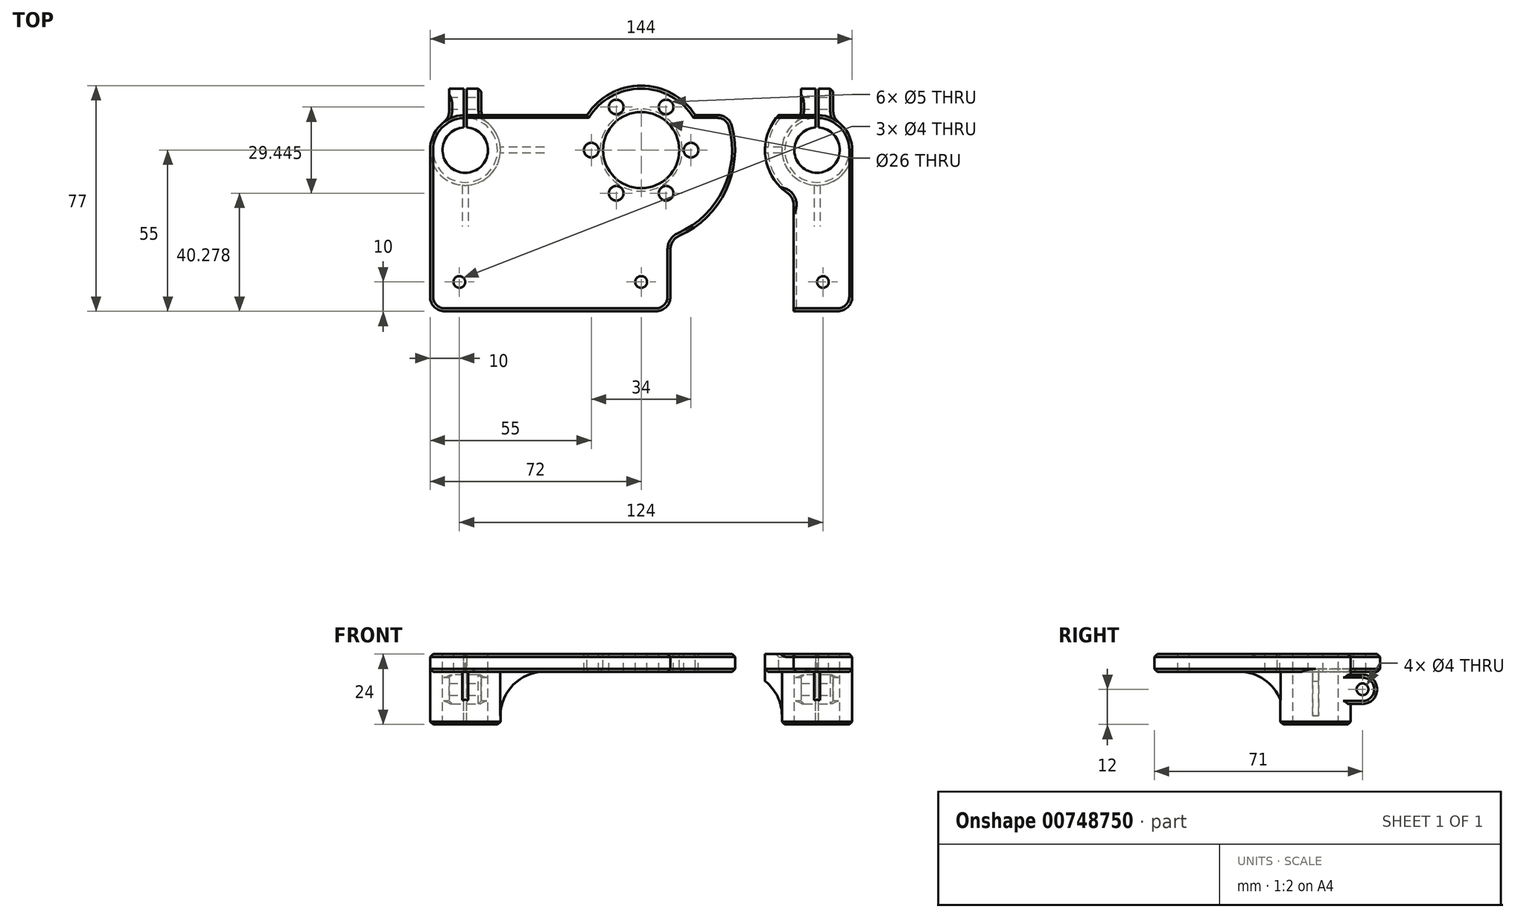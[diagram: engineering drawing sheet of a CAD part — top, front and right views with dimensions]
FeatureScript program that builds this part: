
annotation { "Feature Type Name" : "Feature", "Feature Type Description" : "" }
export const myFeature = defineFeature(function(context is Context, id is Id, definition is map)
    precondition{}
    {
        {
            var Q0;
            Q0=qCreatedBy(makeId("Front.planeOp"),FACE);
            var sketch = newSketch(context, id + "F0", { "sketchPlane" : qUnion([Q0])});
            skLineSegment(sketch, "E0.bottom", {"start": v(48, 0) * mm, "end": v(-48, 0) * mm});
            skLineSegment(sketch, "E0.top", {"start": v(33, -6) * mm, "end": v(-33, -6) * mm});
            skLineSegment(sketch, "E0.left", {"start": v(48, 0) * mm, "end": v(48, -6) * mm, "construction": true});
            skLineSegment(sketch, "E0.right", {"start": v(-48, 0) * mm, "end": v(-48, -6) * mm, "construction": true});
            skPoint(sketch, "E0.middle", {"position": v(0, 0) * mm});
            skLineSegment(sketch, "E1.bottom", {"start": v(-48, 0) * mm, "end": v(-72, 0) * mm});
            skLineSegment(sketch, "E1.top", {"start": v(-48, -24) * mm, "end": v(-72, -24) * mm});
            skLineSegment(sketch, "E1.left", {"start": v(-48, -21) * mm, "end": v(-48, -24) * mm});
            skLineSegment(sketch, "E1.right", {"start": v(-72, 0) * mm, "end": v(-72, -24) * mm});
            skLineSegment(sketch, "E2.bottom", {"start": v(48, 0) * mm, "end": v(72, 0) * mm});
            skLineSegment(sketch, "E2.top", {"start": v(48, -24) * mm, "end": v(72, -24) * mm});
            skLineSegment(sketch, "E2.left", {"start": v(48, -21) * mm, "end": v(48, -24) * mm});
            skLineSegment(sketch, "E2.right", {"start": v(72, 0) * mm, "end": v(72, -24) * mm});
            skArc(sketch, "E3.filletArc", {"start": v(-33, -6) * mm, "mid": v(-43.6, -10.4) * mm, "end": v(-48, -21) * mm});
            skArc(sketch, "E4.filletArc", {"start": v(48, -21) * mm, "mid": v(43.6, -10.4) * mm, "end": v(33, -6) * mm});
            skLineSegment(sketch, "E5", {"start": v(48, -21) * mm, "end": v(48, -6) * mm});
            skLineSegment(sketch, "E6", {"start": v(-48, -21) * mm, "end": v(-48, -6) * mm});
            skLineSegment(sketch, "E7", {"start": v(-48, -6) * mm, "end": v(-33, -6) * mm});
            skLineSegment(sketch, "E8", {"start": v(33, -6) * mm, "end": v(48, -6) * mm});
            skLineSegment(sketch, "E9", {"start": v(-48, -6) * mm, "end": v(-60, -6) * mm});
            skLineSegment(sketch, "E10", {"start": v(48, -6) * mm, "end": v(60, -6) * mm});
            skLineSegment(sketch, "E11", {"start": v(-60, -6) * mm, "end": v(-72, -6) * mm});
            skLineSegment(sketch, "E12", {"start": v(60, -6) * mm, "end": v(72, -6) * mm});
            skLineSegment(sketch, "E13", {"start": v(-60, 0) * mm, "end": v(-60, -6) * mm});
            skLineSegment(sketch, "E14", {"start": v(-60, -6) * mm, "end": v(-60, -24) * mm});
            skLineSegment(sketch, "E15", {"start": v(60, 0) * mm, "end": v(60, -6) * mm});
            skLineSegment(sketch, "E16", {"start": v(60, -6) * mm, "end": v(60, -24) * mm});
            skLineSegment(sketch, "E17", {"start": v(52.25, 0) * mm, "end": v(52.25, -24) * mm});
            skLineSegment(sketch, "E18", {"start": v(67.75, 0) * mm, "end": v(67.75, -24) * mm, "construction": true});
            skLineSegment(sketch, "E19", {"start": v(-52.25, 0) * mm, "end": v(-52.25, -24) * mm});
            skLineSegment(sketch, "E20", {"start": v(-67.75, 0) * mm, "end": v(-67.75, -24) * mm, "construction": true});
            skLineSegment(sketch, "E21", {"start": v(-48, -21) * mm, "end": v(-52.25, -21) * mm});
            skLineSegment(sketch, "E22", {"start": v(48, -21) * mm, "end": v(52.25, -21) * mm});
            skLineSegment(sketch, "E23", {"start": v(65.5, -7) * mm, "end": v(54.5, -7) * mm});
            skLineSegment(sketch, "E24", {"start": v(54.5, -7) * mm, "end": v(54.5, -17) * mm});
            skLineSegment(sketch, "E25", {"start": v(54.5, -17) * mm, "end": v(65.5, -17) * mm});
            skLineSegment(sketch, "E26", {"start": v(65.5, -7) * mm, "end": v(65.5, -17) * mm});
            skLineSegment(sketch, "E27", {"start": v(-54.5, -7) * mm, "end": v(-65.5, -7) * mm});
            skLineSegment(sketch, "E28", {"start": v(-65.5, -7) * mm, "end": v(-65.5, -17) * mm});
            skLineSegment(sketch, "E29", {"start": v(-65.5, -17) * mm, "end": v(-54.5, -17) * mm});
            skLineSegment(sketch, "E30", {"start": v(-54.5, -17) * mm, "end": v(-54.5, -7) * mm});
            skSolve(sketch);
        }
        {
            var Q0;
            Q0=makeQuery(id+"F0.imprint","IMPRINT",FACE,{"disambiguationData":[TD([[makeQuery(id+"F0.imprint","IMPRINT",EDGE,{"derivedFrom":sQuery(id+"F0.wireOp",EDGE,"E0.bottom")}),1.0]])]});
            var Q1;
            Q1=makeQuery(id+"F0.imprint","IMPRINT",FACE,{"disambiguationData":[TD([[makeQuery(id+"F0.imprint","IMPRINT",EDGE,{"derivedFrom":sQuery(id+"F0.wireOp",EDGE,"E3.filletArc")}),-1.0]])]});
            var Q2;
            Q2=makeQuery(id+"F0.imprint","IMPRINT",FACE,{"disambiguationData":[TD([[makeQuery(id+"F0.imprint","IMPRINT",EDGE,{"derivedFrom":sQuery(id+"F0.wireOp",EDGE,"E4.filletArc")}),-1.0]])]});
            var Q3;
            {var subQ2=sQuery(id+"F0.wireOp",EDGE,"E0.left");Q3=makeQuery(id+"F0.imprint","IMPRINT",FACE,{"disambiguationData":[TD([[makeQuery(id+"F0.imprint","IMPRINT",EDGE,{"derivedFrom":subQ2}),1.0]])]});}
            var Q4;
            {var subQ4=sQuery(id+"F0.wireOp",EDGE,"E0.right");Q4=makeQuery(id+"F0.imprint","IMPRINT",FACE,{"disambiguationData":[TD([[makeQuery(id+"F0.imprint","IMPRINT",EDGE,{"derivedFrom":subQ4}),-1.0]])]});}
            var Q5;
            Q5=makeQuery(id+"F0.imprint","IMPRINT",FACE,{"disambiguationData":[TD([[makeQuery(id+"F0.imprint","IMPRINT",EDGE,{"derivedFrom":sQuery(id+"F0.wireOp",EDGE,"E6")}),1.0]])]});
            var Q6;
            Q6=makeQuery(id+"F0.imprint","IMPRINT",FACE,{"disambiguationData":[TD([[makeQuery(id+"F0.imprint","IMPRINT",EDGE,{"derivedFrom":sQuery(id+"F0.wireOp",EDGE,"E5")}),-1.0]])]});
            extrude(context, id + "F1", {"entities" : qUnion([Q0, Q1, Q2, Q3, Q4, Q5, Q6]), "endBound" : BoundingType.SYMMETRIC, "depth" : 2 * mm, "offsetDistance" : 25 * mm});
        }
        {
            var Q0;
            Q0=makeQuery(id+"F0.imprint","IMPRINT",FACE,{"disambiguationData":[TD([[makeQuery(id+"F0.imprint","IMPRINT",EDGE,{"derivedFrom":sQuery(id+"F0.wireOp",EDGE,"E0.bottom")}),1.0]])]});
            var Q1;
            {var subQ4=sQuery(id+"F0.wireOp",EDGE,"E0.right");Q1=makeQuery(id+"F0.imprint","IMPRINT",FACE,{"disambiguationData":[TD([[makeQuery(id+"F0.imprint","IMPRINT",EDGE,{"derivedFrom":subQ4}),-1.0]])]});}
            var Q2;
            {var subQ2=sQuery(id+"F0.wireOp",EDGE,"E0.left");Q2=makeQuery(id+"F0.imprint","IMPRINT",FACE,{"disambiguationData":[TD([[makeQuery(id+"F0.imprint","IMPRINT",EDGE,{"derivedFrom":subQ2}),1.0]])]});}
            var Q3;
            {var subQ0=sQuery(id+"F0.wireOp",EDGE,"E15");Q3=makeQuery(id+"F0.imprint","IMPRINT",FACE,{"disambiguationData":[TD([[makeQuery(id+"F0.imprint","IMPRINT",EDGE,{"derivedFrom":subQ0}),-1.0]])]});}
            var Q4;
            {var subQ0=sQuery(id+"F0.wireOp",EDGE,"E13");Q4=makeQuery(id+"F0.imprint","IMPRINT",FACE,{"disambiguationData":[TD([[makeQuery(id+"F0.imprint","IMPRINT",EDGE,{"derivedFrom":subQ0}),1.0]])]});}
            extrude(context, id + "F2", {"entities" : qUnion([Q0, Q1, Q2, Q3, Q4]), "operationType" : NewBodyOperationType.ADD, "oppositeDirection" : true, "depth" : 12 * mm, "offsetDistance" : 25 * mm});
        }
        {
            var Q0;
            {var subQ0=sQuery(id+"F0.wireOp",EDGE,"E2.right");var subQ1=sQuery(id+"F0.wireOp",EDGE,"E2.bottom");var subQ2=makeQuery(id+"F0.imprint","INTERSECT",VERTEX,{"derivedFrom":[subQ1,subQ0]});Q0=makeQuery(id+"F0.imprint","IMPRINT",FACE,{"disambiguationData":[TD([[makeQuery(id+"F0.imprint","IMPRINT",EDGE,{"disambiguationData":[TD([[subQ2,1.0]])],"derivedFrom":subQ1}),-1.0]])]});}
            var Q1;
            {var subQ0=sQuery(id+"F0.wireOp",EDGE,"E15");Q1=makeQuery(id+"F0.imprint","IMPRINT",FACE,{"disambiguationData":[TD([[makeQuery(id+"F0.imprint","IMPRINT",EDGE,{"derivedFrom":subQ0}),1.0]])]});}
            var Q2;
            {var subQ0=sQuery(id+"F0.wireOp",EDGE,"E15");Q2=makeQuery(id+"F0.imprint","IMPRINT",FACE,{"disambiguationData":[TD([[makeQuery(id+"F0.imprint","IMPRINT",EDGE,{"derivedFrom":subQ0}),-1.0]])]});}
            var Q3;
            {var subQ0=sQuery(id+"F0.wireOp",EDGE,"E0.left");Q3=makeQuery(id+"F0.imprint","IMPRINT",FACE,{"disambiguationData":[TD([[makeQuery(id+"F0.imprint","IMPRINT",EDGE,{"derivedFrom":subQ0}),1.0]])]});}
            var Q4;
            Q4=makeQuery(id+"F0.imprint","IMPRINT",FACE,{"disambiguationData":[TD([[makeQuery(id+"F0.imprint","IMPRINT",EDGE,{"derivedFrom":sQuery(id+"F0.wireOp",EDGE,"E0.bottom")}),1.0]])]});
            var Q5;
            {var subQ0=sQuery(id+"F0.wireOp",EDGE,"E0.right");Q5=makeQuery(id+"F0.imprint","IMPRINT",FACE,{"disambiguationData":[TD([[makeQuery(id+"F0.imprint","IMPRINT",EDGE,{"derivedFrom":subQ0}),-1.0]])]});}
            var Q6;
            {var subQ4=sQuery(id+"F0.wireOp",EDGE,"E11");Q6=makeQuery(id+"F0.imprint","IMPRINT",FACE,{"disambiguationData":[TD([[makeQuery(id+"F0.imprint","IMPRINT",EDGE,{"derivedFrom":subQ4}),-1.0]])]});}
            var Q7;
            {var subQ0=sQuery(id+"F0.wireOp",EDGE,"E13");Q7=makeQuery(id+"F0.imprint","IMPRINT",FACE,{"disambiguationData":[TD([[makeQuery(id+"F0.imprint","IMPRINT",EDGE,{"derivedFrom":subQ0}),1.0]])]});}
            extrude(context, id + "F3", {"entities" : qUnion([Q0, Q1, Q2, Q3, Q4, Q5, Q6, Q7]), "operationType" : NewBodyOperationType.ADD, "depth" : 55 * mm, "offsetDistance" : 25 * mm});
        }
        {
            var Q0;
            {var subQ0=sQuery(id+"F0.wireOp",EDGE,"E2.bottom");var subQ1=sQuery(id+"F0.wireOp",EDGE,"E1.bottom");var subQ2=sQuery(id+"F0.wireOp",EDGE,"E0.bottom");Q0=makeQuery(id+"F20427sbasGo161_1.boolean.opBoolean","MERGE",FACE,{"derivedFrom":[makeQuery(id+"F7.boolean.opBoolean","MERGE",FACE,{"derivedFrom":[makeQuery(id+"F3.boolean.opBoolean","MERGE",FACE,{"derivedFrom":[makeQuery(id+"F2.boolean.opBoolean","MERGE",FACE,{"derivedFrom":[makeQuery(id+"F1.opExtrude","SWEPT_FACE",FACE,{"disambiguationData":[OSD([subQ2,subQ1,subQ0])]}),makeQuery(id+"F2.opExtrude","SWEPT_FACE",FACE,{"disambiguationData":[OSD([subQ2,subQ1,subQ0])]})]}),makeQuery(id+"F3.opExtrude","SWEPT_FACE",FACE,{"disambiguationData":[OSD([subQ2,subQ1,subQ0])]})]}),makeQuery(id+"F7.opRevolve","SWEPT_FACE",FACE,{"disambiguationData":[OSD([subQ1])]})]}),makeQuery(id+"F20427sbasGo161_1.opRevolve","SWEPT_FACE",FACE,{"disambiguationData":[OSD([subQ0])]})]});}
            var sketch = newSketch(context, id + "F4", { "sketchPlane" : qUnion([Q0])});
            skCircle(sketch, "E31", {"center": v(-62, -45) * mm, "radius": 2 * mm});
            skCircle(sketch, "E32", {"center": v(62, -45) * mm, "radius": 2 * mm});
            skCircle(sketch, "E33", {"center": v(0, 0) * mm, "radius": 13 * mm});
            skCircle(sketch, "E34", {"center": v(0, 0) * mm, "radius": 17 * mm, "construction": true});
            skCircle(sketch, "E35", {"center": v(-17, 0) * mm, "radius": 2.5 * mm});
            skCircle(sketch, "E36", {"center": v(17, 0) * mm, "radius": 2.5 * mm});
            skCircle(sketch, "E37", {"center": v(-8.5, 14.72) * mm, "radius": 2.5 * mm});
            skCircle(sketch, "E38", {"center": v(8.5, -14.72) * mm, "radius": 2.5 * mm});
            skCircle(sketch, "E39", {"center": v(-8.5, -14.72) * mm, "radius": 2.5 * mm});
            skCircle(sketch, "E40", {"center": v(8.5, 14.72) * mm, "radius": 2.5 * mm});
            skCircle(sketch, "E41", {"center": v(0, 0) * mm, "radius": 22 * mm});
            skCircle(sketch, "E42", {"center": v(-60, 0) * mm, "radius": 7.75 * mm});
            skCircle(sketch, "E43", {"center": v(60, 0) * mm, "radius": 7.75 * mm});
            skLineSegment(sketch, "E44", {"start": v(-60, 0) * mm, "end": v(-60, 30) * mm, "construction": true});
            skLineSegment(sketch, "E45", {"start": v(-60, 30) * mm, "end": v(-59.5, 30) * mm});
            skLineSegment(sketch, "E46", {"start": v(-59.5, 0) * mm, "end": v(-60, 0) * mm});
            skLineSegment(sketch, "E47", {"start": v(-59.5, 30) * mm, "end": v(-59.5, 0) * mm});
            skLineSegment(sketch, "E48", {"start": v(-60, 0) * mm, "end": v(-60.5, 0) * mm});
            skLineSegment(sketch, "E49", {"start": v(-60.5, 0) * mm, "end": v(-60.5, 30) * mm});
            skLineSegment(sketch, "E50", {"start": v(-60.5, 30) * mm, "end": v(-60, 30) * mm});
            skLineSegment(sketch, "E51", {"start": v(60, 0) * mm, "end": v(60, 30) * mm, "construction": true});
            skLineSegment(sketch, "E52", {"start": v(60, 30) * mm, "end": v(59.5, 30) * mm});
            skLineSegment(sketch, "E53", {"start": v(59.5, 30) * mm, "end": v(59.5, 0) * mm});
            skLineSegment(sketch, "E54", {"start": v(59.5, 0) * mm, "end": v(60, 0) * mm});
            skLineSegment(sketch, "E55", {"start": v(60, 0) * mm, "end": v(60.5, 0) * mm});
            skLineSegment(sketch, "E56", {"start": v(60.5, 0) * mm, "end": v(60.5, 30) * mm});
            skLineSegment(sketch, "E57", {"start": v(60.5, 30) * mm, "end": v(60, 30) * mm});
            skCircle(sketch, "E58", {"center": v(0, -45) * mm, "radius": 2 * mm});
            skCircle(sketch, "E59", {"center": v(0, 0) * mm, "radius": 32 * mm});
            skCircle(sketch, "E60", {"center": v(-60, 0) * mm, "radius": 17.75 * mm});
            skCircle(sketch, "E61", {"center": v(60, 0) * mm, "radius": 17.75 * mm});
            skLineSegment(sketch, "E62", {"start": v(-52, -55) * mm, "end": v(-52, 0) * mm});
            skLineSegment(sketch, "E63", {"start": v(52, -55) * mm, "end": v(52, 0) * mm});
            skLineSegment(sketch, "E64", {"start": v(-10, -55) * mm, "end": v(-10, 0) * mm});
            skLineSegment(sketch, "E65", {"start": v(10, -55) * mm, "end": v(10, 0) * mm});
            skLineSegment(sketch, "E66", {"start": v(-52, -12) * mm, "end": v(52, -12) * mm});
            skSolve(sketch);
        }
        {
            var Q0;
            Q0=makeQuery(id+"F4.imprint","IMPRINT",FACE,{"disambiguationData":[TD([[makeQuery(id+"F4.imprint","IMPRINT",EDGE,{"derivedFrom":sQuery(id+"F4.wireOp",EDGE,"E37")}),-1.0]])]});
            var Q1;
            {var subQ0=sQuery(id+"F4.wireOp",EDGE,"E33");var subQ1=makeQuery(id+"F2.opExtrude","CAP_EDGE",EDGE,{"disambiguationData":[OSD([sQuery(id+"F0.wireOp",EDGE,"E0.bottom"),sQuery(id+"F0.wireOp",EDGE,"E1.bottom"),sQuery(id+"F0.wireOp",EDGE,"E2.bottom")])],"isStart":false});var subQ2=makeQuery(id+"F4.imprint","INTERSECT",VERTEX,{"disambiguationData":[OD(0.0)],"derivedFrom":[subQ1,subQ0]});Q1=makeQuery(id+"F4.imprint","IMPRINT",FACE,{"disambiguationData":[TD([[makeQuery(id+"F4.imprint","IMPRINT",EDGE,{"disambiguationData":[TD([[subQ2,1.0]])],"derivedFrom":subQ0}),1.0]])]});}
            extrude(context, id + "F5", {"entities" : qUnion([Q0, Q1]), "operationType" : NewBodyOperationType.ADD, "oppositeDirection" : true, "depth" : 6 * mm, "offsetDistance" : 25 * mm});
        }
        {
            var Q0;
            {var subQ1=sQuery(id+"F0.wireOp",EDGE,"E11");Q0=makeQuery(id+"F0.imprint","IMPRINT",FACE,{"disambiguationData":[TD([[makeQuery(id+"F0.imprint","IMPRINT",EDGE,{"derivedFrom":subQ1}),1.0]])]});}
            var Q1;
            {var subQ4=sQuery(id+"F0.wireOp",EDGE,"E11");Q1=makeQuery(id+"F0.imprint","IMPRINT",FACE,{"disambiguationData":[TD([[makeQuery(id+"F0.imprint","IMPRINT",EDGE,{"derivedFrom":subQ4}),-1.0]])]});}
            var Q2;
            Q2=sQuery(id+"F0.wireOp",EDGE,"E13");
            revolve(context, id + "F6", {"operationType" : NewBodyOperationType.ADD, "surfaceOperationType" : NewSurfaceOperationType.NEW, "entities" : qUnion([Q0, Q1]), "axis" : qUnion([Q2]), "revolveType" : RevolveType.FULL});
        }
        {
            var Q0;
            {var subQ4=sQuery(id+"F0.wireOp",EDGE,"E12");Q0=makeQuery(id+"F0.imprint","IMPRINT",FACE,{"disambiguationData":[TD([[makeQuery(id+"F0.imprint","IMPRINT",EDGE,{"derivedFrom":subQ4}),1.0]])]});}
            var Q1;
            {var subQ4=sQuery(id+"F0.wireOp",EDGE,"E12");Q1=makeQuery(id+"F0.imprint","IMPRINT",FACE,{"disambiguationData":[TD([[makeQuery(id+"F0.imprint","IMPRINT",EDGE,{"derivedFrom":subQ4}),-1.0]])]});}
            var Q2;
            Q2=sQuery(id+"F0.wireOp",EDGE,"E16");
            revolve(context, id + "F7", {"operationType" : NewBodyOperationType.ADD, "surfaceOperationType" : NewSurfaceOperationType.NEW, "entities" : qUnion([Q0, Q1]), "axis" : qUnion([Q2]), "revolveType" : RevolveType.FULL});
        }
        {
            var Q0;
            {var subQ5=sQuery(id+"F0.wireOp",EDGE,"E26");Q0=makeQuery(id+"F0.imprint","IMPRINT",FACE,{"disambiguationData":[TD([[makeQuery(id+"F0.imprint","IMPRINT",EDGE,{"derivedFrom":subQ5}),-1.0]])]});}
            var Q1;
            {var subQ5=sQuery(id+"F0.wireOp",EDGE,"E24");Q1=makeQuery(id+"F0.imprint","IMPRINT",FACE,{"disambiguationData":[TD([[makeQuery(id+"F0.imprint","IMPRINT",EDGE,{"derivedFrom":subQ5}),1.0]])]});}
            var Q2;
            {var subQ5=sQuery(id+"F0.wireOp",EDGE,"E30");Q2=makeQuery(id+"F0.imprint","IMPRINT",FACE,{"disambiguationData":[TD([[makeQuery(id+"F0.imprint","IMPRINT",EDGE,{"derivedFrom":subQ5}),1.0]])]});}
            var Q3;
            {var subQ5=sQuery(id+"F0.wireOp",EDGE,"E28");Q3=makeQuery(id+"F0.imprint","IMPRINT",FACE,{"disambiguationData":[TD([[makeQuery(id+"F0.imprint","IMPRINT",EDGE,{"derivedFrom":subQ5}),1.0]])]});}
            extrude(context, id + "F8", {"entities" : qUnion([Q0, Q1, Q2, Q3]), "operationType" : NewBodyOperationType.ADD, "oppositeDirection" : true, "depth" : 21 * mm, "offsetDistance" : 25 * mm});
        }
        {
            var Q0;
            Q0=makeQuery(id+"F4.imprint","IMPRINT",FACE,{"disambiguationData":[TD([[makeQuery(id+"F4.imprint","IMPRINT",EDGE,{"derivedFrom":sQuery(id+"F4.wireOp",EDGE,"E36")}),1.0]])]});
            var Q1;
            Q1=makeQuery(id+"F4.imprint","IMPRINT",FACE,{"disambiguationData":[TD([[makeQuery(id+"F4.imprint","IMPRINT",EDGE,{"derivedFrom":sQuery(id+"F4.wireOp",EDGE,"E40")}),1.0]])]});
            var Q2;
            Q2=makeQuery(id+"F4.imprint","IMPRINT",FACE,{"disambiguationData":[TD([[makeQuery(id+"F4.imprint","IMPRINT",EDGE,{"derivedFrom":sQuery(id+"F4.wireOp",EDGE,"E37")}),1.0]])]});
            var Q3;
            Q3=makeQuery(id+"F4.imprint","IMPRINT",FACE,{"disambiguationData":[TD([[makeQuery(id+"F4.imprint","IMPRINT",EDGE,{"derivedFrom":sQuery(id+"F4.wireOp",EDGE,"E35")}),1.0]])]});
            var Q4;
            Q4=makeQuery(id+"F4.imprint","IMPRINT",FACE,{"disambiguationData":[TD([[makeQuery(id+"F4.imprint","IMPRINT",EDGE,{"derivedFrom":sQuery(id+"F4.wireOp",EDGE,"E39")}),1.0]])]});
            var Q5;
            Q5=makeQuery(id+"F4.imprint","IMPRINT",FACE,{"disambiguationData":[TD([[makeQuery(id+"F4.imprint","IMPRINT",EDGE,{"derivedFrom":sQuery(id+"F4.wireOp",EDGE,"E38")}),1.0]])]});
            var Q6;
            Q6=makeQuery(id+"F4.imprint","IMPRINT",FACE,{"disambiguationData":[TD([[makeQuery(id+"F4.imprint","IMPRINT",EDGE,{"derivedFrom":sQuery(id+"F4.wireOp",EDGE,"Tndr1YZz-FnOl-Mpse-pdtd-fPx6EetpAfF0")}),1.0]])]});
            var Q7;
            Q7=makeQuery(id+"F4.imprint","IMPRINT",FACE,{"disambiguationData":[TD([[makeQuery(id+"F4.imprint","IMPRINT",EDGE,{"derivedFrom":sQuery(id+"F4.wireOp",EDGE,"twqygBex-jMNA-Eus5-QEq3-cVCOdjelJbA5")}),1.0]])]});
            var Q8;
            Q8=makeQuery(id+"F4.imprint","IMPRINT",FACE,{"disambiguationData":[TD([[makeQuery(id+"F4.imprint","IMPRINT",EDGE,{"derivedFrom":sQuery(id+"F4.wireOp",EDGE,"E31")}),1.0]])]});
            var Q9;
            Q9=makeQuery(id+"F4.imprint","IMPRINT",FACE,{"disambiguationData":[TD([[makeQuery(id+"F4.imprint","IMPRINT",EDGE,{"derivedFrom":sQuery(id+"F4.wireOp",EDGE,"E32")}),1.0]])]});
            var Q10;
            {var subQ0=sQuery(id+"F4.wireOp",EDGE,"E33");var subQ1=makeQuery(id+"F2.opExtrude","CAP_EDGE",EDGE,{"disambiguationData":[OSD([sQuery(id+"F0.wireOp",EDGE,"E0.bottom"),sQuery(id+"F0.wireOp",EDGE,"E1.bottom"),sQuery(id+"F0.wireOp",EDGE,"E2.bottom")])],"isStart":false});var subQ2=makeQuery(id+"F4.imprint","INTERSECT",VERTEX,{"disambiguationData":[OD(0.0)],"derivedFrom":[subQ1,subQ0]});Q10=makeQuery(id+"F4.imprint","IMPRINT",FACE,{"disambiguationData":[TD([[makeQuery(id+"F4.imprint","IMPRINT",EDGE,{"disambiguationData":[TD([[subQ2,-1.0]])],"derivedFrom":subQ0}),1.0]])]});}
            var Q11;
            {var subQ0=sQuery(id+"F4.wireOp",EDGE,"E33");var subQ1=makeQuery(id+"F2.opExtrude","CAP_EDGE",EDGE,{"disambiguationData":[OSD([sQuery(id+"F0.wireOp",EDGE,"E0.bottom"),sQuery(id+"F0.wireOp",EDGE,"E1.bottom"),sQuery(id+"F0.wireOp",EDGE,"E2.bottom")])],"isStart":false});var subQ2=makeQuery(id+"F4.imprint","INTERSECT",VERTEX,{"disambiguationData":[OD(0.0)],"derivedFrom":[subQ1,subQ0]});Q11=makeQuery(id+"F4.imprint","IMPRINT",FACE,{"disambiguationData":[TD([[makeQuery(id+"F4.imprint","IMPRINT",EDGE,{"disambiguationData":[TD([[subQ2,1.0]])],"derivedFrom":subQ0}),1.0]])]});}
            var Q12;
            {var subQ0=sQuery(id+"F4.wireOp",EDGE,"E42");var subQ1=sQuery(id+"F0.wireOp",EDGE,"E13");var subQ2=sQuery(id+"F0.wireOp",EDGE,"E1.bottom");var subQ3=makeQuery(id+"F2.opExtrude","SWEPT_EDGE",EDGE,{"disambiguationData":[OSD([subQ2,subQ1])]});var subQ4=makeQuery(id+"F4.imprint","INTERSECT",VERTEX,{"derivedFrom":[subQ3,subQ0]});Q12=makeQuery(id+"F4.imprint","IMPRINT",FACE,{"disambiguationData":[TD([[makeQuery(id+"F4.imprint","IMPRINT",EDGE,{"disambiguationData":[TD([[subQ4,1.0]])],"derivedFrom":subQ0}),1.0]])]});}
            var Q13;
            {var subQ0=sQuery(id+"F4.wireOp",EDGE,"E42");var subQ1=sQuery(id+"F0.wireOp",EDGE,"E13");var subQ2=sQuery(id+"F0.wireOp",EDGE,"E1.bottom");var subQ3=makeQuery(id+"F2.opExtrude","SWEPT_EDGE",EDGE,{"disambiguationData":[OSD([subQ2,subQ1])]});var subQ4=makeQuery(id+"F4.imprint","INTERSECT",VERTEX,{"derivedFrom":[subQ3,subQ0]});Q13=makeQuery(id+"F4.imprint","IMPRINT",FACE,{"disambiguationData":[TD([[makeQuery(id+"F4.imprint","IMPRINT",EDGE,{"disambiguationData":[TD([[subQ4,-1.0]])],"derivedFrom":subQ0}),1.0]])]});}
            var Q14;
            {var subQ0=sQuery(id+"F4.wireOp",EDGE,"E43");var subQ1=sQuery(id+"F0.wireOp",EDGE,"E15");var subQ2=sQuery(id+"F0.wireOp",EDGE,"E2.bottom");var subQ3=makeQuery(id+"F2.opExtrude","SWEPT_EDGE",EDGE,{"disambiguationData":[OSD([subQ2,subQ1])]});var subQ4=makeQuery(id+"F4.imprint","INTERSECT",VERTEX,{"derivedFrom":[subQ3,subQ0]});Q14=makeQuery(id+"F4.imprint","IMPRINT",FACE,{"disambiguationData":[TD([[makeQuery(id+"F4.imprint","IMPRINT",EDGE,{"disambiguationData":[TD([[subQ4,-1.0]])],"derivedFrom":subQ0}),1.0]])]});}
            var Q15;
            {var subQ0=sQuery(id+"F4.wireOp",EDGE,"E43");var subQ1=sQuery(id+"F0.wireOp",EDGE,"E15");var subQ2=sQuery(id+"F0.wireOp",EDGE,"E2.bottom");var subQ3=makeQuery(id+"F2.opExtrude","SWEPT_EDGE",EDGE,{"disambiguationData":[OSD([subQ2,subQ1])]});var subQ4=makeQuery(id+"F4.imprint","INTERSECT",VERTEX,{"derivedFrom":[subQ3,subQ0]});Q15=makeQuery(id+"F4.imprint","IMPRINT",FACE,{"disambiguationData":[TD([[makeQuery(id+"F4.imprint","IMPRINT",EDGE,{"disambiguationData":[TD([[subQ4,1.0]])],"derivedFrom":subQ0}),1.0]])]});}
            var Q16;
            {var subQ0=sQuery(id+"F4.wireOp",EDGE,"E49");var subQ1=sQuery(id+"F4.wireOp",EDGE,"E42");var subQ2=makeQuery(id+"F4.imprint","INTERSECT",VERTEX,{"derivedFrom":[subQ1,subQ0]});Q16=makeQuery(id+"F4.imprint","IMPRINT",FACE,{"disambiguationData":[TD([[makeQuery(id+"F4.imprint","IMPRINT",EDGE,{"disambiguationData":[TD([[subQ2,-1.0]])],"derivedFrom":subQ1}),1.0]])]});}
            var Q17;
            {var subQ1=sQuery(id+"F4.wireOp",EDGE,"E46");Q17=makeQuery(id+"F4.imprint","IMPRINT",FACE,{"disambiguationData":[TD([[makeQuery(id+"F4.imprint","IMPRINT",EDGE,{"derivedFrom":subQ1}),1.0]])]});}
            var Q18;
            {var subQ0=sQuery(id+"F4.wireOp",EDGE,"E56");var subQ1=sQuery(id+"F4.wireOp",EDGE,"E43");var subQ2=makeQuery(id+"F4.imprint","INTERSECT",VERTEX,{"derivedFrom":[subQ1,subQ0]});Q18=makeQuery(id+"F4.imprint","IMPRINT",FACE,{"disambiguationData":[TD([[makeQuery(id+"F4.imprint","IMPRINT",EDGE,{"disambiguationData":[TD([[subQ2,1.0]])],"derivedFrom":subQ1}),1.0]])]});}
            var Q19;
            {var subQ0=sQuery(id+"F4.wireOp",EDGE,"E54");Q19=makeQuery(id+"F4.imprint","IMPRINT",FACE,{"disambiguationData":[TD([[makeQuery(id+"F4.imprint","IMPRINT",EDGE,{"derivedFrom":subQ0}),-1.0]])]});}
            var Q20;
            {var subQ5=sQuery(id+"F4.wireOp",EDGE,"E52");Q20=makeQuery(id+"F4.imprint","IMPRINT",FACE,{"disambiguationData":[TD([[makeQuery(id+"F4.imprint","IMPRINT",EDGE,{"derivedFrom":subQ5}),1.0]])]});}
            var Q21;
            Q21=makeQuery(id+"F4.imprint","IMPRINT",FACE,{"disambiguationData":[TD([[makeQuery(id+"F4.imprint","IMPRINT",EDGE,{"derivedFrom":sQuery(id+"F4.wireOp",EDGE,"E58")}),1.0]])]});
            var Q22;
            {var subQ0=sQuery(id+"F4.wireOp",EDGE,"E47");var subQ1=sQuery(id+"F4.wireOp",EDGE,"E42");var subQ2=makeQuery(id+"F4.imprint","INTERSECT",VERTEX,{"derivedFrom":[subQ1,subQ0]});Q22=makeQuery(id+"F4.imprint","IMPRINT",FACE,{"disambiguationData":[TD([[makeQuery(id+"F4.imprint","IMPRINT",EDGE,{"disambiguationData":[TD([[subQ2,-1.0]])],"derivedFrom":subQ1}),-1.0]])]});}
            var Q23;
            {var subQ5=sQuery(id+"F4.wireOp",EDGE,"E45");Q23=makeQuery(id+"F4.imprint","IMPRINT",FACE,{"disambiguationData":[TD([[makeQuery(id+"F4.imprint","IMPRINT",EDGE,{"derivedFrom":subQ5}),-1.0]])]});}
            var Q24;
            {var subQ0=sQuery(id+"F4.wireOp",EDGE,"E53");var subQ1=sQuery(id+"F4.wireOp",EDGE,"E43");var subQ2=makeQuery(id+"F4.imprint","INTERSECT",VERTEX,{"derivedFrom":[subQ1,subQ0]});Q24=makeQuery(id+"F4.imprint","IMPRINT",FACE,{"disambiguationData":[TD([[makeQuery(id+"F4.imprint","IMPRINT",EDGE,{"disambiguationData":[TD([[subQ2,1.0]])],"derivedFrom":subQ1}),-1.0]])]});}
            var Q25;
            {var subQ0=sQuery(id+"F4.wireOp",EDGE,"E66");var subQ1=sQuery(id+"F4.wireOp",EDGE,"E33");var subQ2=makeQuery(id+"F4.imprint","INTERSECT",VERTEX,{"disambiguationData":[OD(0.0)],"derivedFrom":[subQ1,subQ0]});Q25=makeQuery(id+"F4.imprint","IMPRINT",FACE,{"disambiguationData":[TD([[makeQuery(id+"F4.imprint","IMPRINT",EDGE,{"disambiguationData":[TD([[subQ2,-1.0]])],"derivedFrom":subQ1}),1.0]])]});}
            var Q26;
            {var subQ0=sQuery(id+"F4.wireOp",EDGE,"E60");var subQ3=sQuery(id+"F4.wireOp",EDGE,"E49");var subQ4=makeQuery(id+"F4.imprint","INTERSECT",VERTEX,{"derivedFrom":[subQ3,subQ0]});Q26=makeQuery(id+"F4.imprint","IMPRINT",FACE,{"disambiguationData":[TD([[makeQuery(id+"F4.imprint","IMPRINT",EDGE,{"disambiguationData":[TD([[subQ4,1.0]])],"derivedFrom":subQ3}),-1.0]])]});}
            var Q27;
            {var subQ0=sQuery(id+"F4.wireOp",EDGE,"E61");var subQ3=sQuery(id+"F4.wireOp",EDGE,"E56");var subQ4=makeQuery(id+"F4.imprint","INTERSECT",VERTEX,{"derivedFrom":[subQ3,subQ0]});Q27=makeQuery(id+"F4.imprint","IMPRINT",FACE,{"disambiguationData":[TD([[makeQuery(id+"F4.imprint","IMPRINT",EDGE,{"disambiguationData":[TD([[subQ4,1.0]])],"derivedFrom":subQ3}),1.0]])]});}
            extrude(context, id + "F9", {"entities" : qUnion([Q0, Q1, Q2, Q3, Q4, Q5, Q6, Q7, Q8, Q9, Q10, Q11, Q12, Q13, Q14, Q15, Q16, Q17, Q18, Q19, Q20, Q21, Q22, Q23, Q24, Q25, Q26, Q27]), "operationType" : NewBodyOperationType.REMOVE, "oppositeDirection" : true, "depth" : 24 * mm, "offsetDistance" : 25 * mm});
        }
        {
            var Q0;
            Q0=makeQuery(id+"F8.opExtrude","SWEPT_FACE",FACE,{"disambiguationData":[OSD([sQuery(id+"F0.wireOp",EDGE,"E26")])]});
            var sketch = newSketch(context, id + "F10", { "sketchPlane" : qUnion([Q0])});
            skCircle(sketch, "E67", {"center": v(16, -12) * mm, "radius": 2 * mm});
            skSolve(sketch);
        }
        {
            var Q0;
            Q0=makeQuery(id+"F10.imprint","IMPRINT",FACE,{"disambiguationData":[TD([[makeQuery(id+"F10.imprint","IMPRINT",EDGE,{"derivedFrom":sQuery(id+"F10.wireOp",EDGE,"E67")}),1.0]])]});
            extrude(context, id + "F11", {"entities" : qUnion([Q0]), "operationType" : NewBodyOperationType.REMOVE, "oppositeDirection" : true, "depth" : 150 * mm, "offsetDistance" : 25 * mm});
        }
        {
            var Q0;
            {var subQ0=sQuery(id+"F4.wireOp",EDGE,"E65");var subQ3=sQuery(id+"F4.wireOp",EDGE,"E59");var subQ4=makeQuery(id+"F4.imprint","INTERSECT",VERTEX,{"derivedFrom":[subQ3,subQ0]});Q0=makeQuery(id+"F4.imprint","IMPRINT",FACE,{"disambiguationData":[TD([[makeQuery(id+"F4.imprint","IMPRINT",EDGE,{"disambiguationData":[TD([[subQ4,-1.0]])],"derivedFrom":subQ3}),-1.0]])]});}
            var Q1;
            {var subQ5=sQuery(id+"F4.wireOp",EDGE,"E66");var subQ9=sQuery(id+"F4.wireOp",EDGE,"E59");var subQ11=makeQuery(id+"F4.imprint","INTERSECT",VERTEX,{"disambiguationData":[OD(0.0)],"derivedFrom":[subQ9,subQ5]});Q1=makeQuery(id+"F4.imprint","IMPRINT",FACE,{"disambiguationData":[TD([[makeQuery(id+"F4.imprint","IMPRINT",EDGE,{"disambiguationData":[TD([[subQ11,-1.0]])],"derivedFrom":subQ9}),-1.0]])]});}
            extrude(context, id + "F12", {"entities" : qUnion([Q0, Q1]), "operationType" : NewBodyOperationType.REMOVE, "oppositeDirection" : true, "depth" : 25 * mm, "offsetDistance" : 25 * mm});
        }
        {
            var Q0;
            {var subQ0=sQuery(id+"F0.wireOp",EDGE,"vOBMJWDl-Fj1z-wCYs-OJKp-ljOS09Nf5rD4.bottom");var subQ1=sQuery(id+"F0.wireOp",EDGE,"vOBMJWDl-Fj1z-wCYs-OJKp-ljOS09Nf5rD4.left");Q0=makeQuery(id+"F9.boolean.opBoolean","SPLIT",EDGE,{"disambiguationData":[TD([makeQuery(id+"FyEnq1fhFwSBqjL_0.opExtrude","SWEPT_FACE",FACE,{"disambiguationData":[OSD([subQ1])]})])],"derivedFrom":makeQuery(id+"FyEnq1fhFwSBqjL_0.opExtrude","CAP_EDGE",EDGE,{"disambiguationData":[OSD([subQ0])],"isStart":false})});}
            var Q1;
            {var subQ0=sQuery(id+"F0.wireOp",EDGE,"vOBMJWDl-Fj1z-wCYs-OJKp-ljOS09Nf5rD4.bottom");var subQ1=sQuery(id+"F0.wireOp",EDGE,"vOBMJWDl-Fj1z-wCYs-OJKp-ljOS09Nf5rD4.right");Q1=makeQuery(id+"F9.boolean.opBoolean","SPLIT",EDGE,{"disambiguationData":[TD([makeQuery(id+"FyEnq1fhFwSBqjL_0.opExtrude","SWEPT_FACE",FACE,{"disambiguationData":[OSD([subQ1])]})])],"derivedFrom":makeQuery(id+"FyEnq1fhFwSBqjL_0.opExtrude","CAP_EDGE",EDGE,{"disambiguationData":[OSD([subQ0])],"isStart":false})});}
            var Q2;
            {var subQ0=sQuery(id+"F0.wireOp",EDGE,"vOBMJWDl-Fj1z-wCYs-OJKp-ljOS09Nf5rD4.right");var subQ1=sQuery(id+"F0.wireOp",EDGE,"vOBMJWDl-Fj1z-wCYs-OJKp-ljOS09Nf5rD4.top");Q2=makeQuery(id+"F9.boolean.opBoolean","SPLIT",EDGE,{"disambiguationData":[TD([makeQuery(id+"FyEnq1fhFwSBqjL_0.opExtrude","SWEPT_FACE",FACE,{"disambiguationData":[OSD([subQ0])]})])],"derivedFrom":makeQuery(id+"FyEnq1fhFwSBqjL_0.opExtrude","CAP_EDGE",EDGE,{"disambiguationData":[OSD([subQ1])],"isStart":false})});}
            var Q3;
            {var subQ0=sQuery(id+"F0.wireOp",EDGE,"vOBMJWDl-Fj1z-wCYs-OJKp-ljOS09Nf5rD4.left");var subQ1=sQuery(id+"F0.wireOp",EDGE,"vOBMJWDl-Fj1z-wCYs-OJKp-ljOS09Nf5rD4.top");Q3=makeQuery(id+"F9.boolean.opBoolean","SPLIT",EDGE,{"disambiguationData":[TD([makeQuery(id+"FyEnq1fhFwSBqjL_0.opExtrude","SWEPT_FACE",FACE,{"disambiguationData":[OSD([subQ0])]})])],"derivedFrom":makeQuery(id+"FyEnq1fhFwSBqjL_0.opExtrude","CAP_EDGE",EDGE,{"disambiguationData":[OSD([subQ1])],"isStart":false})});}
            var Q4;
            {var subQ0=sQuery(id+"F0.wireOp",EDGE,"ieqPwXpz-Zkmp-sPIe-4gTk-vNAapPMGIJea.bottom");var subQ1=sQuery(id+"F0.wireOp",EDGE,"ieqPwXpz-Zkmp-sPIe-4gTk-vNAapPMGIJea.right");Q4=makeQuery(id+"F9.boolean.opBoolean","SPLIT",EDGE,{"disambiguationData":[TD([makeQuery(id+"FyEnq1fhFwSBqjL_0.opExtrude","SWEPT_FACE",FACE,{"disambiguationData":[OSD([subQ1])]})])],"derivedFrom":makeQuery(id+"FyEnq1fhFwSBqjL_0.opExtrude","CAP_EDGE",EDGE,{"disambiguationData":[OSD([subQ0])],"isStart":false})});}
            var Q5;
            {var subQ0=sQuery(id+"F0.wireOp",EDGE,"ieqPwXpz-Zkmp-sPIe-4gTk-vNAapPMGIJea.right");var subQ1=sQuery(id+"F0.wireOp",EDGE,"ieqPwXpz-Zkmp-sPIe-4gTk-vNAapPMGIJea.top");Q5=makeQuery(id+"F9.boolean.opBoolean","SPLIT",EDGE,{"disambiguationData":[TD([makeQuery(id+"FyEnq1fhFwSBqjL_0.opExtrude","SWEPT_FACE",FACE,{"disambiguationData":[OSD([subQ0])]})])],"derivedFrom":makeQuery(id+"FyEnq1fhFwSBqjL_0.opExtrude","CAP_EDGE",EDGE,{"disambiguationData":[OSD([subQ1])],"isStart":false})});}
            var Q6;
            {var subQ0=sQuery(id+"F0.wireOp",EDGE,"ieqPwXpz-Zkmp-sPIe-4gTk-vNAapPMGIJea.left");var subQ1=sQuery(id+"F0.wireOp",EDGE,"ieqPwXpz-Zkmp-sPIe-4gTk-vNAapPMGIJea.top");Q6=makeQuery(id+"F9.boolean.opBoolean","SPLIT",EDGE,{"disambiguationData":[TD([makeQuery(id+"FyEnq1fhFwSBqjL_0.opExtrude","SWEPT_FACE",FACE,{"disambiguationData":[OSD([subQ0])]})])],"derivedFrom":makeQuery(id+"FyEnq1fhFwSBqjL_0.opExtrude","CAP_EDGE",EDGE,{"disambiguationData":[OSD([subQ1])],"isStart":false})});}
            var Q7;
            {var subQ0=sQuery(id+"F0.wireOp",EDGE,"ieqPwXpz-Zkmp-sPIe-4gTk-vNAapPMGIJea.bottom");var subQ1=sQuery(id+"F0.wireOp",EDGE,"ieqPwXpz-Zkmp-sPIe-4gTk-vNAapPMGIJea.left");Q7=makeQuery(id+"F9.boolean.opBoolean","SPLIT",EDGE,{"disambiguationData":[TD([makeQuery(id+"FyEnq1fhFwSBqjL_0.opExtrude","SWEPT_FACE",FACE,{"disambiguationData":[OSD([subQ1])]})])],"derivedFrom":makeQuery(id+"FyEnq1fhFwSBqjL_0.opExtrude","CAP_EDGE",EDGE,{"disambiguationData":[OSD([subQ0])],"isStart":false})});}
            var Q8;
            Q8=makeQuery(id+"F3.opExtrude","CAP_EDGE",EDGE,{"disambiguationData":[OSD([sQuery(id+"F0.wireOp",EDGE,"E1.right")])],"isStart":false});
            var Q9;
            Q9=makeQuery(id+"F3.opExtrude","CAP_EDGE",EDGE,{"disambiguationData":[OSD([sQuery(id+"F0.wireOp",EDGE,"E2.right")])],"isStart":false});
            var Q10;
            {var subQ0=sQuery(id+"F0.wireOp",EDGE,"E23");var subQ1=sQuery(id+"F0.wireOp",EDGE,"E26");Q10=makeQuery(id+"F9.boolean.opBoolean","SPLIT",EDGE,{"disambiguationData":[TD([makeQuery(id+"F8.opExtrude","SWEPT_FACE",FACE,{"disambiguationData":[OSD([subQ1])]})])],"derivedFrom":makeQuery(id+"F8.opExtrude","CAP_EDGE",EDGE,{"disambiguationData":[OSD([subQ0])],"isStart":false})});}
            var Q11;
            {var subQ0=sQuery(id+"F0.wireOp",EDGE,"E26");var subQ1=sQuery(id+"F0.wireOp",EDGE,"E25");Q11=makeQuery(id+"F9.boolean.opBoolean","SPLIT",EDGE,{"disambiguationData":[TD([makeQuery(id+"F8.opExtrude","SWEPT_FACE",FACE,{"disambiguationData":[OSD([subQ0])]})])],"derivedFrom":makeQuery(id+"F8.opExtrude","CAP_EDGE",EDGE,{"disambiguationData":[OSD([subQ1])],"isStart":false})});}
            var Q12;
            {var subQ0=sQuery(id+"F0.wireOp",EDGE,"E25");var subQ1=sQuery(id+"F0.wireOp",EDGE,"E24");Q12=makeQuery(id+"F9.boolean.opBoolean","SPLIT",EDGE,{"disambiguationData":[TD([makeQuery(id+"F8.opExtrude","SWEPT_FACE",FACE,{"disambiguationData":[OSD([subQ1])]})])],"derivedFrom":makeQuery(id+"F8.opExtrude","CAP_EDGE",EDGE,{"disambiguationData":[OSD([subQ0])],"isStart":false})});}
            var Q13;
            {var subQ0=sQuery(id+"F0.wireOp",EDGE,"E23");var subQ1=sQuery(id+"F0.wireOp",EDGE,"E24");Q13=makeQuery(id+"F9.boolean.opBoolean","SPLIT",EDGE,{"disambiguationData":[TD([makeQuery(id+"F8.opExtrude","SWEPT_FACE",FACE,{"disambiguationData":[OSD([subQ1])]})])],"derivedFrom":makeQuery(id+"F8.opExtrude","CAP_EDGE",EDGE,{"disambiguationData":[OSD([subQ0])],"isStart":false})});}
            var Q14;
            {var subQ0=sQuery(id+"F0.wireOp",EDGE,"E29");var subQ1=sQuery(id+"F0.wireOp",EDGE,"E28");Q14=makeQuery(id+"F9.boolean.opBoolean","SPLIT",EDGE,{"disambiguationData":[TD([makeQuery(id+"F8.opExtrude","SWEPT_FACE",FACE,{"disambiguationData":[OSD([subQ1])]})])],"derivedFrom":makeQuery(id+"F8.opExtrude","CAP_EDGE",EDGE,{"disambiguationData":[OSD([subQ0])],"isStart":false})});}
            var Q15;
            {var subQ0=sQuery(id+"F0.wireOp",EDGE,"E27");var subQ1=sQuery(id+"F0.wireOp",EDGE,"E28");Q15=makeQuery(id+"F9.boolean.opBoolean","SPLIT",EDGE,{"disambiguationData":[TD([makeQuery(id+"F8.opExtrude","SWEPT_FACE",FACE,{"disambiguationData":[OSD([subQ1])]})])],"derivedFrom":makeQuery(id+"F8.opExtrude","CAP_EDGE",EDGE,{"disambiguationData":[OSD([subQ0])],"isStart":false})});}
            var Q16;
            {var subQ0=sQuery(id+"F0.wireOp",EDGE,"E30");var subQ1=sQuery(id+"F0.wireOp",EDGE,"E29");Q16=makeQuery(id+"F9.boolean.opBoolean","SPLIT",EDGE,{"disambiguationData":[TD([makeQuery(id+"F8.opExtrude","SWEPT_FACE",FACE,{"disambiguationData":[OSD([subQ0])]})])],"derivedFrom":makeQuery(id+"F8.opExtrude","CAP_EDGE",EDGE,{"disambiguationData":[OSD([subQ1])],"isStart":false})});}
            var Q17;
            {var subQ0=sQuery(id+"F0.wireOp",EDGE,"E27");var subQ1=sQuery(id+"F0.wireOp",EDGE,"E30");Q17=makeQuery(id+"F9.boolean.opBoolean","SPLIT",EDGE,{"disambiguationData":[TD([makeQuery(id+"F8.opExtrude","SWEPT_FACE",FACE,{"disambiguationData":[OSD([subQ1])]})])],"derivedFrom":makeQuery(id+"F8.opExtrude","CAP_EDGE",EDGE,{"disambiguationData":[OSD([subQ0])],"isStart":false})});}
            var Q18;
            Q18=makeQuery(id+"F12.boolean.opBoolean","COPY",EDGE,{"derivedFrom":makeQuery(id+"F12.opExtrude","SWEPT_EDGE",EDGE,{"disambiguationData":[OSD([sQuery(id+"F0.wireOp",EDGE,"E0.bottom"),sQuery(id+"F0.wireOp",EDGE,"E1.bottom"),sQuery(id+"F0.wireOp",EDGE,"E2.bottom"),sQuery(id+"F4.wireOp",EDGE,"E62")])]})});
            var Q19;
            Q19=makeQuery(id+"F12.boolean.opBoolean","COPY",EDGE,{"derivedFrom":makeQuery(id+"F12.opExtrude","SWEPT_EDGE",EDGE,{"disambiguationData":[OSD([sQuery(id+"F0.wireOp",EDGE,"E0.bottom"),sQuery(id+"F0.wireOp",EDGE,"E1.bottom"),sQuery(id+"F0.wireOp",EDGE,"E2.bottom"),sQuery(id+"F4.wireOp",EDGE,"E65")])]})});
            var Q20;
            Q20=makeQuery(id+"F12.boolean.opBoolean","COPY",EDGE,{"derivedFrom":makeQuery(id+"F12.opExtrude","SWEPT_EDGE",EDGE,{"disambiguationData":[OSD([sQuery(id+"F0.wireOp",EDGE,"E0.bottom"),sQuery(id+"F0.wireOp",EDGE,"E1.bottom"),sQuery(id+"F0.wireOp",EDGE,"E2.bottom"),sQuery(id+"F4.wireOp",EDGE,"E63")])]})});
            var Q21;
            Q21=makeQuery(id+"F12.boolean.opBoolean","COPY",EDGE,{"derivedFrom":makeQuery(id+"F12.opExtrude","SWEPT_EDGE",EDGE,{"disambiguationData":[OSD([sQuery(id+"F4.wireOp",EDGE,"E60"),sQuery(id+"F4.wireOp",EDGE,"E62")])]})});
            var Q22;
            Q22=makeQuery(id+"F12.boolean.opBoolean","COPY",EDGE,{"derivedFrom":makeQuery(id+"F12.opExtrude","SWEPT_EDGE",EDGE,{"disambiguationData":[OSD([sQuery(id+"F4.wireOp",EDGE,"E60"),sQuery(id+"F4.wireOp",EDGE,"E66")])]})});
            var Q23;
            {var subQ0=sQuery(id+"F4.wireOp",EDGE,"E66");var subQ1=sQuery(id+"F4.wireOp",EDGE,"E59");Q23=makeQuery(id+"F12.boolean.opBoolean","COPY",EDGE,{"derivedFrom":makeQuery(id+"F12.opExtrude","SWEPT_EDGE",EDGE,{"disambiguationData":[OSD([subQ1,subQ0]),TDD([makeQuery(id+"F4.imprint","INTERSECT",VERTEX,{"disambiguationData":[OD(0.0)],"derivedFrom":[subQ1,subQ0]})])]})});}
            var Q24;
            Q24=makeQuery(id+"F12.boolean.opBoolean","COPY",EDGE,{"derivedFrom":makeQuery(id+"F12.opExtrude","SWEPT_EDGE",EDGE,{"disambiguationData":[OSD([sQuery(id+"F4.wireOp",EDGE,"E59"),sQuery(id+"F4.wireOp",EDGE,"E64")])]})});
            var Q25;
            Q25=makeQuery(id+"F12.boolean.opBoolean","COPY",EDGE,{"derivedFrom":makeQuery(id+"F12.opExtrude","SWEPT_EDGE",EDGE,{"disambiguationData":[OSD([sQuery(id+"F4.wireOp",EDGE,"E59"),sQuery(id+"F4.wireOp",EDGE,"E65")])]})});
            var Q26;
            {var subQ0=sQuery(id+"F4.wireOp",EDGE,"E66");var subQ1=sQuery(id+"F4.wireOp",EDGE,"E59");Q26=makeQuery(id+"F12.boolean.opBoolean","COPY",EDGE,{"derivedFrom":makeQuery(id+"F12.opExtrude","SWEPT_EDGE",EDGE,{"disambiguationData":[OSD([subQ1,subQ0]),TDD([makeQuery(id+"F4.imprint","INTERSECT",VERTEX,{"disambiguationData":[OD(1.0)],"derivedFrom":[subQ1,subQ0]})])]})});}
            var Q27;
            Q27=makeQuery(id+"F12.boolean.opBoolean","COPY",EDGE,{"derivedFrom":makeQuery(id+"F12.opExtrude","SWEPT_EDGE",EDGE,{"disambiguationData":[OSD([sQuery(id+"F4.wireOp",EDGE,"E61"),sQuery(id+"F4.wireOp",EDGE,"E66")])]})});
            var Q28;
            Q28=makeQuery(id+"F12.boolean.opBoolean","COPY",EDGE,{"derivedFrom":makeQuery(id+"F12.opExtrude","SWEPT_EDGE",EDGE,{"disambiguationData":[OSD([sQuery(id+"F4.wireOp",EDGE,"E61"),sQuery(id+"F4.wireOp",EDGE,"E63")])]})});
            var Q29;
            Q29=makeQuery(id+"F12.boolean.opBoolean","COPY",EDGE,{"derivedFrom":makeQuery(id+"F12.opExtrude","SWEPT_EDGE",EDGE,{"disambiguationData":[OSD([sQuery(id+"F0.wireOp",EDGE,"E0.bottom"),sQuery(id+"F0.wireOp",EDGE,"E1.bottom"),sQuery(id+"F0.wireOp",EDGE,"E2.bottom"),sQuery(id+"F4.wireOp",EDGE,"E64")])]})});
            fillet(context, id + "F13", {"entities" : qUnion([Q0, Q1, Q2, Q3, Q4, Q5, Q6, Q7, Q8, Q9, Q10, Q11, Q12, Q13, Q14, Q15, Q16, Q17, Q18, Q19, Q20, Q21, Q22, Q23, Q24, Q25, Q26, Q27, Q28, Q29]), "radius" : 5 * mm, "tangentPropagation" : true, "allowEdgeOverflow" : false});
        }
        {
            var Q0;
            Q0=makeQuery(id+"F8.boolean.opBoolean","INTERSECT",EDGE,{"derivedFrom":[makeQuery(id+"F7.opRevolve","SWEPT_FACE",FACE,{"disambiguationData":[OSD([sQuery(id+"F0.wireOp",EDGE,"E2.right")])]}),makeQuery(id+"F8.opExtrude","SWEPT_FACE",FACE,{"disambiguationData":[OSD([sQuery(id+"F0.wireOp",EDGE,"E26")])]})]});
            var Q1;
            Q1=makeQuery(id+"F8.boolean.opBoolean","INTERSECT",EDGE,{"derivedFrom":[makeQuery(id+"F7.opRevolve","SWEPT_FACE",FACE,{"disambiguationData":[OSD([sQuery(id+"F0.wireOp",EDGE,"E2.right")])]}),makeQuery(id+"F8.opExtrude","SWEPT_FACE",FACE,{"disambiguationData":[OSD([sQuery(id+"F0.wireOp",EDGE,"E24")])]})]});
            var Q2;
            Q2=makeQuery(id+"F8.boolean.opBoolean","INTERSECT",EDGE,{"derivedFrom":[makeQuery(id+"F6.opRevolve","SWEPT_FACE",FACE,{"disambiguationData":[OSD([sQuery(id+"F0.wireOp",EDGE,"E1.right")])]}),makeQuery(id+"F8.opExtrude","SWEPT_FACE",FACE,{"disambiguationData":[OSD([sQuery(id+"F0.wireOp",EDGE,"E28")])]})]});
            var Q3;
            Q3=makeQuery(id+"F8.boolean.opBoolean","INTERSECT",EDGE,{"derivedFrom":[makeQuery(id+"F6.opRevolve","SWEPT_FACE",FACE,{"disambiguationData":[OSD([sQuery(id+"F0.wireOp",EDGE,"E1.right")])]}),makeQuery(id+"F8.opExtrude","SWEPT_FACE",FACE,{"disambiguationData":[OSD([sQuery(id+"F0.wireOp",EDGE,"E30")])]})]});
            fillet(context, id + "F14", {"entities" : qUnion([Q0, Q1, Q2, Q3]), "radius" : 5 * mm, "tangentPropagation" : true, "allowEdgeOverflow" : false});
        }
        {
            var Q0;
            Q0=makeQuery(id+"F3.opExtrude","CAP_EDGE",EDGE,{"disambiguationData":[OSD([sQuery(id+"F0.wireOp",EDGE,"E0.bottom"),sQuery(id+"F0.wireOp",EDGE,"E1.bottom"),sQuery(id+"F0.wireOp",EDGE,"E2.bottom")])],"isStart":false});
            var Q1;
            Q1=makeQuery(id+"F3.opExtrude","SWEPT_EDGE",EDGE,{"disambiguationData":[OSD([sQuery(id+"F0.wireOp",EDGE,"E1.bottom"),sQuery(id+"F0.wireOp",EDGE,"E1.right")])]});
            var Q2;
            Q2=makeQuery(id+"F6.opRevolve","SWEPT_EDGE",EDGE,{"disambiguationData":[OSD([sQuery(id+"F0.wireOp",EDGE,"E1.bottom"),sQuery(id+"F0.wireOp",EDGE,"E1.right")])]});
            var Q3;
            {var subQ0=sQuery(id+"F0.wireOp",EDGE,"E13");var subQ1=sQuery(id+"F0.wireOp",EDGE,"E2.bottom");var subQ2=sQuery(id+"F0.wireOp",EDGE,"E1.bottom");var subQ3=sQuery(id+"F0.wireOp",EDGE,"E0.bottom");Q3=makeQuery(id+"F5.boolean.opBoolean","SPLIT",EDGE,{"disambiguationData":[TD([makeQuery(id+"F2.opExtrude","SWEPT_FACE",FACE,{"disambiguationData":[OSD([subQ0])]})])],"derivedFrom":makeQuery(id+"F2.opExtrude","CAP_EDGE",EDGE,{"disambiguationData":[OSD([subQ3,subQ2,subQ1])],"isStart":false})});}
            var Q4;
            Q4=makeQuery(id+"F5.opExtrude","CAP_EDGE",EDGE,{"disambiguationData":[OSD([sQuery(id+"F4.wireOp",EDGE,"E41")])],"isStart":true});
            var Q5;
            {var subQ0=sQuery(id+"F0.wireOp",EDGE,"E15");var subQ1=sQuery(id+"F0.wireOp",EDGE,"E2.bottom");var subQ2=sQuery(id+"F0.wireOp",EDGE,"E1.bottom");var subQ3=sQuery(id+"F0.wireOp",EDGE,"E0.bottom");Q5=makeQuery(id+"F5.boolean.opBoolean","SPLIT",EDGE,{"disambiguationData":[TD([makeQuery(id+"F2.opExtrude","SWEPT_FACE",FACE,{"disambiguationData":[OSD([subQ0])]})])],"derivedFrom":makeQuery(id+"F2.opExtrude","CAP_EDGE",EDGE,{"disambiguationData":[OSD([subQ3,subQ2,subQ1])],"isStart":false})});}
            var Q6;
            Q6=makeQuery(id+"F7.opRevolve","SWEPT_EDGE",EDGE,{"disambiguationData":[OSD([sQuery(id+"F0.wireOp",EDGE,"E2.bottom"),sQuery(id+"F0.wireOp",EDGE,"E2.right")])]});
            var Q7;
            Q7=makeQuery(id+"F3.opExtrude","SWEPT_EDGE",EDGE,{"disambiguationData":[OSD([sQuery(id+"F0.wireOp",EDGE,"E2.bottom"),sQuery(id+"F0.wireOp",EDGE,"E2.right")])]});
            var Q8;
            Q8=makeQuery(id+"F3.opExtrude","SWEPT_EDGE",EDGE,{"disambiguationData":[OSD([sQuery(id+"F0.wireOp",EDGE,"E1.right"),sQuery(id+"F0.wireOp",EDGE,"E11")])]});
            var Q9;
            Q9=makeQuery(id+"F3.opExtrude","CAP_EDGE",EDGE,{"disambiguationData":[OSD([sQuery(id+"F0.wireOp",EDGE,"E0.top"),sQuery(id+"F0.wireOp",EDGE,"E7"),sQuery(id+"F0.wireOp",EDGE,"E8"),sQuery(id+"F0.wireOp",EDGE,"E9"),sQuery(id+"F0.wireOp",EDGE,"E10"),sQuery(id+"F0.wireOp",EDGE,"E11"),sQuery(id+"F0.wireOp",EDGE,"E12")])],"isStart":false});
            var Q10;
            Q10=makeQuery(id+"F3.opExtrude","SWEPT_EDGE",EDGE,{"disambiguationData":[OSD([sQuery(id+"F0.wireOp",EDGE,"E2.right"),sQuery(id+"F0.wireOp",EDGE,"E12")])]});
            var Q11;
            {var subQ0=sQuery(id+"F0.wireOp",EDGE,"E15");var subQ1=sQuery(id+"F0.wireOp",EDGE,"E10");var subQ2=sQuery(id+"F0.wireOp",EDGE,"E9");var subQ3=sQuery(id+"F0.wireOp",EDGE,"E8");var subQ4=sQuery(id+"F0.wireOp",EDGE,"E7");var subQ5=sQuery(id+"F0.wireOp",EDGE,"E0.top");Q11=makeQuery(id+"F5.boolean.opBoolean","SPLIT",EDGE,{"disambiguationData":[TD([makeQuery(id+"F2.opExtrude","SWEPT_FACE",FACE,{"disambiguationData":[OSD([subQ0])]})])],"derivedFrom":makeQuery(id+"F2.opExtrude","CAP_EDGE",EDGE,{"disambiguationData":[OSD([subQ5,subQ4,subQ3,subQ2,subQ1])],"isStart":false})});}
            var Q12;
            Q12=makeQuery(id+"F5.opExtrude","CAP_EDGE",EDGE,{"disambiguationData":[OSD([sQuery(id+"F4.wireOp",EDGE,"E41")])],"isStart":false});
            var Q13;
            {var subQ0=sQuery(id+"F0.wireOp",EDGE,"E13");var subQ5=sQuery(id+"F0.wireOp",EDGE,"E10");var subQ6=sQuery(id+"F0.wireOp",EDGE,"E9");var subQ7=sQuery(id+"F0.wireOp",EDGE,"E8");var subQ8=sQuery(id+"F0.wireOp",EDGE,"E7");var subQ9=sQuery(id+"F0.wireOp",EDGE,"E0.top");Q13=makeQuery(id+"F5.boolean.opBoolean","SPLIT",EDGE,{"disambiguationData":[TD([makeQuery(id+"F2.opExtrude","SWEPT_FACE",FACE,{"disambiguationData":[OSD([subQ0])]})])],"derivedFrom":makeQuery(id+"F2.opExtrude","CAP_EDGE",EDGE,{"disambiguationData":[OSD([subQ9,subQ8,subQ7,subQ6,subQ5])],"isStart":false})});}
            var Q14;
            Q14=makeQuery(id+"F7.opRevolve","SWEPT_EDGE",EDGE,{"disambiguationData":[OSD([sQuery(id+"F0.wireOp",EDGE,"E2.top"),sQuery(id+"F0.wireOp",EDGE,"E2.right")])]});
            var Q15;
            Q15=makeQuery(id+"F6.opRevolve","SWEPT_EDGE",EDGE,{"disambiguationData":[OSD([sQuery(id+"F0.wireOp",EDGE,"E1.top"),sQuery(id+"F0.wireOp",EDGE,"E1.right")])]});
            var Q16;
            Q16=makeQuery(id+"F8.opExtrude","SWEPT_EDGE",EDGE,{"disambiguationData":[OSD([sQuery(id+"F0.wireOp",EDGE,"E25"),sQuery(id+"F0.wireOp",EDGE,"E26")])]});
            var Q17;
            {var subQ0=sQuery(id+"F0.wireOp",EDGE,"E26");var subQ1=makeQuery(id+"F8.opExtrude","SWEPT_FACE",FACE,{"disambiguationData":[OSD([subQ0])]});var subQ2=sQuery(id+"F0.wireOp",EDGE,"E23");Q17=makeQuery(id+"F13.opFillet","BLEND_EDGE",EDGE,{"blendedFrom":[makeQuery(id+"F9.boolean.opBoolean","SPLIT",EDGE,{"disambiguationData":[TD([subQ1])],"derivedFrom":makeQuery(id+"F8.opExtrude","CAP_EDGE",EDGE,{"disambiguationData":[OSD([subQ2])],"isStart":false})}),subQ1],"blendedInto":[subQ1]});}
            var Q18;
            Q18=makeQuery(id+"F8.opExtrude","SWEPT_EDGE",EDGE,{"disambiguationData":[OSD([sQuery(id+"F0.wireOp",EDGE,"E23"),sQuery(id+"F0.wireOp",EDGE,"E26")])]});
            var Q19;
            Q19=makeQuery(id+"F8.opExtrude","SWEPT_EDGE",EDGE,{"disambiguationData":[OSD([sQuery(id+"F0.wireOp",EDGE,"E29"),sQuery(id+"F0.wireOp",EDGE,"E30")])]});
            var Q20;
            {var subQ0=sQuery(id+"F0.wireOp",EDGE,"E30");var subQ1=makeQuery(id+"F8.opExtrude","SWEPT_FACE",FACE,{"disambiguationData":[OSD([subQ0])]});var subQ2=sQuery(id+"F0.wireOp",EDGE,"E27");Q20=makeQuery(id+"F13.opFillet","BLEND_EDGE",EDGE,{"blendedFrom":[makeQuery(id+"F9.boolean.opBoolean","SPLIT",EDGE,{"disambiguationData":[TD([subQ1])],"derivedFrom":makeQuery(id+"F8.opExtrude","CAP_EDGE",EDGE,{"disambiguationData":[OSD([subQ2])],"isStart":false})}),subQ1],"blendedInto":[subQ1]});}
            var Q21;
            Q21=makeQuery(id+"F8.opExtrude","SWEPT_EDGE",EDGE,{"disambiguationData":[OSD([sQuery(id+"F0.wireOp",EDGE,"E27"),sQuery(id+"F0.wireOp",EDGE,"E30")])]});
            var Q22;
            Q22=makeQuery(id+"F8.opExtrude","SWEPT_EDGE",EDGE,{"disambiguationData":[OSD([sQuery(id+"F0.wireOp",EDGE,"E23"),sQuery(id+"F0.wireOp",EDGE,"E24")])]});
            var Q23;
            {var subQ0=sQuery(id+"F0.wireOp",EDGE,"E24");var subQ1=makeQuery(id+"F8.opExtrude","SWEPT_FACE",FACE,{"disambiguationData":[OSD([subQ0])]});var subQ2=sQuery(id+"F0.wireOp",EDGE,"E25");Q23=makeQuery(id+"F13.opFillet","BLEND_EDGE",EDGE,{"blendedFrom":[makeQuery(id+"F9.boolean.opBoolean","SPLIT",EDGE,{"disambiguationData":[TD([subQ1])],"derivedFrom":makeQuery(id+"F8.opExtrude","CAP_EDGE",EDGE,{"disambiguationData":[OSD([subQ2])],"isStart":false})}),subQ1],"blendedInto":[subQ1]});}
            var Q24;
            Q24=makeQuery(id+"F8.opExtrude","SWEPT_EDGE",EDGE,{"disambiguationData":[OSD([sQuery(id+"F0.wireOp",EDGE,"E24"),sQuery(id+"F0.wireOp",EDGE,"E25")])]});
            var Q25;
            Q25=makeQuery(id+"F8.opExtrude","SWEPT_EDGE",EDGE,{"disambiguationData":[OSD([sQuery(id+"F0.wireOp",EDGE,"E28"),sQuery(id+"F0.wireOp",EDGE,"E29")])]});
            var Q26;
            Q26=makeQuery(id+"F8.opExtrude","SWEPT_EDGE",EDGE,{"disambiguationData":[OSD([sQuery(id+"F0.wireOp",EDGE,"E27"),sQuery(id+"F0.wireOp",EDGE,"E28")])]});
            var Q27;
            {var subQ0=sQuery(id+"F0.wireOp",EDGE,"E28");var subQ1=makeQuery(id+"F8.opExtrude","SWEPT_FACE",FACE,{"disambiguationData":[OSD([subQ0])]});var subQ2=sQuery(id+"F0.wireOp",EDGE,"E29");Q27=makeQuery(id+"F13.opFillet","BLEND_EDGE",EDGE,{"blendedFrom":[makeQuery(id+"F9.boolean.opBoolean","SPLIT",EDGE,{"disambiguationData":[TD([subQ1])],"derivedFrom":makeQuery(id+"F8.opExtrude","CAP_EDGE",EDGE,{"disambiguationData":[OSD([subQ2])],"isStart":false})}),subQ1],"blendedInto":[subQ1]});}
            var Q28;
            {var subQ0=sQuery(id+"F0.wireOp",EDGE,"E10");var subQ1=sQuery(id+"F0.wireOp",EDGE,"E9");var subQ2=sQuery(id+"F0.wireOp",EDGE,"E8");var subQ3=sQuery(id+"F0.wireOp",EDGE,"E7");var subQ4=sQuery(id+"F0.wireOp",EDGE,"E0.top");Q28=makeQuery(id+"F13.opFillet","BLEND_EDGE",EDGE,{"blendedFrom":[makeQuery(id+"F3.opExtrude","CAP_EDGE",EDGE,{"disambiguationData":[OSD([sQuery(id+"F0.wireOp",EDGE,"E2.right")])],"isStart":false}),makeQuery(id+"F5.boolean.opBoolean","MERGE",FACE,{"derivedFrom":[makeQuery(id+"F3.boolean.opBoolean","MERGE",FACE,{"derivedFrom":[makeQuery(id+"F2.boolean.opBoolean","MERGE",FACE,{"derivedFrom":[makeQuery(id+"F1.opExtrude","SWEPT_FACE",FACE,{"disambiguationData":[OSD([subQ4])]}),makeQuery(id+"F2.opExtrude","SWEPT_FACE",FACE,{"disambiguationData":[OSD([subQ4,subQ3,subQ2,subQ1,subQ0])]})]}),makeQuery(id+"F3.opExtrude","SWEPT_FACE",FACE,{"disambiguationData":[OSD([subQ4,subQ3,subQ2,subQ1,subQ0,sQuery(id+"F0.wireOp",EDGE,"E11"),sQuery(id+"F0.wireOp",EDGE,"E12")])]})]}),makeQuery(id+"F5.opExtrude","CAP_FACE",FACE,{"disambiguationData":[OSD([sQuery(id+"F0.wireOp",EDGE,"E0.bottom"),sQuery(id+"F0.wireOp",EDGE,"E1.bottom"),sQuery(id+"F0.wireOp",EDGE,"E2.bottom"),sQuery(id+"F4.wireOp",EDGE,"E37"),sQuery(id+"F4.wireOp",EDGE,"E40"),sQuery(id+"F4.wireOp",EDGE,"E41")])],"isStart":false})]})],"blendedInto":[makeQuery(id+"F5.boolean.opBoolean","MERGE",FACE,{"derivedFrom":[makeQuery(id+"F3.boolean.opBoolean","MERGE",FACE,{"derivedFrom":[makeQuery(id+"F2.boolean.opBoolean","MERGE",FACE,{"derivedFrom":[makeQuery(id+"F1.opExtrude","SWEPT_FACE",FACE,{"disambiguationData":[OSD([subQ4])]}),makeQuery(id+"F2.opExtrude","SWEPT_FACE",FACE,{"disambiguationData":[OSD([subQ4,subQ3,subQ2,subQ1,subQ0])]})]}),makeQuery(id+"F3.opExtrude","SWEPT_FACE",FACE,{"disambiguationData":[OSD([subQ4,subQ3,subQ2,subQ1,subQ0,sQuery(id+"F0.wireOp",EDGE,"E11"),sQuery(id+"F0.wireOp",EDGE,"E12")])]})]}),makeQuery(id+"F5.opExtrude","CAP_FACE",FACE,{"disambiguationData":[OSD([sQuery(id+"F0.wireOp",EDGE,"E0.bottom"),sQuery(id+"F0.wireOp",EDGE,"E1.bottom"),sQuery(id+"F0.wireOp",EDGE,"E2.bottom"),sQuery(id+"F4.wireOp",EDGE,"E37"),sQuery(id+"F4.wireOp",EDGE,"E40"),sQuery(id+"F4.wireOp",EDGE,"E41")])],"isStart":false})]})]});}
            var Q29;
            {var subQ0=sQuery(id+"F0.wireOp",EDGE,"E2.bottom");var subQ1=sQuery(id+"F0.wireOp",EDGE,"E1.bottom");var subQ2=sQuery(id+"F0.wireOp",EDGE,"E0.bottom");Q29=makeQuery(id+"F13.opFillet","BLEND_EDGE",EDGE,{"blendedFrom":[makeQuery(id+"F3.opExtrude","CAP_EDGE",EDGE,{"disambiguationData":[OSD([sQuery(id+"F0.wireOp",EDGE,"E2.right")])],"isStart":false}),makeQuery(id+"F7.boolean.opBoolean","MERGE",FACE,{"derivedFrom":[makeQuery(id+"F6.boolean.opBoolean","MERGE",FACE,{"derivedFrom":[makeQuery(id+"F5.boolean.opBoolean","MERGE",FACE,{"derivedFrom":[makeQuery(id+"F3.boolean.opBoolean","MERGE",FACE,{"derivedFrom":[makeQuery(id+"F2.boolean.opBoolean","MERGE",FACE,{"derivedFrom":[makeQuery(id+"F1.opExtrude","SWEPT_FACE",FACE,{"disambiguationData":[OSD([subQ2,subQ1,subQ0])]}),makeQuery(id+"F2.opExtrude","SWEPT_FACE",FACE,{"disambiguationData":[OSD([subQ2,subQ1,subQ0])]})]}),makeQuery(id+"F3.opExtrude","SWEPT_FACE",FACE,{"disambiguationData":[OSD([subQ2,subQ1,subQ0])]})]}),makeQuery(id+"F5.opExtrude","CAP_FACE",FACE,{"disambiguationData":[OSD([subQ2,subQ1,subQ0,sQuery(id+"F4.wireOp",EDGE,"E37"),sQuery(id+"F4.wireOp",EDGE,"E40"),sQuery(id+"F4.wireOp",EDGE,"E41")])],"isStart":true})]}),makeQuery(id+"F6.opRevolve","SWEPT_FACE",FACE,{"disambiguationData":[OSD([subQ1])]})]}),makeQuery(id+"F7.opRevolve","SWEPT_FACE",FACE,{"disambiguationData":[OSD([subQ0])]})]})],"blendedInto":[makeQuery(id+"F7.boolean.opBoolean","MERGE",FACE,{"derivedFrom":[makeQuery(id+"F6.boolean.opBoolean","MERGE",FACE,{"derivedFrom":[makeQuery(id+"F5.boolean.opBoolean","MERGE",FACE,{"derivedFrom":[makeQuery(id+"F3.boolean.opBoolean","MERGE",FACE,{"derivedFrom":[makeQuery(id+"F2.boolean.opBoolean","MERGE",FACE,{"derivedFrom":[makeQuery(id+"F1.opExtrude","SWEPT_FACE",FACE,{"disambiguationData":[OSD([subQ2,subQ1,subQ0])]}),makeQuery(id+"F2.opExtrude","SWEPT_FACE",FACE,{"disambiguationData":[OSD([subQ2,subQ1,subQ0])]})]}),makeQuery(id+"F3.opExtrude","SWEPT_FACE",FACE,{"disambiguationData":[OSD([subQ2,subQ1,subQ0])]})]}),makeQuery(id+"F5.opExtrude","CAP_FACE",FACE,{"disambiguationData":[OSD([subQ2,subQ1,subQ0,sQuery(id+"F4.wireOp",EDGE,"E37"),sQuery(id+"F4.wireOp",EDGE,"E40"),sQuery(id+"F4.wireOp",EDGE,"E41")])],"isStart":true})]}),makeQuery(id+"F6.opRevolve","SWEPT_FACE",FACE,{"disambiguationData":[OSD([subQ1])]})]}),makeQuery(id+"F7.opRevolve","SWEPT_FACE",FACE,{"disambiguationData":[OSD([subQ0])]})]})]});}
            var Q30;
            {var subQ0=sQuery(id+"F0.wireOp",EDGE,"E10");var subQ1=sQuery(id+"F0.wireOp",EDGE,"E9");var subQ2=sQuery(id+"F0.wireOp",EDGE,"E8");var subQ3=sQuery(id+"F0.wireOp",EDGE,"E7");var subQ4=sQuery(id+"F0.wireOp",EDGE,"E0.top");Q30=makeQuery(id+"F13.opFillet","BLEND_EDGE",EDGE,{"blendedFrom":[makeQuery(id+"F3.opExtrude","CAP_EDGE",EDGE,{"disambiguationData":[OSD([sQuery(id+"F0.wireOp",EDGE,"E1.right")])],"isStart":false}),makeQuery(id+"F5.boolean.opBoolean","MERGE",FACE,{"derivedFrom":[makeQuery(id+"F3.boolean.opBoolean","MERGE",FACE,{"derivedFrom":[makeQuery(id+"F2.boolean.opBoolean","MERGE",FACE,{"derivedFrom":[makeQuery(id+"F1.opExtrude","SWEPT_FACE",FACE,{"disambiguationData":[OSD([subQ4])]}),makeQuery(id+"F2.opExtrude","SWEPT_FACE",FACE,{"disambiguationData":[OSD([subQ4,subQ3,subQ2,subQ1,subQ0])]})]}),makeQuery(id+"F3.opExtrude","SWEPT_FACE",FACE,{"disambiguationData":[OSD([subQ4,subQ3,subQ2,subQ1,subQ0,sQuery(id+"F0.wireOp",EDGE,"E11"),sQuery(id+"F0.wireOp",EDGE,"E12")])]})]}),makeQuery(id+"F5.opExtrude","CAP_FACE",FACE,{"disambiguationData":[OSD([sQuery(id+"F0.wireOp",EDGE,"E0.bottom"),sQuery(id+"F0.wireOp",EDGE,"E1.bottom"),sQuery(id+"F0.wireOp",EDGE,"E2.bottom"),sQuery(id+"F4.wireOp",EDGE,"E37"),sQuery(id+"F4.wireOp",EDGE,"E40"),sQuery(id+"F4.wireOp",EDGE,"E41")])],"isStart":false})]})],"blendedInto":[makeQuery(id+"F5.boolean.opBoolean","MERGE",FACE,{"derivedFrom":[makeQuery(id+"F3.boolean.opBoolean","MERGE",FACE,{"derivedFrom":[makeQuery(id+"F2.boolean.opBoolean","MERGE",FACE,{"derivedFrom":[makeQuery(id+"F1.opExtrude","SWEPT_FACE",FACE,{"disambiguationData":[OSD([subQ4])]}),makeQuery(id+"F2.opExtrude","SWEPT_FACE",FACE,{"disambiguationData":[OSD([subQ4,subQ3,subQ2,subQ1,subQ0])]})]}),makeQuery(id+"F3.opExtrude","SWEPT_FACE",FACE,{"disambiguationData":[OSD([subQ4,subQ3,subQ2,subQ1,subQ0,sQuery(id+"F0.wireOp",EDGE,"E11"),sQuery(id+"F0.wireOp",EDGE,"E12")])]})]}),makeQuery(id+"F5.opExtrude","CAP_FACE",FACE,{"disambiguationData":[OSD([sQuery(id+"F0.wireOp",EDGE,"E0.bottom"),sQuery(id+"F0.wireOp",EDGE,"E1.bottom"),sQuery(id+"F0.wireOp",EDGE,"E2.bottom"),sQuery(id+"F4.wireOp",EDGE,"E37"),sQuery(id+"F4.wireOp",EDGE,"E40"),sQuery(id+"F4.wireOp",EDGE,"E41")])],"isStart":false})]})]});}
            var Q31;
            {var subQ0=sQuery(id+"F0.wireOp",EDGE,"E2.bottom");var subQ1=sQuery(id+"F0.wireOp",EDGE,"E1.bottom");var subQ2=sQuery(id+"F0.wireOp",EDGE,"E0.bottom");Q31=makeQuery(id+"F13.opFillet","BLEND_EDGE",EDGE,{"blendedFrom":[makeQuery(id+"F3.opExtrude","CAP_EDGE",EDGE,{"disambiguationData":[OSD([sQuery(id+"F0.wireOp",EDGE,"E1.right")])],"isStart":false}),makeQuery(id+"F7.boolean.opBoolean","MERGE",FACE,{"derivedFrom":[makeQuery(id+"F6.boolean.opBoolean","MERGE",FACE,{"derivedFrom":[makeQuery(id+"F5.boolean.opBoolean","MERGE",FACE,{"derivedFrom":[makeQuery(id+"F3.boolean.opBoolean","MERGE",FACE,{"derivedFrom":[makeQuery(id+"F2.boolean.opBoolean","MERGE",FACE,{"derivedFrom":[makeQuery(id+"F1.opExtrude","SWEPT_FACE",FACE,{"disambiguationData":[OSD([subQ2,subQ1,subQ0])]}),makeQuery(id+"F2.opExtrude","SWEPT_FACE",FACE,{"disambiguationData":[OSD([subQ2,subQ1,subQ0])]})]}),makeQuery(id+"F3.opExtrude","SWEPT_FACE",FACE,{"disambiguationData":[OSD([subQ2,subQ1,subQ0])]})]}),makeQuery(id+"F5.opExtrude","CAP_FACE",FACE,{"disambiguationData":[OSD([subQ2,subQ1,subQ0,sQuery(id+"F4.wireOp",EDGE,"E37"),sQuery(id+"F4.wireOp",EDGE,"E40"),sQuery(id+"F4.wireOp",EDGE,"E41")])],"isStart":true})]}),makeQuery(id+"F6.opRevolve","SWEPT_FACE",FACE,{"disambiguationData":[OSD([subQ1])]})]}),makeQuery(id+"F7.opRevolve","SWEPT_FACE",FACE,{"disambiguationData":[OSD([subQ0])]})]})],"blendedInto":[makeQuery(id+"F7.boolean.opBoolean","MERGE",FACE,{"derivedFrom":[makeQuery(id+"F6.boolean.opBoolean","MERGE",FACE,{"derivedFrom":[makeQuery(id+"F5.boolean.opBoolean","MERGE",FACE,{"derivedFrom":[makeQuery(id+"F3.boolean.opBoolean","MERGE",FACE,{"derivedFrom":[makeQuery(id+"F2.boolean.opBoolean","MERGE",FACE,{"derivedFrom":[makeQuery(id+"F1.opExtrude","SWEPT_FACE",FACE,{"disambiguationData":[OSD([subQ2,subQ1,subQ0])]}),makeQuery(id+"F2.opExtrude","SWEPT_FACE",FACE,{"disambiguationData":[OSD([subQ2,subQ1,subQ0])]})]}),makeQuery(id+"F3.opExtrude","SWEPT_FACE",FACE,{"disambiguationData":[OSD([subQ2,subQ1,subQ0])]})]}),makeQuery(id+"F5.opExtrude","CAP_FACE",FACE,{"disambiguationData":[OSD([subQ2,subQ1,subQ0,sQuery(id+"F4.wireOp",EDGE,"E37"),sQuery(id+"F4.wireOp",EDGE,"E40"),sQuery(id+"F4.wireOp",EDGE,"E41")])],"isStart":true})]}),makeQuery(id+"F6.opRevolve","SWEPT_FACE",FACE,{"disambiguationData":[OSD([subQ1])]})]}),makeQuery(id+"F7.opRevolve","SWEPT_FACE",FACE,{"disambiguationData":[OSD([subQ0])]})]})]});}
            var Q32;
            Q32=makeQuery(id+"F9.boolean.opBoolean","COPY",EDGE,{"derivedFrom":makeQuery(id+"F9.opExtrude","CAP_EDGE",EDGE,{"disambiguationData":[OSD([sQuery(id+"F4.wireOp",EDGE,"E33")])],"isStart":true})});
            var Q33;
            {var subQ0=sQuery(id+"F0.wireOp",EDGE,"E10");var subQ1=sQuery(id+"F0.wireOp",EDGE,"E9");var subQ2=sQuery(id+"F0.wireOp",EDGE,"E8");var subQ3=sQuery(id+"F0.wireOp",EDGE,"E7");var subQ4=sQuery(id+"F0.wireOp",EDGE,"E0.top");Q33=makeQuery(id+"F9.boolean.opBoolean","INTERSECT",EDGE,{"derivedFrom":[makeQuery(id+"F5.boolean.opBoolean","MERGE",FACE,{"derivedFrom":[makeQuery(id+"F3.boolean.opBoolean","MERGE",FACE,{"derivedFrom":[makeQuery(id+"F2.boolean.opBoolean","MERGE",FACE,{"derivedFrom":[makeQuery(id+"F1.opExtrude","SWEPT_FACE",FACE,{"disambiguationData":[OSD([subQ4])]}),makeQuery(id+"F2.opExtrude","SWEPT_FACE",FACE,{"disambiguationData":[OSD([subQ4,subQ3,subQ2,subQ1,subQ0])]})]}),makeQuery(id+"F3.opExtrude","SWEPT_FACE",FACE,{"disambiguationData":[OSD([subQ4,subQ3,subQ2,subQ1,subQ0,sQuery(id+"F0.wireOp",EDGE,"E11"),sQuery(id+"F0.wireOp",EDGE,"E12")])]})]}),makeQuery(id+"F5.opExtrude","CAP_FACE",FACE,{"disambiguationData":[OSD([sQuery(id+"F0.wireOp",EDGE,"E0.bottom"),sQuery(id+"F0.wireOp",EDGE,"E1.bottom"),sQuery(id+"F0.wireOp",EDGE,"E2.bottom"),sQuery(id+"F4.wireOp",EDGE,"E37"),sQuery(id+"F4.wireOp",EDGE,"E40"),sQuery(id+"F4.wireOp",EDGE,"E41")])],"isStart":false})]}),makeQuery(id+"F9.opExtrude","SWEPT_FACE",FACE,{"disambiguationData":[OSD([sQuery(id+"F4.wireOp",EDGE,"E33")])]})]});}
            var Q34;
            {var subQ0=makeQuery(id+"F7.opRevolve","SWEPT_FACE",FACE,{"disambiguationData":[OSD([sQuery(id+"F0.wireOp",EDGE,"E2.right")])]});var subQ1=sQuery(id+"F0.wireOp",EDGE,"E26");var subQ2=makeQuery(id+"F8.opExtrude","SWEPT_FACE",FACE,{"disambiguationData":[OSD([subQ1])]});var subQ3=sQuery(id+"F0.wireOp",EDGE,"E23");Q34=makeQuery(id+"F14.opFillet","BLEND_EDGE",EDGE,{"blendedFrom":[makeQuery(id+"F8.boolean.opBoolean","INTERSECT",EDGE,{"derivedFrom":[subQ0,subQ2]}),makeQuery(id+"F9.boolean.opBoolean","SPLIT",FACE,{"disambiguationData":[TD([subQ2])],"derivedFrom":makeQuery(id+"F8.opExtrude","SWEPT_FACE",FACE,{"disambiguationData":[OSD([subQ3])]})})],"blendedInto":[makeQuery(id+"F9.boolean.opBoolean","SPLIT",FACE,{"disambiguationData":[TD([subQ2])],"derivedFrom":makeQuery(id+"F8.opExtrude","SWEPT_FACE",FACE,{"disambiguationData":[OSD([subQ3])]})})]});}
            var Q35;
            {var subQ0=makeQuery(id+"F7.opRevolve","SWEPT_FACE",FACE,{"disambiguationData":[OSD([sQuery(id+"F0.wireOp",EDGE,"E2.right")])]});var subQ1=sQuery(id+"F0.wireOp",EDGE,"E26");var subQ2=makeQuery(id+"F8.opExtrude","SWEPT_FACE",FACE,{"disambiguationData":[OSD([subQ1])]});var subQ3=sQuery(id+"F0.wireOp",EDGE,"E25");Q35=makeQuery(id+"F14.opFillet","BLEND_EDGE",EDGE,{"blendedFrom":[makeQuery(id+"F8.boolean.opBoolean","INTERSECT",EDGE,{"derivedFrom":[subQ0,subQ2]}),makeQuery(id+"F9.boolean.opBoolean","SPLIT",FACE,{"disambiguationData":[TD([subQ2])],"derivedFrom":makeQuery(id+"F8.opExtrude","SWEPT_FACE",FACE,{"disambiguationData":[OSD([subQ3])]})})],"blendedInto":[makeQuery(id+"F9.boolean.opBoolean","SPLIT",FACE,{"disambiguationData":[TD([subQ2])],"derivedFrom":makeQuery(id+"F8.opExtrude","SWEPT_FACE",FACE,{"disambiguationData":[OSD([subQ3])]})})]});}
            var Q36;
            {var subQ0=makeQuery(id+"F7.opRevolve","SWEPT_FACE",FACE,{"disambiguationData":[OSD([sQuery(id+"F0.wireOp",EDGE,"E2.right")])]});var subQ1=sQuery(id+"F0.wireOp",EDGE,"E24");var subQ2=sQuery(id+"F0.wireOp",EDGE,"E23");var subQ3=makeQuery(id+"F8.opExtrude","SWEPT_FACE",FACE,{"disambiguationData":[OSD([subQ1])]});Q36=makeQuery(id+"F14.opFillet","BLEND_EDGE",EDGE,{"blendedFrom":[makeQuery(id+"F8.boolean.opBoolean","INTERSECT",EDGE,{"derivedFrom":[subQ0,subQ3]}),makeQuery(id+"F9.boolean.opBoolean","SPLIT",FACE,{"disambiguationData":[TD([subQ3])],"derivedFrom":makeQuery(id+"F8.opExtrude","SWEPT_FACE",FACE,{"disambiguationData":[OSD([subQ2])]})})],"blendedInto":[makeQuery(id+"F9.boolean.opBoolean","SPLIT",FACE,{"disambiguationData":[TD([subQ3])],"derivedFrom":makeQuery(id+"F8.opExtrude","SWEPT_FACE",FACE,{"disambiguationData":[OSD([subQ2])]})})]});}
            var Q37;
            {var subQ0=makeQuery(id+"F7.opRevolve","SWEPT_FACE",FACE,{"disambiguationData":[OSD([sQuery(id+"F0.wireOp",EDGE,"E2.right")])]});var subQ1=sQuery(id+"F0.wireOp",EDGE,"E25");var subQ2=sQuery(id+"F0.wireOp",EDGE,"E24");var subQ3=makeQuery(id+"F8.opExtrude","SWEPT_FACE",FACE,{"disambiguationData":[OSD([subQ2])]});Q37=makeQuery(id+"F14.opFillet","BLEND_EDGE",EDGE,{"blendedFrom":[makeQuery(id+"F8.boolean.opBoolean","INTERSECT",EDGE,{"derivedFrom":[subQ0,subQ3]}),makeQuery(id+"F9.boolean.opBoolean","SPLIT",FACE,{"disambiguationData":[TD([subQ3])],"derivedFrom":makeQuery(id+"F8.opExtrude","SWEPT_FACE",FACE,{"disambiguationData":[OSD([subQ1])]})})],"blendedInto":[makeQuery(id+"F9.boolean.opBoolean","SPLIT",FACE,{"disambiguationData":[TD([subQ3])],"derivedFrom":makeQuery(id+"F8.opExtrude","SWEPT_FACE",FACE,{"disambiguationData":[OSD([subQ1])]})})]});}
            var Q38;
            {var subQ0=makeQuery(id+"F6.opRevolve","SWEPT_FACE",FACE,{"disambiguationData":[OSD([sQuery(id+"F0.wireOp",EDGE,"E1.right")])]});var subQ1=sQuery(id+"F0.wireOp",EDGE,"E28");var subQ2=sQuery(id+"F0.wireOp",EDGE,"E27");var subQ3=makeQuery(id+"F8.opExtrude","SWEPT_FACE",FACE,{"disambiguationData":[OSD([subQ1])]});Q38=makeQuery(id+"F14.opFillet","BLEND_EDGE",EDGE,{"blendedFrom":[makeQuery(id+"F8.boolean.opBoolean","INTERSECT",EDGE,{"derivedFrom":[subQ0,subQ3]}),makeQuery(id+"F9.boolean.opBoolean","SPLIT",FACE,{"disambiguationData":[TD([subQ3])],"derivedFrom":makeQuery(id+"F8.opExtrude","SWEPT_FACE",FACE,{"disambiguationData":[OSD([subQ2])]})})],"blendedInto":[makeQuery(id+"F9.boolean.opBoolean","SPLIT",FACE,{"disambiguationData":[TD([subQ3])],"derivedFrom":makeQuery(id+"F8.opExtrude","SWEPT_FACE",FACE,{"disambiguationData":[OSD([subQ2])]})})]});}
            var Q39;
            {var subQ0=makeQuery(id+"F6.opRevolve","SWEPT_FACE",FACE,{"disambiguationData":[OSD([sQuery(id+"F0.wireOp",EDGE,"E1.right")])]});var subQ1=sQuery(id+"F0.wireOp",EDGE,"E29");var subQ2=sQuery(id+"F0.wireOp",EDGE,"E28");var subQ3=makeQuery(id+"F8.opExtrude","SWEPT_FACE",FACE,{"disambiguationData":[OSD([subQ2])]});Q39=makeQuery(id+"F14.opFillet","BLEND_EDGE",EDGE,{"blendedFrom":[makeQuery(id+"F8.boolean.opBoolean","INTERSECT",EDGE,{"derivedFrom":[subQ0,subQ3]}),makeQuery(id+"F9.boolean.opBoolean","SPLIT",FACE,{"disambiguationData":[TD([subQ3])],"derivedFrom":makeQuery(id+"F8.opExtrude","SWEPT_FACE",FACE,{"disambiguationData":[OSD([subQ1])]})})],"blendedInto":[makeQuery(id+"F9.boolean.opBoolean","SPLIT",FACE,{"disambiguationData":[TD([subQ3])],"derivedFrom":makeQuery(id+"F8.opExtrude","SWEPT_FACE",FACE,{"disambiguationData":[OSD([subQ1])]})})]});}
            var Q40;
            {var subQ0=makeQuery(id+"F6.opRevolve","SWEPT_FACE",FACE,{"disambiguationData":[OSD([sQuery(id+"F0.wireOp",EDGE,"E1.right")])]});var subQ1=sQuery(id+"F0.wireOp",EDGE,"E30");var subQ2=sQuery(id+"F0.wireOp",EDGE,"E27");var subQ3=makeQuery(id+"F8.opExtrude","SWEPT_FACE",FACE,{"disambiguationData":[OSD([subQ1])]});Q40=makeQuery(id+"F14.opFillet","BLEND_EDGE",EDGE,{"blendedFrom":[makeQuery(id+"F8.boolean.opBoolean","INTERSECT",EDGE,{"derivedFrom":[subQ0,subQ3]}),makeQuery(id+"F9.boolean.opBoolean","SPLIT",FACE,{"disambiguationData":[TD([subQ3])],"derivedFrom":makeQuery(id+"F8.opExtrude","SWEPT_FACE",FACE,{"disambiguationData":[OSD([subQ2])]})})],"blendedInto":[makeQuery(id+"F9.boolean.opBoolean","SPLIT",FACE,{"disambiguationData":[TD([subQ3])],"derivedFrom":makeQuery(id+"F8.opExtrude","SWEPT_FACE",FACE,{"disambiguationData":[OSD([subQ2])]})})]});}
            var Q41;
            {var subQ0=makeQuery(id+"F6.opRevolve","SWEPT_FACE",FACE,{"disambiguationData":[OSD([sQuery(id+"F0.wireOp",EDGE,"E1.right")])]});var subQ1=sQuery(id+"F0.wireOp",EDGE,"E30");var subQ2=sQuery(id+"F0.wireOp",EDGE,"E29");var subQ3=makeQuery(id+"F8.opExtrude","SWEPT_FACE",FACE,{"disambiguationData":[OSD([subQ1])]});Q41=makeQuery(id+"F14.opFillet","BLEND_EDGE",EDGE,{"blendedFrom":[makeQuery(id+"F8.boolean.opBoolean","INTERSECT",EDGE,{"derivedFrom":[subQ0,subQ3]}),makeQuery(id+"F9.boolean.opBoolean","SPLIT",FACE,{"disambiguationData":[TD([subQ3])],"derivedFrom":makeQuery(id+"F8.opExtrude","SWEPT_FACE",FACE,{"disambiguationData":[OSD([subQ2])]})})],"blendedInto":[makeQuery(id+"F9.boolean.opBoolean","SPLIT",FACE,{"disambiguationData":[TD([subQ3])],"derivedFrom":makeQuery(id+"F8.opExtrude","SWEPT_FACE",FACE,{"disambiguationData":[OSD([subQ2])]})})]});}
            var Q42;
            {var subQ0=sQuery(id+"F0.wireOp",EDGE,"E2.bottom");var subQ1=sQuery(id+"F0.wireOp",EDGE,"E1.bottom");var subQ2=sQuery(id+"F0.wireOp",EDGE,"E0.bottom");Q42=makeQuery(id+"F13.opFillet","BLEND_EDGE",EDGE,{"blendedFrom":[makeQuery(id+"F12.boolean.opBoolean","COPY",EDGE,{"derivedFrom":makeQuery(id+"F12.opExtrude","SWEPT_EDGE",EDGE,{"disambiguationData":[OSD([subQ2,subQ1,subQ0,sQuery(id+"F4.wireOp",EDGE,"E62")])]})}),makeQuery(id+"F7.boolean.opBoolean","MERGE",FACE,{"derivedFrom":[makeQuery(id+"F6.boolean.opBoolean","MERGE",FACE,{"derivedFrom":[makeQuery(id+"F5.boolean.opBoolean","MERGE",FACE,{"derivedFrom":[makeQuery(id+"F3.boolean.opBoolean","MERGE",FACE,{"derivedFrom":[makeQuery(id+"F2.boolean.opBoolean","MERGE",FACE,{"derivedFrom":[makeQuery(id+"F1.opExtrude","SWEPT_FACE",FACE,{"disambiguationData":[OSD([subQ2,subQ1,subQ0])]}),makeQuery(id+"F2.opExtrude","SWEPT_FACE",FACE,{"disambiguationData":[OSD([subQ2,subQ1,subQ0])]})]}),makeQuery(id+"F3.opExtrude","SWEPT_FACE",FACE,{"disambiguationData":[OSD([subQ2,subQ1,subQ0])]})]}),makeQuery(id+"F5.opExtrude","CAP_FACE",FACE,{"disambiguationData":[OSD([subQ2,subQ1,subQ0,sQuery(id+"F4.wireOp",EDGE,"E37"),sQuery(id+"F4.wireOp",EDGE,"E40"),sQuery(id+"F4.wireOp",EDGE,"E41")])],"isStart":true})]}),makeQuery(id+"F6.opRevolve","SWEPT_FACE",FACE,{"disambiguationData":[OSD([subQ1])]})]}),makeQuery(id+"F7.opRevolve","SWEPT_FACE",FACE,{"disambiguationData":[OSD([subQ0])]})]})],"blendedInto":[makeQuery(id+"F7.boolean.opBoolean","MERGE",FACE,{"derivedFrom":[makeQuery(id+"F6.boolean.opBoolean","MERGE",FACE,{"derivedFrom":[makeQuery(id+"F5.boolean.opBoolean","MERGE",FACE,{"derivedFrom":[makeQuery(id+"F3.boolean.opBoolean","MERGE",FACE,{"derivedFrom":[makeQuery(id+"F2.boolean.opBoolean","MERGE",FACE,{"derivedFrom":[makeQuery(id+"F1.opExtrude","SWEPT_FACE",FACE,{"disambiguationData":[OSD([subQ2,subQ1,subQ0])]}),makeQuery(id+"F2.opExtrude","SWEPT_FACE",FACE,{"disambiguationData":[OSD([subQ2,subQ1,subQ0])]})]}),makeQuery(id+"F3.opExtrude","SWEPT_FACE",FACE,{"disambiguationData":[OSD([subQ2,subQ1,subQ0])]})]}),makeQuery(id+"F5.opExtrude","CAP_FACE",FACE,{"disambiguationData":[OSD([subQ2,subQ1,subQ0,sQuery(id+"F4.wireOp",EDGE,"E37"),sQuery(id+"F4.wireOp",EDGE,"E40"),sQuery(id+"F4.wireOp",EDGE,"E41")])],"isStart":true})]}),makeQuery(id+"F6.opRevolve","SWEPT_FACE",FACE,{"disambiguationData":[OSD([subQ1])]})]}),makeQuery(id+"F7.opRevolve","SWEPT_FACE",FACE,{"disambiguationData":[OSD([subQ0])]})]})]});}
            var Q43;
            Q43=makeQuery(id+"F12.boolean.opBoolean","COPY",EDGE,{"derivedFrom":makeQuery(id+"F12.opExtrude","CAP_EDGE",EDGE,{"disambiguationData":[OSD([sQuery(id+"F4.wireOp",EDGE,"E62")])],"isStart":true})});
            var Q44;
            {var subQ0=sQuery(id+"F0.wireOp",EDGE,"E2.bottom");var subQ1=sQuery(id+"F0.wireOp",EDGE,"E1.bottom");var subQ2=sQuery(id+"F0.wireOp",EDGE,"E0.bottom");Q44=makeQuery(id+"F13.opFillet","BLEND_EDGE",EDGE,{"blendedFrom":[makeQuery(id+"F12.boolean.opBoolean","COPY",EDGE,{"derivedFrom":makeQuery(id+"F12.opExtrude","SWEPT_EDGE",EDGE,{"disambiguationData":[OSD([sQuery(id+"F4.wireOp",EDGE,"E60"),sQuery(id+"F4.wireOp",EDGE,"E62")])]})}),makeQuery(id+"F7.boolean.opBoolean","MERGE",FACE,{"derivedFrom":[makeQuery(id+"F6.boolean.opBoolean","MERGE",FACE,{"derivedFrom":[makeQuery(id+"F5.boolean.opBoolean","MERGE",FACE,{"derivedFrom":[makeQuery(id+"F3.boolean.opBoolean","MERGE",FACE,{"derivedFrom":[makeQuery(id+"F2.boolean.opBoolean","MERGE",FACE,{"derivedFrom":[makeQuery(id+"F1.opExtrude","SWEPT_FACE",FACE,{"disambiguationData":[OSD([subQ2,subQ1,subQ0])]}),makeQuery(id+"F2.opExtrude","SWEPT_FACE",FACE,{"disambiguationData":[OSD([subQ2,subQ1,subQ0])]})]}),makeQuery(id+"F3.opExtrude","SWEPT_FACE",FACE,{"disambiguationData":[OSD([subQ2,subQ1,subQ0])]})]}),makeQuery(id+"F5.opExtrude","CAP_FACE",FACE,{"disambiguationData":[OSD([subQ2,subQ1,subQ0,sQuery(id+"F4.wireOp",EDGE,"E37"),sQuery(id+"F4.wireOp",EDGE,"E40"),sQuery(id+"F4.wireOp",EDGE,"E41")])],"isStart":true})]}),makeQuery(id+"F6.opRevolve","SWEPT_FACE",FACE,{"disambiguationData":[OSD([subQ1])]})]}),makeQuery(id+"F7.opRevolve","SWEPT_FACE",FACE,{"disambiguationData":[OSD([subQ0])]})]})],"blendedInto":[makeQuery(id+"F7.boolean.opBoolean","MERGE",FACE,{"derivedFrom":[makeQuery(id+"F6.boolean.opBoolean","MERGE",FACE,{"derivedFrom":[makeQuery(id+"F5.boolean.opBoolean","MERGE",FACE,{"derivedFrom":[makeQuery(id+"F3.boolean.opBoolean","MERGE",FACE,{"derivedFrom":[makeQuery(id+"F2.boolean.opBoolean","MERGE",FACE,{"derivedFrom":[makeQuery(id+"F1.opExtrude","SWEPT_FACE",FACE,{"disambiguationData":[OSD([subQ2,subQ1,subQ0])]}),makeQuery(id+"F2.opExtrude","SWEPT_FACE",FACE,{"disambiguationData":[OSD([subQ2,subQ1,subQ0])]})]}),makeQuery(id+"F3.opExtrude","SWEPT_FACE",FACE,{"disambiguationData":[OSD([subQ2,subQ1,subQ0])]})]}),makeQuery(id+"F5.opExtrude","CAP_FACE",FACE,{"disambiguationData":[OSD([subQ2,subQ1,subQ0,sQuery(id+"F4.wireOp",EDGE,"E37"),sQuery(id+"F4.wireOp",EDGE,"E40"),sQuery(id+"F4.wireOp",EDGE,"E41")])],"isStart":true})]}),makeQuery(id+"F6.opRevolve","SWEPT_FACE",FACE,{"disambiguationData":[OSD([subQ1])]})]}),makeQuery(id+"F7.opRevolve","SWEPT_FACE",FACE,{"disambiguationData":[OSD([subQ0])]})]})]});}
            var Q45;
            Q45=makeQuery(id+"F12.boolean.opBoolean","COPY",EDGE,{"derivedFrom":makeQuery(id+"F12.opExtrude","CAP_EDGE",EDGE,{"disambiguationData":[OSD([sQuery(id+"F4.wireOp",EDGE,"E60")])],"isStart":true})});
            var Q46;
            {var subQ0=sQuery(id+"F0.wireOp",EDGE,"E2.bottom");var subQ1=sQuery(id+"F0.wireOp",EDGE,"E1.bottom");var subQ2=sQuery(id+"F0.wireOp",EDGE,"E0.bottom");Q46=makeQuery(id+"F13.opFillet","BLEND_EDGE",EDGE,{"blendedFrom":[makeQuery(id+"F12.boolean.opBoolean","COPY",EDGE,{"derivedFrom":makeQuery(id+"F12.opExtrude","SWEPT_EDGE",EDGE,{"disambiguationData":[OSD([sQuery(id+"F4.wireOp",EDGE,"E60"),sQuery(id+"F4.wireOp",EDGE,"E66")])]})}),makeQuery(id+"F7.boolean.opBoolean","MERGE",FACE,{"derivedFrom":[makeQuery(id+"F6.boolean.opBoolean","MERGE",FACE,{"derivedFrom":[makeQuery(id+"F5.boolean.opBoolean","MERGE",FACE,{"derivedFrom":[makeQuery(id+"F3.boolean.opBoolean","MERGE",FACE,{"derivedFrom":[makeQuery(id+"F2.boolean.opBoolean","MERGE",FACE,{"derivedFrom":[makeQuery(id+"F1.opExtrude","SWEPT_FACE",FACE,{"disambiguationData":[OSD([subQ2,subQ1,subQ0])]}),makeQuery(id+"F2.opExtrude","SWEPT_FACE",FACE,{"disambiguationData":[OSD([subQ2,subQ1,subQ0])]})]}),makeQuery(id+"F3.opExtrude","SWEPT_FACE",FACE,{"disambiguationData":[OSD([subQ2,subQ1,subQ0])]})]}),makeQuery(id+"F5.opExtrude","CAP_FACE",FACE,{"disambiguationData":[OSD([subQ2,subQ1,subQ0,sQuery(id+"F4.wireOp",EDGE,"E37"),sQuery(id+"F4.wireOp",EDGE,"E40"),sQuery(id+"F4.wireOp",EDGE,"E41")])],"isStart":true})]}),makeQuery(id+"F6.opRevolve","SWEPT_FACE",FACE,{"disambiguationData":[OSD([subQ1])]})]}),makeQuery(id+"F7.opRevolve","SWEPT_FACE",FACE,{"disambiguationData":[OSD([subQ0])]})]})],"blendedInto":[makeQuery(id+"F7.boolean.opBoolean","MERGE",FACE,{"derivedFrom":[makeQuery(id+"F6.boolean.opBoolean","MERGE",FACE,{"derivedFrom":[makeQuery(id+"F5.boolean.opBoolean","MERGE",FACE,{"derivedFrom":[makeQuery(id+"F3.boolean.opBoolean","MERGE",FACE,{"derivedFrom":[makeQuery(id+"F2.boolean.opBoolean","MERGE",FACE,{"derivedFrom":[makeQuery(id+"F1.opExtrude","SWEPT_FACE",FACE,{"disambiguationData":[OSD([subQ2,subQ1,subQ0])]}),makeQuery(id+"F2.opExtrude","SWEPT_FACE",FACE,{"disambiguationData":[OSD([subQ2,subQ1,subQ0])]})]}),makeQuery(id+"F3.opExtrude","SWEPT_FACE",FACE,{"disambiguationData":[OSD([subQ2,subQ1,subQ0])]})]}),makeQuery(id+"F5.opExtrude","CAP_FACE",FACE,{"disambiguationData":[OSD([subQ2,subQ1,subQ0,sQuery(id+"F4.wireOp",EDGE,"E37"),sQuery(id+"F4.wireOp",EDGE,"E40"),sQuery(id+"F4.wireOp",EDGE,"E41")])],"isStart":true})]}),makeQuery(id+"F6.opRevolve","SWEPT_FACE",FACE,{"disambiguationData":[OSD([subQ1])]})]}),makeQuery(id+"F7.opRevolve","SWEPT_FACE",FACE,{"disambiguationData":[OSD([subQ0])]})]})]});}
            var Q47;
            {var subQ0=sQuery(id+"F4.wireOp",EDGE,"E66");Q47=makeQuery(id+"F12.boolean.opBoolean","COPY",EDGE,{"derivedFrom":makeQuery(id+"F12.opExtrude","CAP_EDGE",EDGE,{"disambiguationData":[OSD([subQ0]),TDD([makeQuery(id+"F4.imprint","IMPRINT",EDGE,{"disambiguationData":[TD([[makeQuery(id+"F4.imprint","INTERSECT",VERTEX,{"disambiguationData":[OD(0.0)],"derivedFrom":[sQuery(id+"F4.wireOp",EDGE,"E59"),subQ0]}),1.0]])],"derivedFrom":subQ0})])],"isStart":true})});}
            var Q48;
            {var subQ0=sQuery(id+"F0.wireOp",EDGE,"E2.bottom");var subQ1=sQuery(id+"F0.wireOp",EDGE,"E1.bottom");var subQ2=sQuery(id+"F0.wireOp",EDGE,"E0.bottom");var subQ3=sQuery(id+"F4.wireOp",EDGE,"E66");var subQ4=sQuery(id+"F4.wireOp",EDGE,"E59");Q48=makeQuery(id+"F13.opFillet","BLEND_EDGE",EDGE,{"blendedFrom":[makeQuery(id+"F12.boolean.opBoolean","COPY",EDGE,{"derivedFrom":makeQuery(id+"F12.opExtrude","SWEPT_EDGE",EDGE,{"disambiguationData":[OSD([subQ4,subQ3]),TDD([makeQuery(id+"F4.imprint","INTERSECT",VERTEX,{"disambiguationData":[OD(0.0)],"derivedFrom":[subQ4,subQ3]})])]})}),makeQuery(id+"F7.boolean.opBoolean","MERGE",FACE,{"derivedFrom":[makeQuery(id+"F6.boolean.opBoolean","MERGE",FACE,{"derivedFrom":[makeQuery(id+"F5.boolean.opBoolean","MERGE",FACE,{"derivedFrom":[makeQuery(id+"F3.boolean.opBoolean","MERGE",FACE,{"derivedFrom":[makeQuery(id+"F2.boolean.opBoolean","MERGE",FACE,{"derivedFrom":[makeQuery(id+"F1.opExtrude","SWEPT_FACE",FACE,{"disambiguationData":[OSD([subQ2,subQ1,subQ0])]}),makeQuery(id+"F2.opExtrude","SWEPT_FACE",FACE,{"disambiguationData":[OSD([subQ2,subQ1,subQ0])]})]}),makeQuery(id+"F3.opExtrude","SWEPT_FACE",FACE,{"disambiguationData":[OSD([subQ2,subQ1,subQ0])]})]}),makeQuery(id+"F5.opExtrude","CAP_FACE",FACE,{"disambiguationData":[OSD([subQ2,subQ1,subQ0,sQuery(id+"F4.wireOp",EDGE,"E37"),sQuery(id+"F4.wireOp",EDGE,"E40"),sQuery(id+"F4.wireOp",EDGE,"E41")])],"isStart":true})]}),makeQuery(id+"F6.opRevolve","SWEPT_FACE",FACE,{"disambiguationData":[OSD([subQ1])]})]}),makeQuery(id+"F7.opRevolve","SWEPT_FACE",FACE,{"disambiguationData":[OSD([subQ0])]})]})],"blendedInto":[makeQuery(id+"F7.boolean.opBoolean","MERGE",FACE,{"derivedFrom":[makeQuery(id+"F6.boolean.opBoolean","MERGE",FACE,{"derivedFrom":[makeQuery(id+"F5.boolean.opBoolean","MERGE",FACE,{"derivedFrom":[makeQuery(id+"F3.boolean.opBoolean","MERGE",FACE,{"derivedFrom":[makeQuery(id+"F2.boolean.opBoolean","MERGE",FACE,{"derivedFrom":[makeQuery(id+"F1.opExtrude","SWEPT_FACE",FACE,{"disambiguationData":[OSD([subQ2,subQ1,subQ0])]}),makeQuery(id+"F2.opExtrude","SWEPT_FACE",FACE,{"disambiguationData":[OSD([subQ2,subQ1,subQ0])]})]}),makeQuery(id+"F3.opExtrude","SWEPT_FACE",FACE,{"disambiguationData":[OSD([subQ2,subQ1,subQ0])]})]}),makeQuery(id+"F5.opExtrude","CAP_FACE",FACE,{"disambiguationData":[OSD([subQ2,subQ1,subQ0,sQuery(id+"F4.wireOp",EDGE,"E37"),sQuery(id+"F4.wireOp",EDGE,"E40"),sQuery(id+"F4.wireOp",EDGE,"E41")])],"isStart":true})]}),makeQuery(id+"F6.opRevolve","SWEPT_FACE",FACE,{"disambiguationData":[OSD([subQ1])]})]}),makeQuery(id+"F7.opRevolve","SWEPT_FACE",FACE,{"disambiguationData":[OSD([subQ0])]})]})]});}
            var Q49;
            {var subQ0=sQuery(id+"F0.wireOp",EDGE,"E2.bottom");var subQ1=sQuery(id+"F0.wireOp",EDGE,"E1.bottom");var subQ2=sQuery(id+"F0.wireOp",EDGE,"E0.bottom");Q49=makeQuery(id+"F13.opFillet","BLEND_EDGE",EDGE,{"blendedFrom":[makeQuery(id+"F12.boolean.opBoolean","COPY",EDGE,{"derivedFrom":makeQuery(id+"F12.opExtrude","SWEPT_EDGE",EDGE,{"disambiguationData":[OSD([sQuery(id+"F4.wireOp",EDGE,"E59"),sQuery(id+"F4.wireOp",EDGE,"E64")])]})}),makeQuery(id+"F7.boolean.opBoolean","MERGE",FACE,{"derivedFrom":[makeQuery(id+"F6.boolean.opBoolean","MERGE",FACE,{"derivedFrom":[makeQuery(id+"F5.boolean.opBoolean","MERGE",FACE,{"derivedFrom":[makeQuery(id+"F3.boolean.opBoolean","MERGE",FACE,{"derivedFrom":[makeQuery(id+"F2.boolean.opBoolean","MERGE",FACE,{"derivedFrom":[makeQuery(id+"F1.opExtrude","SWEPT_FACE",FACE,{"disambiguationData":[OSD([subQ2,subQ1,subQ0])]}),makeQuery(id+"F2.opExtrude","SWEPT_FACE",FACE,{"disambiguationData":[OSD([subQ2,subQ1,subQ0])]})]}),makeQuery(id+"F3.opExtrude","SWEPT_FACE",FACE,{"disambiguationData":[OSD([subQ2,subQ1,subQ0])]})]}),makeQuery(id+"F5.opExtrude","CAP_FACE",FACE,{"disambiguationData":[OSD([subQ2,subQ1,subQ0,sQuery(id+"F4.wireOp",EDGE,"E37"),sQuery(id+"F4.wireOp",EDGE,"E40"),sQuery(id+"F4.wireOp",EDGE,"E41")])],"isStart":true})]}),makeQuery(id+"F6.opRevolve","SWEPT_FACE",FACE,{"disambiguationData":[OSD([subQ1])]})]}),makeQuery(id+"F7.opRevolve","SWEPT_FACE",FACE,{"disambiguationData":[OSD([subQ0])]})]})],"blendedInto":[makeQuery(id+"F7.boolean.opBoolean","MERGE",FACE,{"derivedFrom":[makeQuery(id+"F6.boolean.opBoolean","MERGE",FACE,{"derivedFrom":[makeQuery(id+"F5.boolean.opBoolean","MERGE",FACE,{"derivedFrom":[makeQuery(id+"F3.boolean.opBoolean","MERGE",FACE,{"derivedFrom":[makeQuery(id+"F2.boolean.opBoolean","MERGE",FACE,{"derivedFrom":[makeQuery(id+"F1.opExtrude","SWEPT_FACE",FACE,{"disambiguationData":[OSD([subQ2,subQ1,subQ0])]}),makeQuery(id+"F2.opExtrude","SWEPT_FACE",FACE,{"disambiguationData":[OSD([subQ2,subQ1,subQ0])]})]}),makeQuery(id+"F3.opExtrude","SWEPT_FACE",FACE,{"disambiguationData":[OSD([subQ2,subQ1,subQ0])]})]}),makeQuery(id+"F5.opExtrude","CAP_FACE",FACE,{"disambiguationData":[OSD([subQ2,subQ1,subQ0,sQuery(id+"F4.wireOp",EDGE,"E37"),sQuery(id+"F4.wireOp",EDGE,"E40"),sQuery(id+"F4.wireOp",EDGE,"E41")])],"isStart":true})]}),makeQuery(id+"F6.opRevolve","SWEPT_FACE",FACE,{"disambiguationData":[OSD([subQ1])]})]}),makeQuery(id+"F7.opRevolve","SWEPT_FACE",FACE,{"disambiguationData":[OSD([subQ0])]})]})]});}
            var Q50;
            Q50=makeQuery(id+"F12.boolean.opBoolean","COPY",EDGE,{"derivedFrom":makeQuery(id+"F12.opExtrude","CAP_EDGE",EDGE,{"disambiguationData":[OSD([sQuery(id+"F4.wireOp",EDGE,"E64")])],"isStart":true})});
            var Q51;
            {var subQ0=sQuery(id+"F0.wireOp",EDGE,"E2.bottom");var subQ1=sQuery(id+"F0.wireOp",EDGE,"E1.bottom");var subQ2=sQuery(id+"F0.wireOp",EDGE,"E0.bottom");Q51=makeQuery(id+"F13.opFillet","BLEND_EDGE",EDGE,{"blendedFrom":[makeQuery(id+"F12.boolean.opBoolean","COPY",EDGE,{"derivedFrom":makeQuery(id+"F12.opExtrude","SWEPT_EDGE",EDGE,{"disambiguationData":[OSD([subQ2,subQ1,subQ0,sQuery(id+"F4.wireOp",EDGE,"E64")])]})}),makeQuery(id+"F7.boolean.opBoolean","MERGE",FACE,{"derivedFrom":[makeQuery(id+"F6.boolean.opBoolean","MERGE",FACE,{"derivedFrom":[makeQuery(id+"F5.boolean.opBoolean","MERGE",FACE,{"derivedFrom":[makeQuery(id+"F3.boolean.opBoolean","MERGE",FACE,{"derivedFrom":[makeQuery(id+"F2.boolean.opBoolean","MERGE",FACE,{"derivedFrom":[makeQuery(id+"F1.opExtrude","SWEPT_FACE",FACE,{"disambiguationData":[OSD([subQ2,subQ1,subQ0])]}),makeQuery(id+"F2.opExtrude","SWEPT_FACE",FACE,{"disambiguationData":[OSD([subQ2,subQ1,subQ0])]})]}),makeQuery(id+"F3.opExtrude","SWEPT_FACE",FACE,{"disambiguationData":[OSD([subQ2,subQ1,subQ0])]})]}),makeQuery(id+"F5.opExtrude","CAP_FACE",FACE,{"disambiguationData":[OSD([subQ2,subQ1,subQ0,sQuery(id+"F4.wireOp",EDGE,"E37"),sQuery(id+"F4.wireOp",EDGE,"E40"),sQuery(id+"F4.wireOp",EDGE,"E41")])],"isStart":true})]}),makeQuery(id+"F6.opRevolve","SWEPT_FACE",FACE,{"disambiguationData":[OSD([subQ1])]})]}),makeQuery(id+"F7.opRevolve","SWEPT_FACE",FACE,{"disambiguationData":[OSD([subQ0])]})]})],"blendedInto":[makeQuery(id+"F7.boolean.opBoolean","MERGE",FACE,{"derivedFrom":[makeQuery(id+"F6.boolean.opBoolean","MERGE",FACE,{"derivedFrom":[makeQuery(id+"F5.boolean.opBoolean","MERGE",FACE,{"derivedFrom":[makeQuery(id+"F3.boolean.opBoolean","MERGE",FACE,{"derivedFrom":[makeQuery(id+"F2.boolean.opBoolean","MERGE",FACE,{"derivedFrom":[makeQuery(id+"F1.opExtrude","SWEPT_FACE",FACE,{"disambiguationData":[OSD([subQ2,subQ1,subQ0])]}),makeQuery(id+"F2.opExtrude","SWEPT_FACE",FACE,{"disambiguationData":[OSD([subQ2,subQ1,subQ0])]})]}),makeQuery(id+"F3.opExtrude","SWEPT_FACE",FACE,{"disambiguationData":[OSD([subQ2,subQ1,subQ0])]})]}),makeQuery(id+"F5.opExtrude","CAP_FACE",FACE,{"disambiguationData":[OSD([subQ2,subQ1,subQ0,sQuery(id+"F4.wireOp",EDGE,"E37"),sQuery(id+"F4.wireOp",EDGE,"E40"),sQuery(id+"F4.wireOp",EDGE,"E41")])],"isStart":true})]}),makeQuery(id+"F6.opRevolve","SWEPT_FACE",FACE,{"disambiguationData":[OSD([subQ1])]})]}),makeQuery(id+"F7.opRevolve","SWEPT_FACE",FACE,{"disambiguationData":[OSD([subQ0])]})]})]});}
            var Q52;
            {var subQ0=sQuery(id+"F0.wireOp",EDGE,"E2.bottom");var subQ1=sQuery(id+"F0.wireOp",EDGE,"E1.bottom");var subQ2=sQuery(id+"F0.wireOp",EDGE,"E0.bottom");Q52=makeQuery(id+"F13.opFillet","BLEND_EDGE",EDGE,{"blendedFrom":[makeQuery(id+"F12.boolean.opBoolean","COPY",EDGE,{"derivedFrom":makeQuery(id+"F12.opExtrude","SWEPT_EDGE",EDGE,{"disambiguationData":[OSD([subQ2,subQ1,subQ0,sQuery(id+"F4.wireOp",EDGE,"E65")])]})}),makeQuery(id+"F7.boolean.opBoolean","MERGE",FACE,{"derivedFrom":[makeQuery(id+"F6.boolean.opBoolean","MERGE",FACE,{"derivedFrom":[makeQuery(id+"F5.boolean.opBoolean","MERGE",FACE,{"derivedFrom":[makeQuery(id+"F3.boolean.opBoolean","MERGE",FACE,{"derivedFrom":[makeQuery(id+"F2.boolean.opBoolean","MERGE",FACE,{"derivedFrom":[makeQuery(id+"F1.opExtrude","SWEPT_FACE",FACE,{"disambiguationData":[OSD([subQ2,subQ1,subQ0])]}),makeQuery(id+"F2.opExtrude","SWEPT_FACE",FACE,{"disambiguationData":[OSD([subQ2,subQ1,subQ0])]})]}),makeQuery(id+"F3.opExtrude","SWEPT_FACE",FACE,{"disambiguationData":[OSD([subQ2,subQ1,subQ0])]})]}),makeQuery(id+"F5.opExtrude","CAP_FACE",FACE,{"disambiguationData":[OSD([subQ2,subQ1,subQ0,sQuery(id+"F4.wireOp",EDGE,"E37"),sQuery(id+"F4.wireOp",EDGE,"E40"),sQuery(id+"F4.wireOp",EDGE,"E41")])],"isStart":true})]}),makeQuery(id+"F6.opRevolve","SWEPT_FACE",FACE,{"disambiguationData":[OSD([subQ1])]})]}),makeQuery(id+"F7.opRevolve","SWEPT_FACE",FACE,{"disambiguationData":[OSD([subQ0])]})]})],"blendedInto":[makeQuery(id+"F7.boolean.opBoolean","MERGE",FACE,{"derivedFrom":[makeQuery(id+"F6.boolean.opBoolean","MERGE",FACE,{"derivedFrom":[makeQuery(id+"F5.boolean.opBoolean","MERGE",FACE,{"derivedFrom":[makeQuery(id+"F3.boolean.opBoolean","MERGE",FACE,{"derivedFrom":[makeQuery(id+"F2.boolean.opBoolean","MERGE",FACE,{"derivedFrom":[makeQuery(id+"F1.opExtrude","SWEPT_FACE",FACE,{"disambiguationData":[OSD([subQ2,subQ1,subQ0])]}),makeQuery(id+"F2.opExtrude","SWEPT_FACE",FACE,{"disambiguationData":[OSD([subQ2,subQ1,subQ0])]})]}),makeQuery(id+"F3.opExtrude","SWEPT_FACE",FACE,{"disambiguationData":[OSD([subQ2,subQ1,subQ0])]})]}),makeQuery(id+"F5.opExtrude","CAP_FACE",FACE,{"disambiguationData":[OSD([subQ2,subQ1,subQ0,sQuery(id+"F4.wireOp",EDGE,"E37"),sQuery(id+"F4.wireOp",EDGE,"E40"),sQuery(id+"F4.wireOp",EDGE,"E41")])],"isStart":true})]}),makeQuery(id+"F6.opRevolve","SWEPT_FACE",FACE,{"disambiguationData":[OSD([subQ1])]})]}),makeQuery(id+"F7.opRevolve","SWEPT_FACE",FACE,{"disambiguationData":[OSD([subQ0])]})]})]});}
            var Q53;
            Q53=makeQuery(id+"F12.boolean.opBoolean","COPY",EDGE,{"derivedFrom":makeQuery(id+"F12.opExtrude","CAP_EDGE",EDGE,{"disambiguationData":[OSD([sQuery(id+"F4.wireOp",EDGE,"E65")])],"isStart":true})});
            var Q54;
            {var subQ0=sQuery(id+"F0.wireOp",EDGE,"E2.bottom");var subQ1=sQuery(id+"F0.wireOp",EDGE,"E1.bottom");var subQ2=sQuery(id+"F0.wireOp",EDGE,"E0.bottom");Q54=makeQuery(id+"F13.opFillet","BLEND_EDGE",EDGE,{"blendedFrom":[makeQuery(id+"F12.boolean.opBoolean","COPY",EDGE,{"derivedFrom":makeQuery(id+"F12.opExtrude","SWEPT_EDGE",EDGE,{"disambiguationData":[OSD([sQuery(id+"F4.wireOp",EDGE,"E59"),sQuery(id+"F4.wireOp",EDGE,"E65")])]})}),makeQuery(id+"F7.boolean.opBoolean","MERGE",FACE,{"derivedFrom":[makeQuery(id+"F6.boolean.opBoolean","MERGE",FACE,{"derivedFrom":[makeQuery(id+"F5.boolean.opBoolean","MERGE",FACE,{"derivedFrom":[makeQuery(id+"F3.boolean.opBoolean","MERGE",FACE,{"derivedFrom":[makeQuery(id+"F2.boolean.opBoolean","MERGE",FACE,{"derivedFrom":[makeQuery(id+"F1.opExtrude","SWEPT_FACE",FACE,{"disambiguationData":[OSD([subQ2,subQ1,subQ0])]}),makeQuery(id+"F2.opExtrude","SWEPT_FACE",FACE,{"disambiguationData":[OSD([subQ2,subQ1,subQ0])]})]}),makeQuery(id+"F3.opExtrude","SWEPT_FACE",FACE,{"disambiguationData":[OSD([subQ2,subQ1,subQ0])]})]}),makeQuery(id+"F5.opExtrude","CAP_FACE",FACE,{"disambiguationData":[OSD([subQ2,subQ1,subQ0,sQuery(id+"F4.wireOp",EDGE,"E37"),sQuery(id+"F4.wireOp",EDGE,"E40"),sQuery(id+"F4.wireOp",EDGE,"E41")])],"isStart":true})]}),makeQuery(id+"F6.opRevolve","SWEPT_FACE",FACE,{"disambiguationData":[OSD([subQ1])]})]}),makeQuery(id+"F7.opRevolve","SWEPT_FACE",FACE,{"disambiguationData":[OSD([subQ0])]})]})],"blendedInto":[makeQuery(id+"F7.boolean.opBoolean","MERGE",FACE,{"derivedFrom":[makeQuery(id+"F6.boolean.opBoolean","MERGE",FACE,{"derivedFrom":[makeQuery(id+"F5.boolean.opBoolean","MERGE",FACE,{"derivedFrom":[makeQuery(id+"F3.boolean.opBoolean","MERGE",FACE,{"derivedFrom":[makeQuery(id+"F2.boolean.opBoolean","MERGE",FACE,{"derivedFrom":[makeQuery(id+"F1.opExtrude","SWEPT_FACE",FACE,{"disambiguationData":[OSD([subQ2,subQ1,subQ0])]}),makeQuery(id+"F2.opExtrude","SWEPT_FACE",FACE,{"disambiguationData":[OSD([subQ2,subQ1,subQ0])]})]}),makeQuery(id+"F3.opExtrude","SWEPT_FACE",FACE,{"disambiguationData":[OSD([subQ2,subQ1,subQ0])]})]}),makeQuery(id+"F5.opExtrude","CAP_FACE",FACE,{"disambiguationData":[OSD([subQ2,subQ1,subQ0,sQuery(id+"F4.wireOp",EDGE,"E37"),sQuery(id+"F4.wireOp",EDGE,"E40"),sQuery(id+"F4.wireOp",EDGE,"E41")])],"isStart":true})]}),makeQuery(id+"F6.opRevolve","SWEPT_FACE",FACE,{"disambiguationData":[OSD([subQ1])]})]}),makeQuery(id+"F7.opRevolve","SWEPT_FACE",FACE,{"disambiguationData":[OSD([subQ0])]})]})]});}
            var Q55;
            {var subQ0=sQuery(id+"F4.wireOp",EDGE,"E59");Q55=makeQuery(id+"F12.boolean.opBoolean","COPY",EDGE,{"derivedFrom":makeQuery(id+"F12.opExtrude","CAP_EDGE",EDGE,{"disambiguationData":[OSD([subQ0]),TDD([makeQuery(id+"F4.imprint","IMPRINT",EDGE,{"disambiguationData":[TD([[makeQuery(id+"F4.imprint","INTERSECT",VERTEX,{"derivedFrom":[subQ0,sQuery(id+"F4.wireOp",EDGE,"E65")]}),-1.0]])],"derivedFrom":subQ0})])],"isStart":true})});}
            var Q56;
            {var subQ0=sQuery(id+"F0.wireOp",EDGE,"E2.bottom");var subQ1=sQuery(id+"F0.wireOp",EDGE,"E1.bottom");var subQ2=sQuery(id+"F0.wireOp",EDGE,"E0.bottom");var subQ3=sQuery(id+"F4.wireOp",EDGE,"E66");var subQ4=sQuery(id+"F4.wireOp",EDGE,"E59");Q56=makeQuery(id+"F13.opFillet","BLEND_EDGE",EDGE,{"blendedFrom":[makeQuery(id+"F12.boolean.opBoolean","COPY",EDGE,{"derivedFrom":makeQuery(id+"F12.opExtrude","SWEPT_EDGE",EDGE,{"disambiguationData":[OSD([subQ4,subQ3]),TDD([makeQuery(id+"F4.imprint","INTERSECT",VERTEX,{"disambiguationData":[OD(1.0)],"derivedFrom":[subQ4,subQ3]})])]})}),makeQuery(id+"F7.boolean.opBoolean","MERGE",FACE,{"derivedFrom":[makeQuery(id+"F6.boolean.opBoolean","MERGE",FACE,{"derivedFrom":[makeQuery(id+"F5.boolean.opBoolean","MERGE",FACE,{"derivedFrom":[makeQuery(id+"F3.boolean.opBoolean","MERGE",FACE,{"derivedFrom":[makeQuery(id+"F2.boolean.opBoolean","MERGE",FACE,{"derivedFrom":[makeQuery(id+"F1.opExtrude","SWEPT_FACE",FACE,{"disambiguationData":[OSD([subQ2,subQ1,subQ0])]}),makeQuery(id+"F2.opExtrude","SWEPT_FACE",FACE,{"disambiguationData":[OSD([subQ2,subQ1,subQ0])]})]}),makeQuery(id+"F3.opExtrude","SWEPT_FACE",FACE,{"disambiguationData":[OSD([subQ2,subQ1,subQ0])]})]}),makeQuery(id+"F5.opExtrude","CAP_FACE",FACE,{"disambiguationData":[OSD([subQ2,subQ1,subQ0,sQuery(id+"F4.wireOp",EDGE,"E37"),sQuery(id+"F4.wireOp",EDGE,"E40"),sQuery(id+"F4.wireOp",EDGE,"E41")])],"isStart":true})]}),makeQuery(id+"F6.opRevolve","SWEPT_FACE",FACE,{"disambiguationData":[OSD([subQ1])]})]}),makeQuery(id+"F7.opRevolve","SWEPT_FACE",FACE,{"disambiguationData":[OSD([subQ0])]})]})],"blendedInto":[makeQuery(id+"F7.boolean.opBoolean","MERGE",FACE,{"derivedFrom":[makeQuery(id+"F6.boolean.opBoolean","MERGE",FACE,{"derivedFrom":[makeQuery(id+"F5.boolean.opBoolean","MERGE",FACE,{"derivedFrom":[makeQuery(id+"F3.boolean.opBoolean","MERGE",FACE,{"derivedFrom":[makeQuery(id+"F2.boolean.opBoolean","MERGE",FACE,{"derivedFrom":[makeQuery(id+"F1.opExtrude","SWEPT_FACE",FACE,{"disambiguationData":[OSD([subQ2,subQ1,subQ0])]}),makeQuery(id+"F2.opExtrude","SWEPT_FACE",FACE,{"disambiguationData":[OSD([subQ2,subQ1,subQ0])]})]}),makeQuery(id+"F3.opExtrude","SWEPT_FACE",FACE,{"disambiguationData":[OSD([subQ2,subQ1,subQ0])]})]}),makeQuery(id+"F5.opExtrude","CAP_FACE",FACE,{"disambiguationData":[OSD([subQ2,subQ1,subQ0,sQuery(id+"F4.wireOp",EDGE,"E37"),sQuery(id+"F4.wireOp",EDGE,"E40"),sQuery(id+"F4.wireOp",EDGE,"E41")])],"isStart":true})]}),makeQuery(id+"F6.opRevolve","SWEPT_FACE",FACE,{"disambiguationData":[OSD([subQ1])]})]}),makeQuery(id+"F7.opRevolve","SWEPT_FACE",FACE,{"disambiguationData":[OSD([subQ0])]})]})]});}
            var Q57;
            {var subQ0=sQuery(id+"F4.wireOp",EDGE,"E66");Q57=makeQuery(id+"F12.boolean.opBoolean","COPY",EDGE,{"derivedFrom":makeQuery(id+"F12.opExtrude","CAP_EDGE",EDGE,{"disambiguationData":[OSD([subQ0]),TDD([makeQuery(id+"F4.imprint","IMPRINT",EDGE,{"disambiguationData":[TD([[makeQuery(id+"F4.imprint","INTERSECT",VERTEX,{"disambiguationData":[OD(1.0)],"derivedFrom":[sQuery(id+"F4.wireOp",EDGE,"E59"),subQ0]}),-1.0]])],"derivedFrom":subQ0})])],"isStart":true})});}
            var Q58;
            {var subQ0=sQuery(id+"F0.wireOp",EDGE,"E2.bottom");var subQ1=sQuery(id+"F0.wireOp",EDGE,"E1.bottom");var subQ2=sQuery(id+"F0.wireOp",EDGE,"E0.bottom");Q58=makeQuery(id+"F13.opFillet","BLEND_EDGE",EDGE,{"blendedFrom":[makeQuery(id+"F12.boolean.opBoolean","COPY",EDGE,{"derivedFrom":makeQuery(id+"F12.opExtrude","SWEPT_EDGE",EDGE,{"disambiguationData":[OSD([sQuery(id+"F4.wireOp",EDGE,"E61"),sQuery(id+"F4.wireOp",EDGE,"E66")])]})}),makeQuery(id+"F7.boolean.opBoolean","MERGE",FACE,{"derivedFrom":[makeQuery(id+"F6.boolean.opBoolean","MERGE",FACE,{"derivedFrom":[makeQuery(id+"F5.boolean.opBoolean","MERGE",FACE,{"derivedFrom":[makeQuery(id+"F3.boolean.opBoolean","MERGE",FACE,{"derivedFrom":[makeQuery(id+"F2.boolean.opBoolean","MERGE",FACE,{"derivedFrom":[makeQuery(id+"F1.opExtrude","SWEPT_FACE",FACE,{"disambiguationData":[OSD([subQ2,subQ1,subQ0])]}),makeQuery(id+"F2.opExtrude","SWEPT_FACE",FACE,{"disambiguationData":[OSD([subQ2,subQ1,subQ0])]})]}),makeQuery(id+"F3.opExtrude","SWEPT_FACE",FACE,{"disambiguationData":[OSD([subQ2,subQ1,subQ0])]})]}),makeQuery(id+"F5.opExtrude","CAP_FACE",FACE,{"disambiguationData":[OSD([subQ2,subQ1,subQ0,sQuery(id+"F4.wireOp",EDGE,"E37"),sQuery(id+"F4.wireOp",EDGE,"E40"),sQuery(id+"F4.wireOp",EDGE,"E41")])],"isStart":true})]}),makeQuery(id+"F6.opRevolve","SWEPT_FACE",FACE,{"disambiguationData":[OSD([subQ1])]})]}),makeQuery(id+"F7.opRevolve","SWEPT_FACE",FACE,{"disambiguationData":[OSD([subQ0])]})]})],"blendedInto":[makeQuery(id+"F7.boolean.opBoolean","MERGE",FACE,{"derivedFrom":[makeQuery(id+"F6.boolean.opBoolean","MERGE",FACE,{"derivedFrom":[makeQuery(id+"F5.boolean.opBoolean","MERGE",FACE,{"derivedFrom":[makeQuery(id+"F3.boolean.opBoolean","MERGE",FACE,{"derivedFrom":[makeQuery(id+"F2.boolean.opBoolean","MERGE",FACE,{"derivedFrom":[makeQuery(id+"F1.opExtrude","SWEPT_FACE",FACE,{"disambiguationData":[OSD([subQ2,subQ1,subQ0])]}),makeQuery(id+"F2.opExtrude","SWEPT_FACE",FACE,{"disambiguationData":[OSD([subQ2,subQ1,subQ0])]})]}),makeQuery(id+"F3.opExtrude","SWEPT_FACE",FACE,{"disambiguationData":[OSD([subQ2,subQ1,subQ0])]})]}),makeQuery(id+"F5.opExtrude","CAP_FACE",FACE,{"disambiguationData":[OSD([subQ2,subQ1,subQ0,sQuery(id+"F4.wireOp",EDGE,"E37"),sQuery(id+"F4.wireOp",EDGE,"E40"),sQuery(id+"F4.wireOp",EDGE,"E41")])],"isStart":true})]}),makeQuery(id+"F6.opRevolve","SWEPT_FACE",FACE,{"disambiguationData":[OSD([subQ1])]})]}),makeQuery(id+"F7.opRevolve","SWEPT_FACE",FACE,{"disambiguationData":[OSD([subQ0])]})]})]});}
            var Q59;
            Q59=makeQuery(id+"F12.boolean.opBoolean","COPY",EDGE,{"derivedFrom":makeQuery(id+"F12.opExtrude","CAP_EDGE",EDGE,{"disambiguationData":[OSD([sQuery(id+"F4.wireOp",EDGE,"E61")])],"isStart":true})});
            var Q60;
            {var subQ0=sQuery(id+"F0.wireOp",EDGE,"E2.bottom");var subQ1=sQuery(id+"F0.wireOp",EDGE,"E1.bottom");var subQ2=sQuery(id+"F0.wireOp",EDGE,"E0.bottom");Q60=makeQuery(id+"F13.opFillet","BLEND_EDGE",EDGE,{"blendedFrom":[makeQuery(id+"F12.boolean.opBoolean","COPY",EDGE,{"derivedFrom":makeQuery(id+"F12.opExtrude","SWEPT_EDGE",EDGE,{"disambiguationData":[OSD([sQuery(id+"F4.wireOp",EDGE,"E61"),sQuery(id+"F4.wireOp",EDGE,"E63")])]})}),makeQuery(id+"F7.boolean.opBoolean","MERGE",FACE,{"derivedFrom":[makeQuery(id+"F6.boolean.opBoolean","MERGE",FACE,{"derivedFrom":[makeQuery(id+"F5.boolean.opBoolean","MERGE",FACE,{"derivedFrom":[makeQuery(id+"F3.boolean.opBoolean","MERGE",FACE,{"derivedFrom":[makeQuery(id+"F2.boolean.opBoolean","MERGE",FACE,{"derivedFrom":[makeQuery(id+"F1.opExtrude","SWEPT_FACE",FACE,{"disambiguationData":[OSD([subQ2,subQ1,subQ0])]}),makeQuery(id+"F2.opExtrude","SWEPT_FACE",FACE,{"disambiguationData":[OSD([subQ2,subQ1,subQ0])]})]}),makeQuery(id+"F3.opExtrude","SWEPT_FACE",FACE,{"disambiguationData":[OSD([subQ2,subQ1,subQ0])]})]}),makeQuery(id+"F5.opExtrude","CAP_FACE",FACE,{"disambiguationData":[OSD([subQ2,subQ1,subQ0,sQuery(id+"F4.wireOp",EDGE,"E37"),sQuery(id+"F4.wireOp",EDGE,"E40"),sQuery(id+"F4.wireOp",EDGE,"E41")])],"isStart":true})]}),makeQuery(id+"F6.opRevolve","SWEPT_FACE",FACE,{"disambiguationData":[OSD([subQ1])]})]}),makeQuery(id+"F7.opRevolve","SWEPT_FACE",FACE,{"disambiguationData":[OSD([subQ0])]})]})],"blendedInto":[makeQuery(id+"F7.boolean.opBoolean","MERGE",FACE,{"derivedFrom":[makeQuery(id+"F6.boolean.opBoolean","MERGE",FACE,{"derivedFrom":[makeQuery(id+"F5.boolean.opBoolean","MERGE",FACE,{"derivedFrom":[makeQuery(id+"F3.boolean.opBoolean","MERGE",FACE,{"derivedFrom":[makeQuery(id+"F2.boolean.opBoolean","MERGE",FACE,{"derivedFrom":[makeQuery(id+"F1.opExtrude","SWEPT_FACE",FACE,{"disambiguationData":[OSD([subQ2,subQ1,subQ0])]}),makeQuery(id+"F2.opExtrude","SWEPT_FACE",FACE,{"disambiguationData":[OSD([subQ2,subQ1,subQ0])]})]}),makeQuery(id+"F3.opExtrude","SWEPT_FACE",FACE,{"disambiguationData":[OSD([subQ2,subQ1,subQ0])]})]}),makeQuery(id+"F5.opExtrude","CAP_FACE",FACE,{"disambiguationData":[OSD([subQ2,subQ1,subQ0,sQuery(id+"F4.wireOp",EDGE,"E37"),sQuery(id+"F4.wireOp",EDGE,"E40"),sQuery(id+"F4.wireOp",EDGE,"E41")])],"isStart":true})]}),makeQuery(id+"F6.opRevolve","SWEPT_FACE",FACE,{"disambiguationData":[OSD([subQ1])]})]}),makeQuery(id+"F7.opRevolve","SWEPT_FACE",FACE,{"disambiguationData":[OSD([subQ0])]})]})]});}
            var Q61;
            Q61=makeQuery(id+"F12.boolean.opBoolean","COPY",EDGE,{"derivedFrom":makeQuery(id+"F12.opExtrude","CAP_EDGE",EDGE,{"disambiguationData":[OSD([sQuery(id+"F4.wireOp",EDGE,"E63")])],"isStart":true})});
            var Q62;
            {var subQ0=sQuery(id+"F0.wireOp",EDGE,"E2.bottom");var subQ1=sQuery(id+"F0.wireOp",EDGE,"E1.bottom");var subQ2=sQuery(id+"F0.wireOp",EDGE,"E0.bottom");Q62=makeQuery(id+"F13.opFillet","BLEND_EDGE",EDGE,{"blendedFrom":[makeQuery(id+"F12.boolean.opBoolean","COPY",EDGE,{"derivedFrom":makeQuery(id+"F12.opExtrude","SWEPT_EDGE",EDGE,{"disambiguationData":[OSD([subQ2,subQ1,subQ0,sQuery(id+"F4.wireOp",EDGE,"E63")])]})}),makeQuery(id+"F7.boolean.opBoolean","MERGE",FACE,{"derivedFrom":[makeQuery(id+"F6.boolean.opBoolean","MERGE",FACE,{"derivedFrom":[makeQuery(id+"F5.boolean.opBoolean","MERGE",FACE,{"derivedFrom":[makeQuery(id+"F3.boolean.opBoolean","MERGE",FACE,{"derivedFrom":[makeQuery(id+"F2.boolean.opBoolean","MERGE",FACE,{"derivedFrom":[makeQuery(id+"F1.opExtrude","SWEPT_FACE",FACE,{"disambiguationData":[OSD([subQ2,subQ1,subQ0])]}),makeQuery(id+"F2.opExtrude","SWEPT_FACE",FACE,{"disambiguationData":[OSD([subQ2,subQ1,subQ0])]})]}),makeQuery(id+"F3.opExtrude","SWEPT_FACE",FACE,{"disambiguationData":[OSD([subQ2,subQ1,subQ0])]})]}),makeQuery(id+"F5.opExtrude","CAP_FACE",FACE,{"disambiguationData":[OSD([subQ2,subQ1,subQ0,sQuery(id+"F4.wireOp",EDGE,"E37"),sQuery(id+"F4.wireOp",EDGE,"E40"),sQuery(id+"F4.wireOp",EDGE,"E41")])],"isStart":true})]}),makeQuery(id+"F6.opRevolve","SWEPT_FACE",FACE,{"disambiguationData":[OSD([subQ1])]})]}),makeQuery(id+"F7.opRevolve","SWEPT_FACE",FACE,{"disambiguationData":[OSD([subQ0])]})]})],"blendedInto":[makeQuery(id+"F7.boolean.opBoolean","MERGE",FACE,{"derivedFrom":[makeQuery(id+"F6.boolean.opBoolean","MERGE",FACE,{"derivedFrom":[makeQuery(id+"F5.boolean.opBoolean","MERGE",FACE,{"derivedFrom":[makeQuery(id+"F3.boolean.opBoolean","MERGE",FACE,{"derivedFrom":[makeQuery(id+"F2.boolean.opBoolean","MERGE",FACE,{"derivedFrom":[makeQuery(id+"F1.opExtrude","SWEPT_FACE",FACE,{"disambiguationData":[OSD([subQ2,subQ1,subQ0])]}),makeQuery(id+"F2.opExtrude","SWEPT_FACE",FACE,{"disambiguationData":[OSD([subQ2,subQ1,subQ0])]})]}),makeQuery(id+"F3.opExtrude","SWEPT_FACE",FACE,{"disambiguationData":[OSD([subQ2,subQ1,subQ0])]})]}),makeQuery(id+"F5.opExtrude","CAP_FACE",FACE,{"disambiguationData":[OSD([subQ2,subQ1,subQ0,sQuery(id+"F4.wireOp",EDGE,"E37"),sQuery(id+"F4.wireOp",EDGE,"E40"),sQuery(id+"F4.wireOp",EDGE,"E41")])],"isStart":true})]}),makeQuery(id+"F6.opRevolve","SWEPT_FACE",FACE,{"disambiguationData":[OSD([subQ1])]})]}),makeQuery(id+"F7.opRevolve","SWEPT_FACE",FACE,{"disambiguationData":[OSD([subQ0])]})]})]});}
            var Q63;
            {var subQ0=sQuery(id+"F4.wireOp",EDGE,"E59");Q63=makeQuery(id+"F12.boolean.opBoolean","COPY",EDGE,{"derivedFrom":makeQuery(id+"F12.opExtrude","CAP_EDGE",EDGE,{"disambiguationData":[OSD([subQ0]),TDD([makeQuery(id+"F4.imprint","IMPRINT",EDGE,{"disambiguationData":[TD([[makeQuery(id+"F4.imprint","INTERSECT",VERTEX,{"disambiguationData":[OD(0.0)],"derivedFrom":[subQ0,sQuery(id+"F4.wireOp",EDGE,"E66")]}),-1.0]])],"derivedFrom":subQ0})])],"isStart":true})});}
            var Q64;
            {var subQ0=sQuery(id+"F0.wireOp",EDGE,"E2.bottom");var subQ1=sQuery(id+"F0.wireOp",EDGE,"E1.bottom");var subQ2=sQuery(id+"F0.wireOp",EDGE,"E0.bottom");var subQ3=sQuery(id+"F0.wireOp",EDGE,"E10");var subQ4=sQuery(id+"F0.wireOp",EDGE,"E9");var subQ5=sQuery(id+"F0.wireOp",EDGE,"E8");var subQ6=sQuery(id+"F0.wireOp",EDGE,"E7");var subQ7=sQuery(id+"F0.wireOp",EDGE,"E0.top");Q64=makeQuery(id+"F13.opFillet","BLEND_EDGE",EDGE,{"blendedFrom":[makeQuery(id+"F12.boolean.opBoolean","COPY",EDGE,{"derivedFrom":makeQuery(id+"F12.opExtrude","SWEPT_EDGE",EDGE,{"disambiguationData":[OSD([subQ2,subQ1,subQ0,sQuery(id+"F4.wireOp",EDGE,"E63")])]})}),makeQuery(id+"F5.boolean.opBoolean","MERGE",FACE,{"derivedFrom":[makeQuery(id+"F3.boolean.opBoolean","MERGE",FACE,{"derivedFrom":[makeQuery(id+"F2.boolean.opBoolean","MERGE",FACE,{"derivedFrom":[makeQuery(id+"F1.opExtrude","SWEPT_FACE",FACE,{"disambiguationData":[OSD([subQ7])]}),makeQuery(id+"F2.opExtrude","SWEPT_FACE",FACE,{"disambiguationData":[OSD([subQ7,subQ6,subQ5,subQ4,subQ3])]})]}),makeQuery(id+"F3.opExtrude","SWEPT_FACE",FACE,{"disambiguationData":[OSD([subQ7,subQ6,subQ5,subQ4,subQ3,sQuery(id+"F0.wireOp",EDGE,"E11"),sQuery(id+"F0.wireOp",EDGE,"E12")])]})]}),makeQuery(id+"F5.opExtrude","CAP_FACE",FACE,{"disambiguationData":[OSD([subQ2,subQ1,subQ0,sQuery(id+"F4.wireOp",EDGE,"E37"),sQuery(id+"F4.wireOp",EDGE,"E40"),sQuery(id+"F4.wireOp",EDGE,"E41")])],"isStart":false})]})],"blendedInto":[makeQuery(id+"F5.boolean.opBoolean","MERGE",FACE,{"derivedFrom":[makeQuery(id+"F3.boolean.opBoolean","MERGE",FACE,{"derivedFrom":[makeQuery(id+"F2.boolean.opBoolean","MERGE",FACE,{"derivedFrom":[makeQuery(id+"F1.opExtrude","SWEPT_FACE",FACE,{"disambiguationData":[OSD([subQ7])]}),makeQuery(id+"F2.opExtrude","SWEPT_FACE",FACE,{"disambiguationData":[OSD([subQ7,subQ6,subQ5,subQ4,subQ3])]})]}),makeQuery(id+"F3.opExtrude","SWEPT_FACE",FACE,{"disambiguationData":[OSD([subQ7,subQ6,subQ5,subQ4,subQ3,sQuery(id+"F0.wireOp",EDGE,"E11"),sQuery(id+"F0.wireOp",EDGE,"E12")])]})]}),makeQuery(id+"F5.opExtrude","CAP_FACE",FACE,{"disambiguationData":[OSD([subQ2,subQ1,subQ0,sQuery(id+"F4.wireOp",EDGE,"E37"),sQuery(id+"F4.wireOp",EDGE,"E40"),sQuery(id+"F4.wireOp",EDGE,"E41")])],"isStart":false})]})]});}
            var Q65;
            {var subQ0=sQuery(id+"F0.wireOp",EDGE,"E10");var subQ1=sQuery(id+"F0.wireOp",EDGE,"E9");var subQ2=sQuery(id+"F0.wireOp",EDGE,"E8");var subQ3=sQuery(id+"F0.wireOp",EDGE,"E7");var subQ4=sQuery(id+"F0.wireOp",EDGE,"E0.top");Q65=makeQuery(id+"F12.boolean.opBoolean","INTERSECT",EDGE,{"derivedFrom":[makeQuery(id+"F5.boolean.opBoolean","MERGE",FACE,{"derivedFrom":[makeQuery(id+"F3.boolean.opBoolean","MERGE",FACE,{"derivedFrom":[makeQuery(id+"F2.boolean.opBoolean","MERGE",FACE,{"derivedFrom":[makeQuery(id+"F1.opExtrude","SWEPT_FACE",FACE,{"disambiguationData":[OSD([subQ4])]}),makeQuery(id+"F2.opExtrude","SWEPT_FACE",FACE,{"disambiguationData":[OSD([subQ4,subQ3,subQ2,subQ1,subQ0])]})]}),makeQuery(id+"F3.opExtrude","SWEPT_FACE",FACE,{"disambiguationData":[OSD([subQ4,subQ3,subQ2,subQ1,subQ0,sQuery(id+"F0.wireOp",EDGE,"E11"),sQuery(id+"F0.wireOp",EDGE,"E12")])]})]}),makeQuery(id+"F5.opExtrude","CAP_FACE",FACE,{"disambiguationData":[OSD([sQuery(id+"F0.wireOp",EDGE,"E0.bottom"),sQuery(id+"F0.wireOp",EDGE,"E1.bottom"),sQuery(id+"F0.wireOp",EDGE,"E2.bottom"),sQuery(id+"F4.wireOp",EDGE,"E37"),sQuery(id+"F4.wireOp",EDGE,"E40"),sQuery(id+"F4.wireOp",EDGE,"E41")])],"isStart":false})]}),makeQuery(id+"F12.opExtrude","SWEPT_FACE",FACE,{"disambiguationData":[OSD([sQuery(id+"F4.wireOp",EDGE,"E63")])]})]});}
            var Q66;
            {var subQ0=sQuery(id+"F0.wireOp",EDGE,"E10");var subQ1=sQuery(id+"F0.wireOp",EDGE,"E9");var subQ2=sQuery(id+"F0.wireOp",EDGE,"E8");var subQ3=sQuery(id+"F0.wireOp",EDGE,"E7");var subQ4=sQuery(id+"F0.wireOp",EDGE,"E0.top");Q66=makeQuery(id+"F13.opFillet","BLEND_EDGE",EDGE,{"blendedFrom":[makeQuery(id+"F12.boolean.opBoolean","COPY",EDGE,{"derivedFrom":makeQuery(id+"F12.opExtrude","SWEPT_EDGE",EDGE,{"disambiguationData":[OSD([sQuery(id+"F4.wireOp",EDGE,"E61"),sQuery(id+"F4.wireOp",EDGE,"E63")])]})}),makeQuery(id+"F5.boolean.opBoolean","MERGE",FACE,{"derivedFrom":[makeQuery(id+"F3.boolean.opBoolean","MERGE",FACE,{"derivedFrom":[makeQuery(id+"F2.boolean.opBoolean","MERGE",FACE,{"derivedFrom":[makeQuery(id+"F1.opExtrude","SWEPT_FACE",FACE,{"disambiguationData":[OSD([subQ4])]}),makeQuery(id+"F2.opExtrude","SWEPT_FACE",FACE,{"disambiguationData":[OSD([subQ4,subQ3,subQ2,subQ1,subQ0])]})]}),makeQuery(id+"F3.opExtrude","SWEPT_FACE",FACE,{"disambiguationData":[OSD([subQ4,subQ3,subQ2,subQ1,subQ0,sQuery(id+"F0.wireOp",EDGE,"E11"),sQuery(id+"F0.wireOp",EDGE,"E12")])]})]}),makeQuery(id+"F5.opExtrude","CAP_FACE",FACE,{"disambiguationData":[OSD([sQuery(id+"F0.wireOp",EDGE,"E0.bottom"),sQuery(id+"F0.wireOp",EDGE,"E1.bottom"),sQuery(id+"F0.wireOp",EDGE,"E2.bottom"),sQuery(id+"F4.wireOp",EDGE,"E37"),sQuery(id+"F4.wireOp",EDGE,"E40"),sQuery(id+"F4.wireOp",EDGE,"E41")])],"isStart":false})]})],"blendedInto":[makeQuery(id+"F5.boolean.opBoolean","MERGE",FACE,{"derivedFrom":[makeQuery(id+"F3.boolean.opBoolean","MERGE",FACE,{"derivedFrom":[makeQuery(id+"F2.boolean.opBoolean","MERGE",FACE,{"derivedFrom":[makeQuery(id+"F1.opExtrude","SWEPT_FACE",FACE,{"disambiguationData":[OSD([subQ4])]}),makeQuery(id+"F2.opExtrude","SWEPT_FACE",FACE,{"disambiguationData":[OSD([subQ4,subQ3,subQ2,subQ1,subQ0])]})]}),makeQuery(id+"F3.opExtrude","SWEPT_FACE",FACE,{"disambiguationData":[OSD([subQ4,subQ3,subQ2,subQ1,subQ0,sQuery(id+"F0.wireOp",EDGE,"E11"),sQuery(id+"F0.wireOp",EDGE,"E12")])]})]}),makeQuery(id+"F5.opExtrude","CAP_FACE",FACE,{"disambiguationData":[OSD([sQuery(id+"F0.wireOp",EDGE,"E0.bottom"),sQuery(id+"F0.wireOp",EDGE,"E1.bottom"),sQuery(id+"F0.wireOp",EDGE,"E2.bottom"),sQuery(id+"F4.wireOp",EDGE,"E37"),sQuery(id+"F4.wireOp",EDGE,"E40"),sQuery(id+"F4.wireOp",EDGE,"E41")])],"isStart":false})]})]});}
            var Q67;
            {var subQ0=sQuery(id+"F0.wireOp",EDGE,"E10");var subQ1=sQuery(id+"F0.wireOp",EDGE,"E9");var subQ2=sQuery(id+"F0.wireOp",EDGE,"E8");var subQ3=sQuery(id+"F0.wireOp",EDGE,"E7");var subQ4=sQuery(id+"F0.wireOp",EDGE,"E0.top");Q67=makeQuery(id+"F12.boolean.opBoolean","INTERSECT",EDGE,{"derivedFrom":[makeQuery(id+"F5.boolean.opBoolean","MERGE",FACE,{"derivedFrom":[makeQuery(id+"F3.boolean.opBoolean","MERGE",FACE,{"derivedFrom":[makeQuery(id+"F2.boolean.opBoolean","MERGE",FACE,{"derivedFrom":[makeQuery(id+"F1.opExtrude","SWEPT_FACE",FACE,{"disambiguationData":[OSD([subQ4])]}),makeQuery(id+"F2.opExtrude","SWEPT_FACE",FACE,{"disambiguationData":[OSD([subQ4,subQ3,subQ2,subQ1,subQ0])]})]}),makeQuery(id+"F3.opExtrude","SWEPT_FACE",FACE,{"disambiguationData":[OSD([subQ4,subQ3,subQ2,subQ1,subQ0,sQuery(id+"F0.wireOp",EDGE,"E11"),sQuery(id+"F0.wireOp",EDGE,"E12")])]})]}),makeQuery(id+"F5.opExtrude","CAP_FACE",FACE,{"disambiguationData":[OSD([sQuery(id+"F0.wireOp",EDGE,"E0.bottom"),sQuery(id+"F0.wireOp",EDGE,"E1.bottom"),sQuery(id+"F0.wireOp",EDGE,"E2.bottom"),sQuery(id+"F4.wireOp",EDGE,"E37"),sQuery(id+"F4.wireOp",EDGE,"E40"),sQuery(id+"F4.wireOp",EDGE,"E41")])],"isStart":false})]}),makeQuery(id+"F12.opExtrude","SWEPT_FACE",FACE,{"disambiguationData":[OSD([sQuery(id+"F4.wireOp",EDGE,"E61")])]})]});}
            var Q68;
            {var subQ0=sQuery(id+"F0.wireOp",EDGE,"E10");var subQ1=sQuery(id+"F0.wireOp",EDGE,"E9");var subQ2=sQuery(id+"F0.wireOp",EDGE,"E8");var subQ3=sQuery(id+"F0.wireOp",EDGE,"E7");var subQ4=sQuery(id+"F0.wireOp",EDGE,"E0.top");Q68=makeQuery(id+"F13.opFillet","BLEND_EDGE",EDGE,{"blendedFrom":[makeQuery(id+"F12.boolean.opBoolean","COPY",EDGE,{"derivedFrom":makeQuery(id+"F12.opExtrude","SWEPT_EDGE",EDGE,{"disambiguationData":[OSD([sQuery(id+"F4.wireOp",EDGE,"E61"),sQuery(id+"F4.wireOp",EDGE,"E66")])]})}),makeQuery(id+"F5.boolean.opBoolean","MERGE",FACE,{"derivedFrom":[makeQuery(id+"F3.boolean.opBoolean","MERGE",FACE,{"derivedFrom":[makeQuery(id+"F2.boolean.opBoolean","MERGE",FACE,{"derivedFrom":[makeQuery(id+"F1.opExtrude","SWEPT_FACE",FACE,{"disambiguationData":[OSD([subQ4])]}),makeQuery(id+"F2.opExtrude","SWEPT_FACE",FACE,{"disambiguationData":[OSD([subQ4,subQ3,subQ2,subQ1,subQ0])]})]}),makeQuery(id+"F3.opExtrude","SWEPT_FACE",FACE,{"disambiguationData":[OSD([subQ4,subQ3,subQ2,subQ1,subQ0,sQuery(id+"F0.wireOp",EDGE,"E11"),sQuery(id+"F0.wireOp",EDGE,"E12")])]})]}),makeQuery(id+"F5.opExtrude","CAP_FACE",FACE,{"disambiguationData":[OSD([sQuery(id+"F0.wireOp",EDGE,"E0.bottom"),sQuery(id+"F0.wireOp",EDGE,"E1.bottom"),sQuery(id+"F0.wireOp",EDGE,"E2.bottom"),sQuery(id+"F4.wireOp",EDGE,"E37"),sQuery(id+"F4.wireOp",EDGE,"E40"),sQuery(id+"F4.wireOp",EDGE,"E41")])],"isStart":false})]})],"blendedInto":[makeQuery(id+"F5.boolean.opBoolean","MERGE",FACE,{"derivedFrom":[makeQuery(id+"F3.boolean.opBoolean","MERGE",FACE,{"derivedFrom":[makeQuery(id+"F2.boolean.opBoolean","MERGE",FACE,{"derivedFrom":[makeQuery(id+"F1.opExtrude","SWEPT_FACE",FACE,{"disambiguationData":[OSD([subQ4])]}),makeQuery(id+"F2.opExtrude","SWEPT_FACE",FACE,{"disambiguationData":[OSD([subQ4,subQ3,subQ2,subQ1,subQ0])]})]}),makeQuery(id+"F3.opExtrude","SWEPT_FACE",FACE,{"disambiguationData":[OSD([subQ4,subQ3,subQ2,subQ1,subQ0,sQuery(id+"F0.wireOp",EDGE,"E11"),sQuery(id+"F0.wireOp",EDGE,"E12")])]})]}),makeQuery(id+"F5.opExtrude","CAP_FACE",FACE,{"disambiguationData":[OSD([sQuery(id+"F0.wireOp",EDGE,"E0.bottom"),sQuery(id+"F0.wireOp",EDGE,"E1.bottom"),sQuery(id+"F0.wireOp",EDGE,"E2.bottom"),sQuery(id+"F4.wireOp",EDGE,"E37"),sQuery(id+"F4.wireOp",EDGE,"E40"),sQuery(id+"F4.wireOp",EDGE,"E41")])],"isStart":false})]})]});}
            var Q69;
            {var subQ0=sQuery(id+"F4.wireOp",EDGE,"E66");var subQ1=sQuery(id+"F0.wireOp",EDGE,"E10");var subQ2=sQuery(id+"F0.wireOp",EDGE,"E9");var subQ3=sQuery(id+"F0.wireOp",EDGE,"E8");var subQ4=sQuery(id+"F0.wireOp",EDGE,"E7");var subQ5=sQuery(id+"F0.wireOp",EDGE,"E0.top");Q69=makeQuery(id+"F12.boolean.opBoolean","INTERSECT",EDGE,{"derivedFrom":[makeQuery(id+"F5.boolean.opBoolean","MERGE",FACE,{"derivedFrom":[makeQuery(id+"F3.boolean.opBoolean","MERGE",FACE,{"derivedFrom":[makeQuery(id+"F2.boolean.opBoolean","MERGE",FACE,{"derivedFrom":[makeQuery(id+"F1.opExtrude","SWEPT_FACE",FACE,{"disambiguationData":[OSD([subQ5])]}),makeQuery(id+"F2.opExtrude","SWEPT_FACE",FACE,{"disambiguationData":[OSD([subQ5,subQ4,subQ3,subQ2,subQ1])]})]}),makeQuery(id+"F3.opExtrude","SWEPT_FACE",FACE,{"disambiguationData":[OSD([subQ5,subQ4,subQ3,subQ2,subQ1,sQuery(id+"F0.wireOp",EDGE,"E11"),sQuery(id+"F0.wireOp",EDGE,"E12")])]})]}),makeQuery(id+"F5.opExtrude","CAP_FACE",FACE,{"disambiguationData":[OSD([sQuery(id+"F0.wireOp",EDGE,"E0.bottom"),sQuery(id+"F0.wireOp",EDGE,"E1.bottom"),sQuery(id+"F0.wireOp",EDGE,"E2.bottom"),sQuery(id+"F4.wireOp",EDGE,"E37"),sQuery(id+"F4.wireOp",EDGE,"E40"),sQuery(id+"F4.wireOp",EDGE,"E41")])],"isStart":false})]}),makeQuery(id+"F12.opExtrude","SWEPT_FACE",FACE,{"disambiguationData":[OSD([subQ0]),TDD([makeQuery(id+"F4.imprint","IMPRINT",EDGE,{"disambiguationData":[TD([[makeQuery(id+"F4.imprint","INTERSECT",VERTEX,{"disambiguationData":[OD(1.0)],"derivedFrom":[sQuery(id+"F4.wireOp",EDGE,"E59"),subQ0]}),-1.0]])],"derivedFrom":subQ0})])]})]});}
            var Q70;
            {var subQ0=sQuery(id+"F0.wireOp",EDGE,"E10");var subQ1=sQuery(id+"F0.wireOp",EDGE,"E9");var subQ2=sQuery(id+"F0.wireOp",EDGE,"E8");var subQ3=sQuery(id+"F0.wireOp",EDGE,"E7");var subQ4=sQuery(id+"F0.wireOp",EDGE,"E0.top");var subQ5=sQuery(id+"F4.wireOp",EDGE,"E66");var subQ6=sQuery(id+"F4.wireOp",EDGE,"E59");Q70=makeQuery(id+"F13.opFillet","BLEND_EDGE",EDGE,{"blendedFrom":[makeQuery(id+"F12.boolean.opBoolean","COPY",EDGE,{"derivedFrom":makeQuery(id+"F12.opExtrude","SWEPT_EDGE",EDGE,{"disambiguationData":[OSD([subQ6,subQ5]),TDD([makeQuery(id+"F4.imprint","INTERSECT",VERTEX,{"disambiguationData":[OD(1.0)],"derivedFrom":[subQ6,subQ5]})])]})}),makeQuery(id+"F5.boolean.opBoolean","MERGE",FACE,{"derivedFrom":[makeQuery(id+"F3.boolean.opBoolean","MERGE",FACE,{"derivedFrom":[makeQuery(id+"F2.boolean.opBoolean","MERGE",FACE,{"derivedFrom":[makeQuery(id+"F1.opExtrude","SWEPT_FACE",FACE,{"disambiguationData":[OSD([subQ4])]}),makeQuery(id+"F2.opExtrude","SWEPT_FACE",FACE,{"disambiguationData":[OSD([subQ4,subQ3,subQ2,subQ1,subQ0])]})]}),makeQuery(id+"F3.opExtrude","SWEPT_FACE",FACE,{"disambiguationData":[OSD([subQ4,subQ3,subQ2,subQ1,subQ0,sQuery(id+"F0.wireOp",EDGE,"E11"),sQuery(id+"F0.wireOp",EDGE,"E12")])]})]}),makeQuery(id+"F5.opExtrude","CAP_FACE",FACE,{"disambiguationData":[OSD([sQuery(id+"F0.wireOp",EDGE,"E0.bottom"),sQuery(id+"F0.wireOp",EDGE,"E1.bottom"),sQuery(id+"F0.wireOp",EDGE,"E2.bottom"),sQuery(id+"F4.wireOp",EDGE,"E37"),sQuery(id+"F4.wireOp",EDGE,"E40"),sQuery(id+"F4.wireOp",EDGE,"E41")])],"isStart":false})]})],"blendedInto":[makeQuery(id+"F5.boolean.opBoolean","MERGE",FACE,{"derivedFrom":[makeQuery(id+"F3.boolean.opBoolean","MERGE",FACE,{"derivedFrom":[makeQuery(id+"F2.boolean.opBoolean","MERGE",FACE,{"derivedFrom":[makeQuery(id+"F1.opExtrude","SWEPT_FACE",FACE,{"disambiguationData":[OSD([subQ4])]}),makeQuery(id+"F2.opExtrude","SWEPT_FACE",FACE,{"disambiguationData":[OSD([subQ4,subQ3,subQ2,subQ1,subQ0])]})]}),makeQuery(id+"F3.opExtrude","SWEPT_FACE",FACE,{"disambiguationData":[OSD([subQ4,subQ3,subQ2,subQ1,subQ0,sQuery(id+"F0.wireOp",EDGE,"E11"),sQuery(id+"F0.wireOp",EDGE,"E12")])]})]}),makeQuery(id+"F5.opExtrude","CAP_FACE",FACE,{"disambiguationData":[OSD([sQuery(id+"F0.wireOp",EDGE,"E0.bottom"),sQuery(id+"F0.wireOp",EDGE,"E1.bottom"),sQuery(id+"F0.wireOp",EDGE,"E2.bottom"),sQuery(id+"F4.wireOp",EDGE,"E37"),sQuery(id+"F4.wireOp",EDGE,"E40"),sQuery(id+"F4.wireOp",EDGE,"E41")])],"isStart":false})]})]});}
            var Q71;
            {var subQ0=sQuery(id+"F4.wireOp",EDGE,"E59");var subQ1=sQuery(id+"F0.wireOp",EDGE,"E10");var subQ2=sQuery(id+"F0.wireOp",EDGE,"E9");var subQ3=sQuery(id+"F0.wireOp",EDGE,"E8");var subQ4=sQuery(id+"F0.wireOp",EDGE,"E7");var subQ5=sQuery(id+"F0.wireOp",EDGE,"E0.top");Q71=makeQuery(id+"F12.boolean.opBoolean","INTERSECT",EDGE,{"derivedFrom":[makeQuery(id+"F5.boolean.opBoolean","MERGE",FACE,{"derivedFrom":[makeQuery(id+"F3.boolean.opBoolean","MERGE",FACE,{"derivedFrom":[makeQuery(id+"F2.boolean.opBoolean","MERGE",FACE,{"derivedFrom":[makeQuery(id+"F1.opExtrude","SWEPT_FACE",FACE,{"disambiguationData":[OSD([subQ5])]}),makeQuery(id+"F2.opExtrude","SWEPT_FACE",FACE,{"disambiguationData":[OSD([subQ5,subQ4,subQ3,subQ2,subQ1])]})]}),makeQuery(id+"F3.opExtrude","SWEPT_FACE",FACE,{"disambiguationData":[OSD([subQ5,subQ4,subQ3,subQ2,subQ1,sQuery(id+"F0.wireOp",EDGE,"E11"),sQuery(id+"F0.wireOp",EDGE,"E12")])]})]}),makeQuery(id+"F5.opExtrude","CAP_FACE",FACE,{"disambiguationData":[OSD([sQuery(id+"F0.wireOp",EDGE,"E0.bottom"),sQuery(id+"F0.wireOp",EDGE,"E1.bottom"),sQuery(id+"F0.wireOp",EDGE,"E2.bottom"),sQuery(id+"F4.wireOp",EDGE,"E37"),sQuery(id+"F4.wireOp",EDGE,"E40"),sQuery(id+"F4.wireOp",EDGE,"E41")])],"isStart":false})]}),makeQuery(id+"F12.opExtrude","SWEPT_FACE",FACE,{"disambiguationData":[OSD([subQ0]),TDD([makeQuery(id+"F4.imprint","IMPRINT",EDGE,{"disambiguationData":[TD([[makeQuery(id+"F4.imprint","INTERSECT",VERTEX,{"derivedFrom":[subQ0,sQuery(id+"F4.wireOp",EDGE,"E65")]}),-1.0]])],"derivedFrom":subQ0})])]})]});}
            var Q72;
            {var subQ0=sQuery(id+"F0.wireOp",EDGE,"E10");var subQ1=sQuery(id+"F0.wireOp",EDGE,"E9");var subQ2=sQuery(id+"F0.wireOp",EDGE,"E8");var subQ3=sQuery(id+"F0.wireOp",EDGE,"E7");var subQ4=sQuery(id+"F0.wireOp",EDGE,"E0.top");Q72=makeQuery(id+"F13.opFillet","BLEND_EDGE",EDGE,{"blendedFrom":[makeQuery(id+"F12.boolean.opBoolean","COPY",EDGE,{"derivedFrom":makeQuery(id+"F12.opExtrude","SWEPT_EDGE",EDGE,{"disambiguationData":[OSD([sQuery(id+"F4.wireOp",EDGE,"E59"),sQuery(id+"F4.wireOp",EDGE,"E65")])]})}),makeQuery(id+"F5.boolean.opBoolean","MERGE",FACE,{"derivedFrom":[makeQuery(id+"F3.boolean.opBoolean","MERGE",FACE,{"derivedFrom":[makeQuery(id+"F2.boolean.opBoolean","MERGE",FACE,{"derivedFrom":[makeQuery(id+"F1.opExtrude","SWEPT_FACE",FACE,{"disambiguationData":[OSD([subQ4])]}),makeQuery(id+"F2.opExtrude","SWEPT_FACE",FACE,{"disambiguationData":[OSD([subQ4,subQ3,subQ2,subQ1,subQ0])]})]}),makeQuery(id+"F3.opExtrude","SWEPT_FACE",FACE,{"disambiguationData":[OSD([subQ4,subQ3,subQ2,subQ1,subQ0,sQuery(id+"F0.wireOp",EDGE,"E11"),sQuery(id+"F0.wireOp",EDGE,"E12")])]})]}),makeQuery(id+"F5.opExtrude","CAP_FACE",FACE,{"disambiguationData":[OSD([sQuery(id+"F0.wireOp",EDGE,"E0.bottom"),sQuery(id+"F0.wireOp",EDGE,"E1.bottom"),sQuery(id+"F0.wireOp",EDGE,"E2.bottom"),sQuery(id+"F4.wireOp",EDGE,"E37"),sQuery(id+"F4.wireOp",EDGE,"E40"),sQuery(id+"F4.wireOp",EDGE,"E41")])],"isStart":false})]})],"blendedInto":[makeQuery(id+"F5.boolean.opBoolean","MERGE",FACE,{"derivedFrom":[makeQuery(id+"F3.boolean.opBoolean","MERGE",FACE,{"derivedFrom":[makeQuery(id+"F2.boolean.opBoolean","MERGE",FACE,{"derivedFrom":[makeQuery(id+"F1.opExtrude","SWEPT_FACE",FACE,{"disambiguationData":[OSD([subQ4])]}),makeQuery(id+"F2.opExtrude","SWEPT_FACE",FACE,{"disambiguationData":[OSD([subQ4,subQ3,subQ2,subQ1,subQ0])]})]}),makeQuery(id+"F3.opExtrude","SWEPT_FACE",FACE,{"disambiguationData":[OSD([subQ4,subQ3,subQ2,subQ1,subQ0,sQuery(id+"F0.wireOp",EDGE,"E11"),sQuery(id+"F0.wireOp",EDGE,"E12")])]})]}),makeQuery(id+"F5.opExtrude","CAP_FACE",FACE,{"disambiguationData":[OSD([sQuery(id+"F0.wireOp",EDGE,"E0.bottom"),sQuery(id+"F0.wireOp",EDGE,"E1.bottom"),sQuery(id+"F0.wireOp",EDGE,"E2.bottom"),sQuery(id+"F4.wireOp",EDGE,"E37"),sQuery(id+"F4.wireOp",EDGE,"E40"),sQuery(id+"F4.wireOp",EDGE,"E41")])],"isStart":false})]})]});}
            var Q73;
            {var subQ0=sQuery(id+"F0.wireOp",EDGE,"E10");var subQ1=sQuery(id+"F0.wireOp",EDGE,"E9");var subQ2=sQuery(id+"F0.wireOp",EDGE,"E8");var subQ3=sQuery(id+"F0.wireOp",EDGE,"E7");var subQ4=sQuery(id+"F0.wireOp",EDGE,"E0.top");Q73=makeQuery(id+"F12.boolean.opBoolean","INTERSECT",EDGE,{"derivedFrom":[makeQuery(id+"F5.boolean.opBoolean","MERGE",FACE,{"derivedFrom":[makeQuery(id+"F3.boolean.opBoolean","MERGE",FACE,{"derivedFrom":[makeQuery(id+"F2.boolean.opBoolean","MERGE",FACE,{"derivedFrom":[makeQuery(id+"F1.opExtrude","SWEPT_FACE",FACE,{"disambiguationData":[OSD([subQ4])]}),makeQuery(id+"F2.opExtrude","SWEPT_FACE",FACE,{"disambiguationData":[OSD([subQ4,subQ3,subQ2,subQ1,subQ0])]})]}),makeQuery(id+"F3.opExtrude","SWEPT_FACE",FACE,{"disambiguationData":[OSD([subQ4,subQ3,subQ2,subQ1,subQ0,sQuery(id+"F0.wireOp",EDGE,"E11"),sQuery(id+"F0.wireOp",EDGE,"E12")])]})]}),makeQuery(id+"F5.opExtrude","CAP_FACE",FACE,{"disambiguationData":[OSD([sQuery(id+"F0.wireOp",EDGE,"E0.bottom"),sQuery(id+"F0.wireOp",EDGE,"E1.bottom"),sQuery(id+"F0.wireOp",EDGE,"E2.bottom"),sQuery(id+"F4.wireOp",EDGE,"E37"),sQuery(id+"F4.wireOp",EDGE,"E40"),sQuery(id+"F4.wireOp",EDGE,"E41")])],"isStart":false})]}),makeQuery(id+"F12.opExtrude","SWEPT_FACE",FACE,{"disambiguationData":[OSD([sQuery(id+"F4.wireOp",EDGE,"E65")])]})]});}
            var Q74;
            {var subQ0=sQuery(id+"F0.wireOp",EDGE,"E2.bottom");var subQ1=sQuery(id+"F0.wireOp",EDGE,"E1.bottom");var subQ2=sQuery(id+"F0.wireOp",EDGE,"E0.bottom");var subQ3=sQuery(id+"F0.wireOp",EDGE,"E10");var subQ4=sQuery(id+"F0.wireOp",EDGE,"E9");var subQ5=sQuery(id+"F0.wireOp",EDGE,"E8");var subQ6=sQuery(id+"F0.wireOp",EDGE,"E7");var subQ7=sQuery(id+"F0.wireOp",EDGE,"E0.top");Q74=makeQuery(id+"F13.opFillet","BLEND_EDGE",EDGE,{"blendedFrom":[makeQuery(id+"F12.boolean.opBoolean","COPY",EDGE,{"derivedFrom":makeQuery(id+"F12.opExtrude","SWEPT_EDGE",EDGE,{"disambiguationData":[OSD([subQ2,subQ1,subQ0,sQuery(id+"F4.wireOp",EDGE,"E65")])]})}),makeQuery(id+"F5.boolean.opBoolean","MERGE",FACE,{"derivedFrom":[makeQuery(id+"F3.boolean.opBoolean","MERGE",FACE,{"derivedFrom":[makeQuery(id+"F2.boolean.opBoolean","MERGE",FACE,{"derivedFrom":[makeQuery(id+"F1.opExtrude","SWEPT_FACE",FACE,{"disambiguationData":[OSD([subQ7])]}),makeQuery(id+"F2.opExtrude","SWEPT_FACE",FACE,{"disambiguationData":[OSD([subQ7,subQ6,subQ5,subQ4,subQ3])]})]}),makeQuery(id+"F3.opExtrude","SWEPT_FACE",FACE,{"disambiguationData":[OSD([subQ7,subQ6,subQ5,subQ4,subQ3,sQuery(id+"F0.wireOp",EDGE,"E11"),sQuery(id+"F0.wireOp",EDGE,"E12")])]})]}),makeQuery(id+"F5.opExtrude","CAP_FACE",FACE,{"disambiguationData":[OSD([subQ2,subQ1,subQ0,sQuery(id+"F4.wireOp",EDGE,"E37"),sQuery(id+"F4.wireOp",EDGE,"E40"),sQuery(id+"F4.wireOp",EDGE,"E41")])],"isStart":false})]})],"blendedInto":[makeQuery(id+"F5.boolean.opBoolean","MERGE",FACE,{"derivedFrom":[makeQuery(id+"F3.boolean.opBoolean","MERGE",FACE,{"derivedFrom":[makeQuery(id+"F2.boolean.opBoolean","MERGE",FACE,{"derivedFrom":[makeQuery(id+"F1.opExtrude","SWEPT_FACE",FACE,{"disambiguationData":[OSD([subQ7])]}),makeQuery(id+"F2.opExtrude","SWEPT_FACE",FACE,{"disambiguationData":[OSD([subQ7,subQ6,subQ5,subQ4,subQ3])]})]}),makeQuery(id+"F3.opExtrude","SWEPT_FACE",FACE,{"disambiguationData":[OSD([subQ7,subQ6,subQ5,subQ4,subQ3,sQuery(id+"F0.wireOp",EDGE,"E11"),sQuery(id+"F0.wireOp",EDGE,"E12")])]})]}),makeQuery(id+"F5.opExtrude","CAP_FACE",FACE,{"disambiguationData":[OSD([subQ2,subQ1,subQ0,sQuery(id+"F4.wireOp",EDGE,"E37"),sQuery(id+"F4.wireOp",EDGE,"E40"),sQuery(id+"F4.wireOp",EDGE,"E41")])],"isStart":false})]})]});}
            var Q75;
            {var subQ0=sQuery(id+"F0.wireOp",EDGE,"E2.bottom");var subQ1=sQuery(id+"F0.wireOp",EDGE,"E1.bottom");var subQ2=sQuery(id+"F0.wireOp",EDGE,"E0.bottom");var subQ3=sQuery(id+"F0.wireOp",EDGE,"E10");var subQ4=sQuery(id+"F0.wireOp",EDGE,"E9");var subQ5=sQuery(id+"F0.wireOp",EDGE,"E8");var subQ6=sQuery(id+"F0.wireOp",EDGE,"E7");var subQ7=sQuery(id+"F0.wireOp",EDGE,"E0.top");Q75=makeQuery(id+"F13.opFillet","BLEND_EDGE",EDGE,{"blendedFrom":[makeQuery(id+"F12.boolean.opBoolean","COPY",EDGE,{"derivedFrom":makeQuery(id+"F12.opExtrude","SWEPT_EDGE",EDGE,{"disambiguationData":[OSD([subQ2,subQ1,subQ0,sQuery(id+"F4.wireOp",EDGE,"E64")])]})}),makeQuery(id+"F5.boolean.opBoolean","MERGE",FACE,{"derivedFrom":[makeQuery(id+"F3.boolean.opBoolean","MERGE",FACE,{"derivedFrom":[makeQuery(id+"F2.boolean.opBoolean","MERGE",FACE,{"derivedFrom":[makeQuery(id+"F1.opExtrude","SWEPT_FACE",FACE,{"disambiguationData":[OSD([subQ7])]}),makeQuery(id+"F2.opExtrude","SWEPT_FACE",FACE,{"disambiguationData":[OSD([subQ7,subQ6,subQ5,subQ4,subQ3])]})]}),makeQuery(id+"F3.opExtrude","SWEPT_FACE",FACE,{"disambiguationData":[OSD([subQ7,subQ6,subQ5,subQ4,subQ3,sQuery(id+"F0.wireOp",EDGE,"E11"),sQuery(id+"F0.wireOp",EDGE,"E12")])]})]}),makeQuery(id+"F5.opExtrude","CAP_FACE",FACE,{"disambiguationData":[OSD([subQ2,subQ1,subQ0,sQuery(id+"F4.wireOp",EDGE,"E37"),sQuery(id+"F4.wireOp",EDGE,"E40"),sQuery(id+"F4.wireOp",EDGE,"E41")])],"isStart":false})]})],"blendedInto":[makeQuery(id+"F5.boolean.opBoolean","MERGE",FACE,{"derivedFrom":[makeQuery(id+"F3.boolean.opBoolean","MERGE",FACE,{"derivedFrom":[makeQuery(id+"F2.boolean.opBoolean","MERGE",FACE,{"derivedFrom":[makeQuery(id+"F1.opExtrude","SWEPT_FACE",FACE,{"disambiguationData":[OSD([subQ7])]}),makeQuery(id+"F2.opExtrude","SWEPT_FACE",FACE,{"disambiguationData":[OSD([subQ7,subQ6,subQ5,subQ4,subQ3])]})]}),makeQuery(id+"F3.opExtrude","SWEPT_FACE",FACE,{"disambiguationData":[OSD([subQ7,subQ6,subQ5,subQ4,subQ3,sQuery(id+"F0.wireOp",EDGE,"E11"),sQuery(id+"F0.wireOp",EDGE,"E12")])]})]}),makeQuery(id+"F5.opExtrude","CAP_FACE",FACE,{"disambiguationData":[OSD([subQ2,subQ1,subQ0,sQuery(id+"F4.wireOp",EDGE,"E37"),sQuery(id+"F4.wireOp",EDGE,"E40"),sQuery(id+"F4.wireOp",EDGE,"E41")])],"isStart":false})]})]});}
            var Q76;
            {var subQ0=sQuery(id+"F0.wireOp",EDGE,"E10");var subQ1=sQuery(id+"F0.wireOp",EDGE,"E9");var subQ2=sQuery(id+"F0.wireOp",EDGE,"E8");var subQ3=sQuery(id+"F0.wireOp",EDGE,"E7");var subQ4=sQuery(id+"F0.wireOp",EDGE,"E0.top");Q76=makeQuery(id+"F12.boolean.opBoolean","INTERSECT",EDGE,{"derivedFrom":[makeQuery(id+"F5.boolean.opBoolean","MERGE",FACE,{"derivedFrom":[makeQuery(id+"F3.boolean.opBoolean","MERGE",FACE,{"derivedFrom":[makeQuery(id+"F2.boolean.opBoolean","MERGE",FACE,{"derivedFrom":[makeQuery(id+"F1.opExtrude","SWEPT_FACE",FACE,{"disambiguationData":[OSD([subQ4])]}),makeQuery(id+"F2.opExtrude","SWEPT_FACE",FACE,{"disambiguationData":[OSD([subQ4,subQ3,subQ2,subQ1,subQ0])]})]}),makeQuery(id+"F3.opExtrude","SWEPT_FACE",FACE,{"disambiguationData":[OSD([subQ4,subQ3,subQ2,subQ1,subQ0,sQuery(id+"F0.wireOp",EDGE,"E11"),sQuery(id+"F0.wireOp",EDGE,"E12")])]})]}),makeQuery(id+"F5.opExtrude","CAP_FACE",FACE,{"disambiguationData":[OSD([sQuery(id+"F0.wireOp",EDGE,"E0.bottom"),sQuery(id+"F0.wireOp",EDGE,"E1.bottom"),sQuery(id+"F0.wireOp",EDGE,"E2.bottom"),sQuery(id+"F4.wireOp",EDGE,"E37"),sQuery(id+"F4.wireOp",EDGE,"E40"),sQuery(id+"F4.wireOp",EDGE,"E41")])],"isStart":false})]}),makeQuery(id+"F12.opExtrude","SWEPT_FACE",FACE,{"disambiguationData":[OSD([sQuery(id+"F4.wireOp",EDGE,"E64")])]})]});}
            var Q77;
            {var subQ0=sQuery(id+"F0.wireOp",EDGE,"E10");var subQ1=sQuery(id+"F0.wireOp",EDGE,"E9");var subQ2=sQuery(id+"F0.wireOp",EDGE,"E8");var subQ3=sQuery(id+"F0.wireOp",EDGE,"E7");var subQ4=sQuery(id+"F0.wireOp",EDGE,"E0.top");Q77=makeQuery(id+"F13.opFillet","BLEND_EDGE",EDGE,{"blendedFrom":[makeQuery(id+"F12.boolean.opBoolean","COPY",EDGE,{"derivedFrom":makeQuery(id+"F12.opExtrude","SWEPT_EDGE",EDGE,{"disambiguationData":[OSD([sQuery(id+"F4.wireOp",EDGE,"E59"),sQuery(id+"F4.wireOp",EDGE,"E64")])]})}),makeQuery(id+"F5.boolean.opBoolean","MERGE",FACE,{"derivedFrom":[makeQuery(id+"F3.boolean.opBoolean","MERGE",FACE,{"derivedFrom":[makeQuery(id+"F2.boolean.opBoolean","MERGE",FACE,{"derivedFrom":[makeQuery(id+"F1.opExtrude","SWEPT_FACE",FACE,{"disambiguationData":[OSD([subQ4])]}),makeQuery(id+"F2.opExtrude","SWEPT_FACE",FACE,{"disambiguationData":[OSD([subQ4,subQ3,subQ2,subQ1,subQ0])]})]}),makeQuery(id+"F3.opExtrude","SWEPT_FACE",FACE,{"disambiguationData":[OSD([subQ4,subQ3,subQ2,subQ1,subQ0,sQuery(id+"F0.wireOp",EDGE,"E11"),sQuery(id+"F0.wireOp",EDGE,"E12")])]})]}),makeQuery(id+"F5.opExtrude","CAP_FACE",FACE,{"disambiguationData":[OSD([sQuery(id+"F0.wireOp",EDGE,"E0.bottom"),sQuery(id+"F0.wireOp",EDGE,"E1.bottom"),sQuery(id+"F0.wireOp",EDGE,"E2.bottom"),sQuery(id+"F4.wireOp",EDGE,"E37"),sQuery(id+"F4.wireOp",EDGE,"E40"),sQuery(id+"F4.wireOp",EDGE,"E41")])],"isStart":false})]})],"blendedInto":[makeQuery(id+"F5.boolean.opBoolean","MERGE",FACE,{"derivedFrom":[makeQuery(id+"F3.boolean.opBoolean","MERGE",FACE,{"derivedFrom":[makeQuery(id+"F2.boolean.opBoolean","MERGE",FACE,{"derivedFrom":[makeQuery(id+"F1.opExtrude","SWEPT_FACE",FACE,{"disambiguationData":[OSD([subQ4])]}),makeQuery(id+"F2.opExtrude","SWEPT_FACE",FACE,{"disambiguationData":[OSD([subQ4,subQ3,subQ2,subQ1,subQ0])]})]}),makeQuery(id+"F3.opExtrude","SWEPT_FACE",FACE,{"disambiguationData":[OSD([subQ4,subQ3,subQ2,subQ1,subQ0,sQuery(id+"F0.wireOp",EDGE,"E11"),sQuery(id+"F0.wireOp",EDGE,"E12")])]})]}),makeQuery(id+"F5.opExtrude","CAP_FACE",FACE,{"disambiguationData":[OSD([sQuery(id+"F0.wireOp",EDGE,"E0.bottom"),sQuery(id+"F0.wireOp",EDGE,"E1.bottom"),sQuery(id+"F0.wireOp",EDGE,"E2.bottom"),sQuery(id+"F4.wireOp",EDGE,"E37"),sQuery(id+"F4.wireOp",EDGE,"E40"),sQuery(id+"F4.wireOp",EDGE,"E41")])],"isStart":false})]})]});}
            var Q78;
            {var subQ0=sQuery(id+"F4.wireOp",EDGE,"E59");var subQ1=sQuery(id+"F0.wireOp",EDGE,"E10");var subQ2=sQuery(id+"F0.wireOp",EDGE,"E9");var subQ3=sQuery(id+"F0.wireOp",EDGE,"E8");var subQ4=sQuery(id+"F0.wireOp",EDGE,"E7");var subQ5=sQuery(id+"F0.wireOp",EDGE,"E0.top");Q78=makeQuery(id+"F12.boolean.opBoolean","INTERSECT",EDGE,{"derivedFrom":[makeQuery(id+"F5.boolean.opBoolean","MERGE",FACE,{"derivedFrom":[makeQuery(id+"F3.boolean.opBoolean","MERGE",FACE,{"derivedFrom":[makeQuery(id+"F2.boolean.opBoolean","MERGE",FACE,{"derivedFrom":[makeQuery(id+"F1.opExtrude","SWEPT_FACE",FACE,{"disambiguationData":[OSD([subQ5])]}),makeQuery(id+"F2.opExtrude","SWEPT_FACE",FACE,{"disambiguationData":[OSD([subQ5,subQ4,subQ3,subQ2,subQ1])]})]}),makeQuery(id+"F3.opExtrude","SWEPT_FACE",FACE,{"disambiguationData":[OSD([subQ5,subQ4,subQ3,subQ2,subQ1,sQuery(id+"F0.wireOp",EDGE,"E11"),sQuery(id+"F0.wireOp",EDGE,"E12")])]})]}),makeQuery(id+"F5.opExtrude","CAP_FACE",FACE,{"disambiguationData":[OSD([sQuery(id+"F0.wireOp",EDGE,"E0.bottom"),sQuery(id+"F0.wireOp",EDGE,"E1.bottom"),sQuery(id+"F0.wireOp",EDGE,"E2.bottom"),sQuery(id+"F4.wireOp",EDGE,"E37"),sQuery(id+"F4.wireOp",EDGE,"E40"),sQuery(id+"F4.wireOp",EDGE,"E41")])],"isStart":false})]}),makeQuery(id+"F12.opExtrude","SWEPT_FACE",FACE,{"disambiguationData":[OSD([subQ0]),TDD([makeQuery(id+"F4.imprint","IMPRINT",EDGE,{"disambiguationData":[TD([[makeQuery(id+"F4.imprint","INTERSECT",VERTEX,{"disambiguationData":[OD(0.0)],"derivedFrom":[subQ0,sQuery(id+"F4.wireOp",EDGE,"E66")]}),-1.0]])],"derivedFrom":subQ0})])]})]});}
            var Q79;
            {var subQ0=sQuery(id+"F0.wireOp",EDGE,"E10");var subQ1=sQuery(id+"F0.wireOp",EDGE,"E9");var subQ2=sQuery(id+"F0.wireOp",EDGE,"E8");var subQ3=sQuery(id+"F0.wireOp",EDGE,"E7");var subQ4=sQuery(id+"F0.wireOp",EDGE,"E0.top");var subQ5=sQuery(id+"F4.wireOp",EDGE,"E66");var subQ6=sQuery(id+"F4.wireOp",EDGE,"E59");Q79=makeQuery(id+"F13.opFillet","BLEND_EDGE",EDGE,{"blendedFrom":[makeQuery(id+"F12.boolean.opBoolean","COPY",EDGE,{"derivedFrom":makeQuery(id+"F12.opExtrude","SWEPT_EDGE",EDGE,{"disambiguationData":[OSD([subQ6,subQ5]),TDD([makeQuery(id+"F4.imprint","INTERSECT",VERTEX,{"disambiguationData":[OD(0.0)],"derivedFrom":[subQ6,subQ5]})])]})}),makeQuery(id+"F5.boolean.opBoolean","MERGE",FACE,{"derivedFrom":[makeQuery(id+"F3.boolean.opBoolean","MERGE",FACE,{"derivedFrom":[makeQuery(id+"F2.boolean.opBoolean","MERGE",FACE,{"derivedFrom":[makeQuery(id+"F1.opExtrude","SWEPT_FACE",FACE,{"disambiguationData":[OSD([subQ4])]}),makeQuery(id+"F2.opExtrude","SWEPT_FACE",FACE,{"disambiguationData":[OSD([subQ4,subQ3,subQ2,subQ1,subQ0])]})]}),makeQuery(id+"F3.opExtrude","SWEPT_FACE",FACE,{"disambiguationData":[OSD([subQ4,subQ3,subQ2,subQ1,subQ0,sQuery(id+"F0.wireOp",EDGE,"E11"),sQuery(id+"F0.wireOp",EDGE,"E12")])]})]}),makeQuery(id+"F5.opExtrude","CAP_FACE",FACE,{"disambiguationData":[OSD([sQuery(id+"F0.wireOp",EDGE,"E0.bottom"),sQuery(id+"F0.wireOp",EDGE,"E1.bottom"),sQuery(id+"F0.wireOp",EDGE,"E2.bottom"),sQuery(id+"F4.wireOp",EDGE,"E37"),sQuery(id+"F4.wireOp",EDGE,"E40"),sQuery(id+"F4.wireOp",EDGE,"E41")])],"isStart":false})]})],"blendedInto":[makeQuery(id+"F5.boolean.opBoolean","MERGE",FACE,{"derivedFrom":[makeQuery(id+"F3.boolean.opBoolean","MERGE",FACE,{"derivedFrom":[makeQuery(id+"F2.boolean.opBoolean","MERGE",FACE,{"derivedFrom":[makeQuery(id+"F1.opExtrude","SWEPT_FACE",FACE,{"disambiguationData":[OSD([subQ4])]}),makeQuery(id+"F2.opExtrude","SWEPT_FACE",FACE,{"disambiguationData":[OSD([subQ4,subQ3,subQ2,subQ1,subQ0])]})]}),makeQuery(id+"F3.opExtrude","SWEPT_FACE",FACE,{"disambiguationData":[OSD([subQ4,subQ3,subQ2,subQ1,subQ0,sQuery(id+"F0.wireOp",EDGE,"E11"),sQuery(id+"F0.wireOp",EDGE,"E12")])]})]}),makeQuery(id+"F5.opExtrude","CAP_FACE",FACE,{"disambiguationData":[OSD([sQuery(id+"F0.wireOp",EDGE,"E0.bottom"),sQuery(id+"F0.wireOp",EDGE,"E1.bottom"),sQuery(id+"F0.wireOp",EDGE,"E2.bottom"),sQuery(id+"F4.wireOp",EDGE,"E37"),sQuery(id+"F4.wireOp",EDGE,"E40"),sQuery(id+"F4.wireOp",EDGE,"E41")])],"isStart":false})]})]});}
            var Q80;
            {var subQ0=sQuery(id+"F4.wireOp",EDGE,"E66");var subQ1=sQuery(id+"F0.wireOp",EDGE,"E10");var subQ2=sQuery(id+"F0.wireOp",EDGE,"E9");var subQ3=sQuery(id+"F0.wireOp",EDGE,"E8");var subQ4=sQuery(id+"F0.wireOp",EDGE,"E7");var subQ5=sQuery(id+"F0.wireOp",EDGE,"E0.top");Q80=makeQuery(id+"F12.boolean.opBoolean","INTERSECT",EDGE,{"derivedFrom":[makeQuery(id+"F5.boolean.opBoolean","MERGE",FACE,{"derivedFrom":[makeQuery(id+"F3.boolean.opBoolean","MERGE",FACE,{"derivedFrom":[makeQuery(id+"F2.boolean.opBoolean","MERGE",FACE,{"derivedFrom":[makeQuery(id+"F1.opExtrude","SWEPT_FACE",FACE,{"disambiguationData":[OSD([subQ5])]}),makeQuery(id+"F2.opExtrude","SWEPT_FACE",FACE,{"disambiguationData":[OSD([subQ5,subQ4,subQ3,subQ2,subQ1])]})]}),makeQuery(id+"F3.opExtrude","SWEPT_FACE",FACE,{"disambiguationData":[OSD([subQ5,subQ4,subQ3,subQ2,subQ1,sQuery(id+"F0.wireOp",EDGE,"E11"),sQuery(id+"F0.wireOp",EDGE,"E12")])]})]}),makeQuery(id+"F5.opExtrude","CAP_FACE",FACE,{"disambiguationData":[OSD([sQuery(id+"F0.wireOp",EDGE,"E0.bottom"),sQuery(id+"F0.wireOp",EDGE,"E1.bottom"),sQuery(id+"F0.wireOp",EDGE,"E2.bottom"),sQuery(id+"F4.wireOp",EDGE,"E37"),sQuery(id+"F4.wireOp",EDGE,"E40"),sQuery(id+"F4.wireOp",EDGE,"E41")])],"isStart":false})]}),makeQuery(id+"F12.opExtrude","SWEPT_FACE",FACE,{"disambiguationData":[OSD([subQ0]),TDD([makeQuery(id+"F4.imprint","IMPRINT",EDGE,{"disambiguationData":[TD([[makeQuery(id+"F4.imprint","INTERSECT",VERTEX,{"disambiguationData":[OD(0.0)],"derivedFrom":[sQuery(id+"F4.wireOp",EDGE,"E59"),subQ0]}),1.0]])],"derivedFrom":subQ0})])]})]});}
            var Q81;
            {var subQ0=sQuery(id+"F0.wireOp",EDGE,"E10");var subQ1=sQuery(id+"F0.wireOp",EDGE,"E9");var subQ2=sQuery(id+"F0.wireOp",EDGE,"E8");var subQ3=sQuery(id+"F0.wireOp",EDGE,"E7");var subQ4=sQuery(id+"F0.wireOp",EDGE,"E0.top");Q81=makeQuery(id+"F13.opFillet","BLEND_EDGE",EDGE,{"blendedFrom":[makeQuery(id+"F12.boolean.opBoolean","COPY",EDGE,{"derivedFrom":makeQuery(id+"F12.opExtrude","SWEPT_EDGE",EDGE,{"disambiguationData":[OSD([sQuery(id+"F4.wireOp",EDGE,"E60"),sQuery(id+"F4.wireOp",EDGE,"E66")])]})}),makeQuery(id+"F5.boolean.opBoolean","MERGE",FACE,{"derivedFrom":[makeQuery(id+"F3.boolean.opBoolean","MERGE",FACE,{"derivedFrom":[makeQuery(id+"F2.boolean.opBoolean","MERGE",FACE,{"derivedFrom":[makeQuery(id+"F1.opExtrude","SWEPT_FACE",FACE,{"disambiguationData":[OSD([subQ4])]}),makeQuery(id+"F2.opExtrude","SWEPT_FACE",FACE,{"disambiguationData":[OSD([subQ4,subQ3,subQ2,subQ1,subQ0])]})]}),makeQuery(id+"F3.opExtrude","SWEPT_FACE",FACE,{"disambiguationData":[OSD([subQ4,subQ3,subQ2,subQ1,subQ0,sQuery(id+"F0.wireOp",EDGE,"E11"),sQuery(id+"F0.wireOp",EDGE,"E12")])]})]}),makeQuery(id+"F5.opExtrude","CAP_FACE",FACE,{"disambiguationData":[OSD([sQuery(id+"F0.wireOp",EDGE,"E0.bottom"),sQuery(id+"F0.wireOp",EDGE,"E1.bottom"),sQuery(id+"F0.wireOp",EDGE,"E2.bottom"),sQuery(id+"F4.wireOp",EDGE,"E37"),sQuery(id+"F4.wireOp",EDGE,"E40"),sQuery(id+"F4.wireOp",EDGE,"E41")])],"isStart":false})]})],"blendedInto":[makeQuery(id+"F5.boolean.opBoolean","MERGE",FACE,{"derivedFrom":[makeQuery(id+"F3.boolean.opBoolean","MERGE",FACE,{"derivedFrom":[makeQuery(id+"F2.boolean.opBoolean","MERGE",FACE,{"derivedFrom":[makeQuery(id+"F1.opExtrude","SWEPT_FACE",FACE,{"disambiguationData":[OSD([subQ4])]}),makeQuery(id+"F2.opExtrude","SWEPT_FACE",FACE,{"disambiguationData":[OSD([subQ4,subQ3,subQ2,subQ1,subQ0])]})]}),makeQuery(id+"F3.opExtrude","SWEPT_FACE",FACE,{"disambiguationData":[OSD([subQ4,subQ3,subQ2,subQ1,subQ0,sQuery(id+"F0.wireOp",EDGE,"E11"),sQuery(id+"F0.wireOp",EDGE,"E12")])]})]}),makeQuery(id+"F5.opExtrude","CAP_FACE",FACE,{"disambiguationData":[OSD([sQuery(id+"F0.wireOp",EDGE,"E0.bottom"),sQuery(id+"F0.wireOp",EDGE,"E1.bottom"),sQuery(id+"F0.wireOp",EDGE,"E2.bottom"),sQuery(id+"F4.wireOp",EDGE,"E37"),sQuery(id+"F4.wireOp",EDGE,"E40"),sQuery(id+"F4.wireOp",EDGE,"E41")])],"isStart":false})]})]});}
            var Q82;
            {var subQ0=sQuery(id+"F0.wireOp",EDGE,"E10");var subQ1=sQuery(id+"F0.wireOp",EDGE,"E9");var subQ2=sQuery(id+"F0.wireOp",EDGE,"E8");var subQ3=sQuery(id+"F0.wireOp",EDGE,"E7");var subQ4=sQuery(id+"F0.wireOp",EDGE,"E0.top");Q82=makeQuery(id+"F12.boolean.opBoolean","INTERSECT",EDGE,{"derivedFrom":[makeQuery(id+"F5.boolean.opBoolean","MERGE",FACE,{"derivedFrom":[makeQuery(id+"F3.boolean.opBoolean","MERGE",FACE,{"derivedFrom":[makeQuery(id+"F2.boolean.opBoolean","MERGE",FACE,{"derivedFrom":[makeQuery(id+"F1.opExtrude","SWEPT_FACE",FACE,{"disambiguationData":[OSD([subQ4])]}),makeQuery(id+"F2.opExtrude","SWEPT_FACE",FACE,{"disambiguationData":[OSD([subQ4,subQ3,subQ2,subQ1,subQ0])]})]}),makeQuery(id+"F3.opExtrude","SWEPT_FACE",FACE,{"disambiguationData":[OSD([subQ4,subQ3,subQ2,subQ1,subQ0,sQuery(id+"F0.wireOp",EDGE,"E11"),sQuery(id+"F0.wireOp",EDGE,"E12")])]})]}),makeQuery(id+"F5.opExtrude","CAP_FACE",FACE,{"disambiguationData":[OSD([sQuery(id+"F0.wireOp",EDGE,"E0.bottom"),sQuery(id+"F0.wireOp",EDGE,"E1.bottom"),sQuery(id+"F0.wireOp",EDGE,"E2.bottom"),sQuery(id+"F4.wireOp",EDGE,"E37"),sQuery(id+"F4.wireOp",EDGE,"E40"),sQuery(id+"F4.wireOp",EDGE,"E41")])],"isStart":false})]}),makeQuery(id+"F12.opExtrude","SWEPT_FACE",FACE,{"disambiguationData":[OSD([sQuery(id+"F4.wireOp",EDGE,"E60")])]})]});}
            var Q83;
            {var subQ0=sQuery(id+"F0.wireOp",EDGE,"E10");var subQ1=sQuery(id+"F0.wireOp",EDGE,"E9");var subQ2=sQuery(id+"F0.wireOp",EDGE,"E8");var subQ3=sQuery(id+"F0.wireOp",EDGE,"E7");var subQ4=sQuery(id+"F0.wireOp",EDGE,"E0.top");Q83=makeQuery(id+"F13.opFillet","BLEND_EDGE",EDGE,{"blendedFrom":[makeQuery(id+"F12.boolean.opBoolean","COPY",EDGE,{"derivedFrom":makeQuery(id+"F12.opExtrude","SWEPT_EDGE",EDGE,{"disambiguationData":[OSD([sQuery(id+"F4.wireOp",EDGE,"E60"),sQuery(id+"F4.wireOp",EDGE,"E62")])]})}),makeQuery(id+"F5.boolean.opBoolean","MERGE",FACE,{"derivedFrom":[makeQuery(id+"F3.boolean.opBoolean","MERGE",FACE,{"derivedFrom":[makeQuery(id+"F2.boolean.opBoolean","MERGE",FACE,{"derivedFrom":[makeQuery(id+"F1.opExtrude","SWEPT_FACE",FACE,{"disambiguationData":[OSD([subQ4])]}),makeQuery(id+"F2.opExtrude","SWEPT_FACE",FACE,{"disambiguationData":[OSD([subQ4,subQ3,subQ2,subQ1,subQ0])]})]}),makeQuery(id+"F3.opExtrude","SWEPT_FACE",FACE,{"disambiguationData":[OSD([subQ4,subQ3,subQ2,subQ1,subQ0,sQuery(id+"F0.wireOp",EDGE,"E11"),sQuery(id+"F0.wireOp",EDGE,"E12")])]})]}),makeQuery(id+"F5.opExtrude","CAP_FACE",FACE,{"disambiguationData":[OSD([sQuery(id+"F0.wireOp",EDGE,"E0.bottom"),sQuery(id+"F0.wireOp",EDGE,"E1.bottom"),sQuery(id+"F0.wireOp",EDGE,"E2.bottom"),sQuery(id+"F4.wireOp",EDGE,"E37"),sQuery(id+"F4.wireOp",EDGE,"E40"),sQuery(id+"F4.wireOp",EDGE,"E41")])],"isStart":false})]})],"blendedInto":[makeQuery(id+"F5.boolean.opBoolean","MERGE",FACE,{"derivedFrom":[makeQuery(id+"F3.boolean.opBoolean","MERGE",FACE,{"derivedFrom":[makeQuery(id+"F2.boolean.opBoolean","MERGE",FACE,{"derivedFrom":[makeQuery(id+"F1.opExtrude","SWEPT_FACE",FACE,{"disambiguationData":[OSD([subQ4])]}),makeQuery(id+"F2.opExtrude","SWEPT_FACE",FACE,{"disambiguationData":[OSD([subQ4,subQ3,subQ2,subQ1,subQ0])]})]}),makeQuery(id+"F3.opExtrude","SWEPT_FACE",FACE,{"disambiguationData":[OSD([subQ4,subQ3,subQ2,subQ1,subQ0,sQuery(id+"F0.wireOp",EDGE,"E11"),sQuery(id+"F0.wireOp",EDGE,"E12")])]})]}),makeQuery(id+"F5.opExtrude","CAP_FACE",FACE,{"disambiguationData":[OSD([sQuery(id+"F0.wireOp",EDGE,"E0.bottom"),sQuery(id+"F0.wireOp",EDGE,"E1.bottom"),sQuery(id+"F0.wireOp",EDGE,"E2.bottom"),sQuery(id+"F4.wireOp",EDGE,"E37"),sQuery(id+"F4.wireOp",EDGE,"E40"),sQuery(id+"F4.wireOp",EDGE,"E41")])],"isStart":false})]})]});}
            var Q84;
            {var subQ0=sQuery(id+"F0.wireOp",EDGE,"E10");var subQ1=sQuery(id+"F0.wireOp",EDGE,"E9");var subQ2=sQuery(id+"F0.wireOp",EDGE,"E8");var subQ3=sQuery(id+"F0.wireOp",EDGE,"E7");var subQ4=sQuery(id+"F0.wireOp",EDGE,"E0.top");Q84=makeQuery(id+"F12.boolean.opBoolean","INTERSECT",EDGE,{"derivedFrom":[makeQuery(id+"F5.boolean.opBoolean","MERGE",FACE,{"derivedFrom":[makeQuery(id+"F3.boolean.opBoolean","MERGE",FACE,{"derivedFrom":[makeQuery(id+"F2.boolean.opBoolean","MERGE",FACE,{"derivedFrom":[makeQuery(id+"F1.opExtrude","SWEPT_FACE",FACE,{"disambiguationData":[OSD([subQ4])]}),makeQuery(id+"F2.opExtrude","SWEPT_FACE",FACE,{"disambiguationData":[OSD([subQ4,subQ3,subQ2,subQ1,subQ0])]})]}),makeQuery(id+"F3.opExtrude","SWEPT_FACE",FACE,{"disambiguationData":[OSD([subQ4,subQ3,subQ2,subQ1,subQ0,sQuery(id+"F0.wireOp",EDGE,"E11"),sQuery(id+"F0.wireOp",EDGE,"E12")])]})]}),makeQuery(id+"F5.opExtrude","CAP_FACE",FACE,{"disambiguationData":[OSD([sQuery(id+"F0.wireOp",EDGE,"E0.bottom"),sQuery(id+"F0.wireOp",EDGE,"E1.bottom"),sQuery(id+"F0.wireOp",EDGE,"E2.bottom"),sQuery(id+"F4.wireOp",EDGE,"E37"),sQuery(id+"F4.wireOp",EDGE,"E40"),sQuery(id+"F4.wireOp",EDGE,"E41")])],"isStart":false})]}),makeQuery(id+"F12.opExtrude","SWEPT_FACE",FACE,{"disambiguationData":[OSD([sQuery(id+"F4.wireOp",EDGE,"E62")])]})]});}
            var Q85;
            {var subQ0=sQuery(id+"F0.wireOp",EDGE,"E2.bottom");var subQ1=sQuery(id+"F0.wireOp",EDGE,"E1.bottom");var subQ2=sQuery(id+"F0.wireOp",EDGE,"E0.bottom");var subQ3=sQuery(id+"F0.wireOp",EDGE,"E10");var subQ4=sQuery(id+"F0.wireOp",EDGE,"E9");var subQ5=sQuery(id+"F0.wireOp",EDGE,"E8");var subQ6=sQuery(id+"F0.wireOp",EDGE,"E7");var subQ7=sQuery(id+"F0.wireOp",EDGE,"E0.top");Q85=makeQuery(id+"F13.opFillet","BLEND_EDGE",EDGE,{"blendedFrom":[makeQuery(id+"F12.boolean.opBoolean","COPY",EDGE,{"derivedFrom":makeQuery(id+"F12.opExtrude","SWEPT_EDGE",EDGE,{"disambiguationData":[OSD([subQ2,subQ1,subQ0,sQuery(id+"F4.wireOp",EDGE,"E62")])]})}),makeQuery(id+"F5.boolean.opBoolean","MERGE",FACE,{"derivedFrom":[makeQuery(id+"F3.boolean.opBoolean","MERGE",FACE,{"derivedFrom":[makeQuery(id+"F2.boolean.opBoolean","MERGE",FACE,{"derivedFrom":[makeQuery(id+"F1.opExtrude","SWEPT_FACE",FACE,{"disambiguationData":[OSD([subQ7])]}),makeQuery(id+"F2.opExtrude","SWEPT_FACE",FACE,{"disambiguationData":[OSD([subQ7,subQ6,subQ5,subQ4,subQ3])]})]}),makeQuery(id+"F3.opExtrude","SWEPT_FACE",FACE,{"disambiguationData":[OSD([subQ7,subQ6,subQ5,subQ4,subQ3,sQuery(id+"F0.wireOp",EDGE,"E11"),sQuery(id+"F0.wireOp",EDGE,"E12")])]})]}),makeQuery(id+"F5.opExtrude","CAP_FACE",FACE,{"disambiguationData":[OSD([subQ2,subQ1,subQ0,sQuery(id+"F4.wireOp",EDGE,"E37"),sQuery(id+"F4.wireOp",EDGE,"E40"),sQuery(id+"F4.wireOp",EDGE,"E41")])],"isStart":false})]})],"blendedInto":[makeQuery(id+"F5.boolean.opBoolean","MERGE",FACE,{"derivedFrom":[makeQuery(id+"F3.boolean.opBoolean","MERGE",FACE,{"derivedFrom":[makeQuery(id+"F2.boolean.opBoolean","MERGE",FACE,{"derivedFrom":[makeQuery(id+"F1.opExtrude","SWEPT_FACE",FACE,{"disambiguationData":[OSD([subQ7])]}),makeQuery(id+"F2.opExtrude","SWEPT_FACE",FACE,{"disambiguationData":[OSD([subQ7,subQ6,subQ5,subQ4,subQ3])]})]}),makeQuery(id+"F3.opExtrude","SWEPT_FACE",FACE,{"disambiguationData":[OSD([subQ7,subQ6,subQ5,subQ4,subQ3,sQuery(id+"F0.wireOp",EDGE,"E11"),sQuery(id+"F0.wireOp",EDGE,"E12")])]})]}),makeQuery(id+"F5.opExtrude","CAP_FACE",FACE,{"disambiguationData":[OSD([subQ2,subQ1,subQ0,sQuery(id+"F4.wireOp",EDGE,"E37"),sQuery(id+"F4.wireOp",EDGE,"E40"),sQuery(id+"F4.wireOp",EDGE,"E41")])],"isStart":false})]})]});}
            chamfer(context, id + "F15", {"entities" : qUnion([Q0, Q1, Q2, Q3, Q4, Q5, Q6, Q7, Q8, Q9, Q10, Q11, Q12, Q13, Q14, Q15, Q16, Q17, Q18, Q19, Q20, Q21, Q22, Q23, Q24, Q25, Q26, Q27, Q28, Q29, Q30, Q31, Q32, Q33, Q34, Q35, Q36, Q37, Q38, Q39, Q40, Q41, Q42, Q43, Q44, Q45, Q46, Q47, Q48, Q49, Q50, Q51, Q52, Q53, Q54, Q55, Q56, Q57, Q58, Q59, Q60, Q61, Q62, Q63, Q64, Q65, Q66, Q67, Q68, Q69, Q70, Q71, Q72, Q73, Q74, Q75, Q76, Q77, Q78, Q79, Q80, Q81, Q82, Q83, Q84, Q85]), "width" : 1 * mm});
        }
        {
            var Q0;
            Q0=makeQuery(id+"F9.boolean.opBoolean","COPY",FACE,{"derivedFrom":makeQuery(id+"F9.opExtrude","SWEPT_FACE",FACE,{"disambiguationData":[OSD([sQuery(id+"F4.wireOp",EDGE,"E53")])]})});
            var sketch = newSketch(context, id + "F16", { "sketchPlane" : qUnion([Q0])});
            skLineSegment(sketch, "E68", {"start": v(-21.27, -6) * mm, "end": v(-26, -6) * mm});
            skLineSegment(sketch, "E69", {"start": v(-11, -24) * mm, "end": v(-11, -21) * mm});
            skLineSegment(sketch, "E70", {"start": v(-11, -24) * mm, "end": v(-9, -24) * mm});
            skLineSegment(sketch, "E71", {"start": v(-21.27, -6) * mm, "end": v(-21.27, 0) * mm});
            skLineSegment(sketch, "E72", {"start": v(-21.27, 0) * mm, "end": v(-9, 0) * mm});
            skArc(sketch, "E73.filletArc", {"start": v(-11, -21) * mm, "mid": v(-15.4, -10.4) * mm, "end": v(-26, -6) * mm});
            skLineSegment(sketch, "E74", {"start": v(-9, 0) * mm, "end": v(-9, -24) * mm});
            skLineSegment(sketch, "E75", {"start": v(-11, -21) * mm, "end": v(0, -21) * mm});
            skSolve(sketch);
        }
        {
            var Q0;
            Q0=makeQuery(id+"F9.boolean.opBoolean","COPY",FACE,{"derivedFrom":makeQuery(id+"F9.opExtrude","SWEPT_FACE",FACE,{"disambiguationData":[OSD([sQuery(id+"F4.wireOp",EDGE,"E49")])]})});
            var sketch = newSketch(context, id + "F17", { "sketchPlane" : qUnion([Q0])});
            skLineSegment(sketch, "E76", {"start": v(-32.22, 0) * mm, "end": v(-32.22, -6) * mm});
            skLineSegment(sketch, "E77", {"start": v(-32.22, -6) * mm, "end": v(-26, -6) * mm});
            skArc(sketch, "E78.filletArc", {"start": v(-11, -21) * mm, "mid": v(-15.4, -10.4) * mm, "end": v(-26, -6) * mm});
            skLineSegment(sketch, "E79", {"start": v(-11, -21) * mm, "end": v(-9, -21) * mm});
            skLineSegment(sketch, "E80", {"start": v(-9, -21) * mm, "end": v(-9, 0) * mm});
            skLineSegment(sketch, "E81", {"start": v(-9, 0) * mm, "end": v(-32.22, 0) * mm});
            skSolve(sketch);
        }
        {
            var Q0;
            Q0=makeQuery(id+"F16.imprint","IMPRINT",FACE,{"disambiguationData":[TD([[makeQuery(id+"F16.imprint","IMPRINT",EDGE,{"derivedFrom":sQuery(id+"F16.wireOp",EDGE,"E68")}),1.0]])]});
            extrude(context, id + "F18", {"entities" : qUnion([Q0]), "operationType" : NewBodyOperationType.ADD, "depth" : 1.5 * mm, "offsetDistance" : 25 * mm, "hasSecondDirection" : true, "secondDirectionOppositeDirection" : true, "secondDirectionDepth" : 0.5 * mm});
        }
        {
            var Q0;
            Q0=makeQuery(id+"F17.imprint","IMPRINT",FACE,{"disambiguationData":[TD([[makeQuery(id+"F17.imprint","IMPRINT",EDGE,{"derivedFrom":sQuery(id+"F17.wireOp",EDGE,"E76")}),1.0]])]});
            extrude(context, id + "F19", {"entities" : qUnion([Q0]), "operationType" : NewBodyOperationType.ADD, "depth" : 1.5 * mm, "offsetDistance" : 25 * mm, "hasSecondDirection" : true, "secondDirectionOppositeDirection" : true, "secondDirectionDepth" : 0.5 * mm});
        }
    });
